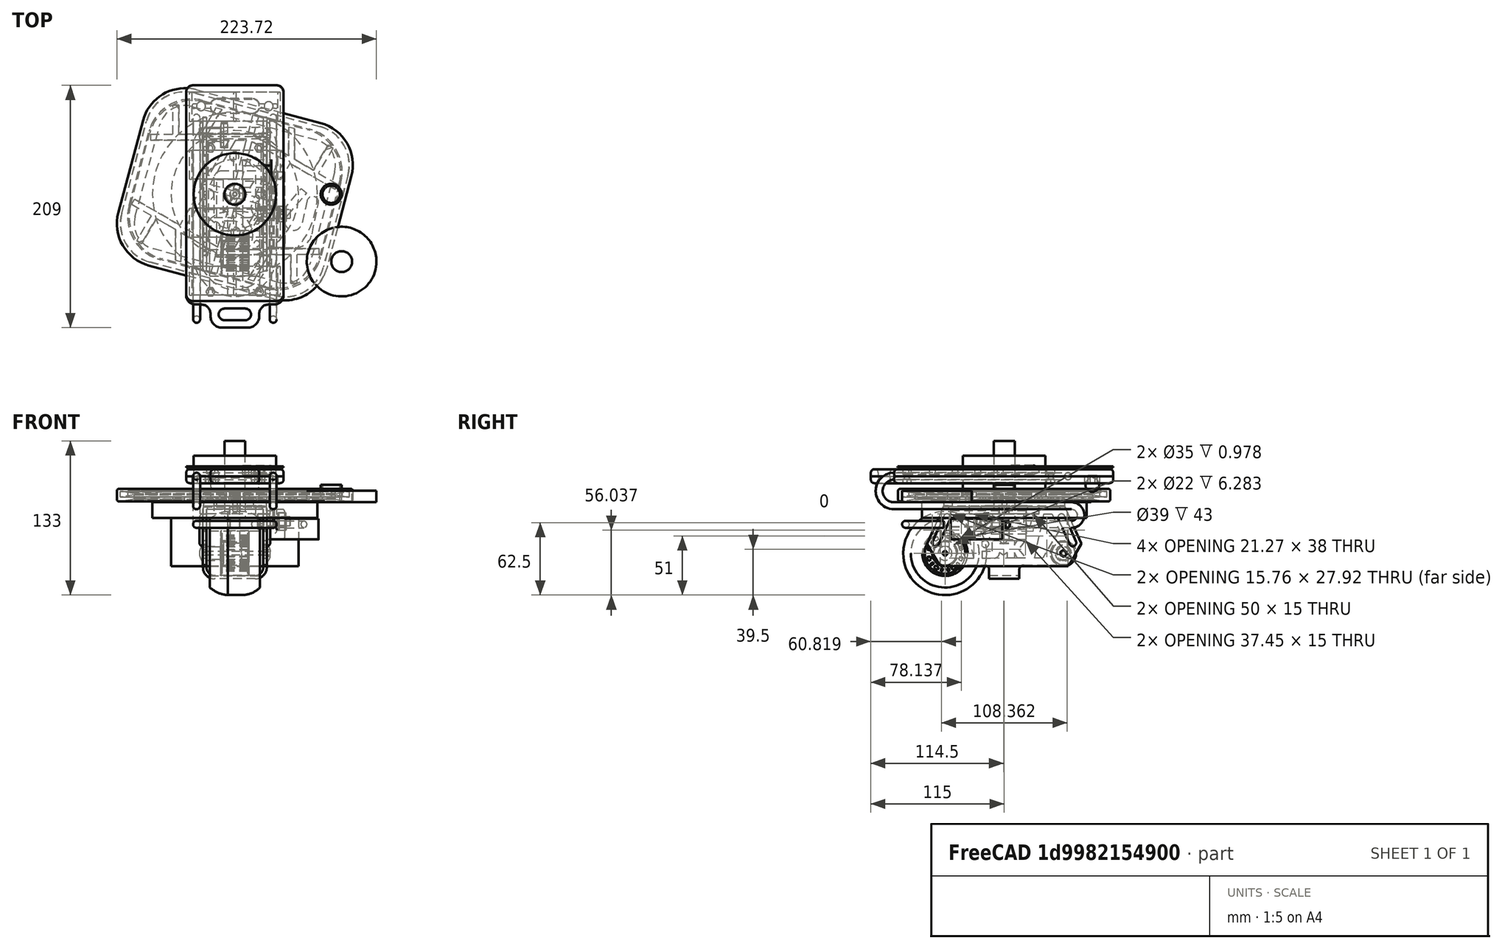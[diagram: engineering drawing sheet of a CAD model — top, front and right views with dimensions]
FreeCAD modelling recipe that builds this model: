
FCSTD DOCUMENT  (FreeCAD 1.0R39285 (Git))
Label: freeskate
License: All rights reserved
LicenseURL: http://en.wikipedia.org/wiki/All_rights_reserved
objects: Sketcher::SketchObject×70, PartDesign::Body×41, PartDesign::Pad×28, PartDesign::FeatureBase×14, PartDesign::Pocket×13, Part::Mirroring×12, PartDesign::Revolution×7, PartDesign::Mirrored×6, Part::Extrusion×4, Part::Cut×4, App::Part×4, PartDesign::MultiTransform×3, PartDesign::SubShapeBinder×3, Part::Revolution×2, App::Link×2, App::FeaturePython×2, PartDesign::AdditivePipe×2, PartDesign::Fillet×2, Part::MultiFuse×2, Part::Offset2D×1, +8 more types
note: 421 computed .brp shape members not serialized (recipe doc carries the construction recipe); baked Part::Feature solids carry a one-line shape summary decoded from their .brp

FEATURE [Sketcher::SketchObject] Sketch  label="plate-outline"
  ArcFitTolerance = 0
  AttachmentOffset = pos=(0,0,4.5) rot=(0,0,1;0rad)
  AttachmentSupport = -> [XY_Plane]
  FullyConstrained = true
  MakeInternals = false
  MapMode = 5
  Placement = pos=(0,0,4.5) rot=(0,0,1;0rad)
  sketch-geometry (8):
    g0: LineSegment StartX=-33 StartY=85.5 StartZ=0 EndX=33 EndY=85.5 EndZ=0
    g1: LineSegment StartX=71 StartY=47.5 StartZ=0 EndX=71 EndY=-47.5 EndZ=0
    g2: LineSegment StartX=33 StartY=-85.5 StartZ=0 EndX=-33 EndY=-85.5 EndZ=0
    g3: LineSegment StartX=-71 StartY=-47.5 StartZ=0 EndX=-71 EndY=47.5 EndZ=0
    g4: ArcOfCircle CenterX=-33 CenterY=47.5 CenterZ=0 NormalX=0 NormalY=0 NormalZ=1 AngleXU=0 Radius=38 StartAngle=1.5708 EndAngle=3.14159
    g5: ArcOfCircle CenterX=33 CenterY=47.5 CenterZ=0 NormalX=0 NormalY=0 NormalZ=1 AngleXU=0 Radius=38 StartAngle=0 EndAngle=1.5708
    g6: ArcOfCircle CenterX=33 CenterY=-47.5 CenterZ=0 NormalX=0 NormalY=0 NormalZ=1 AngleXU=0 Radius=38 StartAngle=4.71239 EndAngle=6.28319
    g7: ArcOfCircle CenterX=-33 CenterY=-47.5 CenterZ=0 NormalX=0 NormalY=0 NormalZ=1 AngleXU=0 Radius=38 StartAngle=3.14159 EndAngle=4.71239
  constraints (18):
    c: Horizontal(g2)
    c: Vertical(g3)
    c: Tangent(g0,g4) = 1.5708
    c: Tangent(g3,g4) = 1.5708
    c: Tangent(g0,g5) = 1.5708
    c: Tangent(g1,g5) = 1.5708
    c: Tangent(g1,g6) = 1.5708
    c: Tangent(g2,g6) = 1.5708
    c: Tangent(g2,g7) = 1.5708
    c: Tangent(g3,g7) = 1.5708
    c: DistanceY(g2,g0) = 171
    c: DistanceX(g3,g1) = 142
    c: Symmetric(g0,g2,g-1)
    c: Horizontal(g0)
    c: Symmetric(g3,g1,g-2)
    c: Vertical(g1)
    c: Radius(g5) = 38
    c: Radius(g6) = 38
FEATURE [PartDesign::Pad] Pad  label="plate-outline-pad"
  Direction = (0,0,1)
  Length = 5
  Length2 = 10
  Profile = -> Sketch
  ReferenceAxis = -> Sketch [N_Axis]
  Suppressed = false
  Type = 0
FEATURE [Sketcher::SketchObject] Sketch002  label="chassis-channel"
  ArcFitTolerance = 0
  FullyConstrained = true
  MakeInternals = false
  MapMode = 5
  Placement = pos=(0,0,0) rot=(1,0,0;1.5708rad)
  sketch-geometry (8):
    g0: LineSegment StartX=-24.5 StartY=-3 StartZ=0 EndX=24.5 EndY=-3 EndZ=0
    g1: LineSegment StartX=27.5 StartY=-6 StartZ=0 EndX=27.5 EndY=-56 EndZ=0
    g2: LineSegment StartX=17.5 StartY=-66 StartZ=0 EndX=-17.5 EndY=-66 EndZ=0
    g3: LineSegment StartX=-27.5 StartY=-56 StartZ=0 EndX=-27.5 EndY=-6 EndZ=0
    g4: ArcOfCircle CenterX=-24.5 CenterY=-6 CenterZ=0 NormalX=0 NormalY=0 NormalZ=1 AngleXU=0 Radius=3 StartAngle=1.5708 EndAngle=3.14159
    g5: ArcOfCircle CenterX=24.5 CenterY=-6 CenterZ=0 NormalX=0 NormalY=0 NormalZ=1 AngleXU=0 Radius=3 StartAngle=0 EndAngle=1.5708
    g6: ArcOfCircle CenterX=17.5 CenterY=-56 CenterZ=0 NormalX=0 NormalY=0 NormalZ=1 AngleXU=0 Radius=10 StartAngle=4.71239 EndAngle=6.28319
    g7: ArcOfCircle CenterX=-17.5 CenterY=-56 CenterZ=0 NormalX=0 NormalY=0 NormalZ=1 AngleXU=0 Radius=10 StartAngle=3.14159 EndAngle=4.71239
  constraints (19):
    c: Horizontal(g0)
    c: Horizontal(g2)
    c: Vertical(g1)
    c: Vertical(g3)
    c: Tangent(g0,g4) = 1.5708
    c: Tangent(g3,g4) = 1.5708
    c: Tangent(g0,g5) = 1.5708
    c: Tangent(g1,g5) = 1.5708
    c: Tangent(g1,g6) = 1.5708
    c: Tangent(g2,g6) = 1.5708
    c: Tangent(g2,g7) = 1.5708
    c: Tangent(g3,g7) = 1.5708
    c: DistanceX(g3,g1) = 55
    c: DistanceY(g2,g0) = 63
    c: Radius(g6) = 10
    c: Radius(g7) = 10
    c: Radius(g5) = 3
    c: Symmetric(g3,g1,g-2)
    c: DistanceY(g0,g-1) = 3
FEATURE [Part::Offset2D] Offset2D
  Fill = true
  Intersection = false
  Join = 0
  Mode = 1
  SelfIntersection = false
  Source = -> Sketch002
  Value = -3
FEATURE [Part::Extrusion] Extrude
  Base = -> Offset2D
  Dir = (0,1,0)
  DirMode = 0
  FaceMakerClass = Part::FaceMakerBullseye
  FaceMakerMode = 3
  LengthFwd = 67
  LengthRev = 67
  Solid = true
  Symmetric = false
FEATURE [Sketcher::SketchObject] Sketch003  label="chassis-profile"
  ArcFitTolerance = 0
  AttachmentSupport = -> [YZ_Plane]
  FullyConstrained = true
  MakeInternals = false
  MapMode = 5
  Placement = pos=(0,0,0) rot=(0.57735,0.57735,0.57735;2.0944rad)
  sketch-geometry (62):
    g0: LineSegment StartX=-52 StartY=-3 StartZ=0 EndX=-66.1267 EndY=-35.1023 EndZ=0
    g1: LineSegment StartX=-66.0262 StartY=-36.7474 StartZ=0 EndX=-56.2891 EndY=-53.1201 EndZ=0
    g2: LineSegment StartX=56.2891 StartY=-53.1201 StartZ=0 EndX=66.0262 EndY=-36.7474 EndZ=0
    g3: LineSegment StartX=66.1267 StartY=-35.1023 StartZ=0 EndX=52 EndY=-3 EndZ=0
    g4: LineSegment StartX=52 StartY=-3 StartZ=0 EndX=-52 EndY=-3 EndZ=0
    g5: LineSegment StartX=-13 StartY=-58 StartZ=0 EndX=-13 EndY=-79 EndZ=0
    g6: LineSegment StartX=-13 StartY=-79 StartZ=0 EndX=13 EndY=-79 EndZ=0
    g7: LineSegment StartX=13 StartY=-79 StartZ=0 EndX=13 EndY=-58 EndZ=0
    g8: LineSegment StartX=-54.742 StartY=-54 StartZ=0 EndX=-17 EndY=-54 EndZ=0
    g9: LineSegment StartX=17 StartY=-54 StartZ=0 EndX=54.742 EndY=-54 EndZ=0
    g10: LineSegment StartX=-34.3393 StartY=-10 StartZ=0 EndX=-41.3393 EndY=-10 EndZ=0
    g11: LineSegment StartX=-41.3393 StartY=-10 StartZ=0 EndX=-47.5 EndY=-24 EndZ=0
    g12: LineSegment StartX=-47.5 StartY=-24 StartZ=0 EndX=-33.2268 EndY=-48 EndZ=0
    g13: LineSegment StartX=-33.2268 StartY=-48 StartZ=0 EndX=-26.2268 EndY=-48 EndZ=0
    g14: LineSegment StartX=-26.2268 StartY=-48 StartZ=0 EndX=-34.3393 EndY=-10 EndZ=0
    g15: LineSegment StartX=26.2268 StartY=-48 StartZ=0 EndX=34.3393 EndY=-10 EndZ=0
    g16: LineSegment StartX=34.3393 StartY=-10 StartZ=0 EndX=41.3393 EndY=-10 EndZ=0
    g17: LineSegment StartX=41.3393 StartY=-10 StartZ=0 EndX=47.5 EndY=-24 EndZ=0
    g18: LineSegment StartX=47.5 StartY=-24 StartZ=0 EndX=33.2268 EndY=-48 EndZ=0
    g19: LineSegment StartX=33.2268 StartY=-48 StartZ=0 EndX=26.2268 EndY=-48 EndZ=0
    g20: LineSegment StartX=25 StartY=-10 StartZ=0 EndX=-25 EndY=-10 EndZ=0
    g21: LineSegment StartX=-25 StartY=-10 StartZ=0 EndX=-22.2858 EndY=-22.7135 EndZ=0
    g22: LineSegment StartX=-22.2858 StartY=-22.7135 StartZ=0 EndX=0 EndY=-25 EndZ=0
    g23: LineSegment StartX=0 StartY=-25 StartZ=0 EndX=22.2858 EndY=-22.7135 EndZ=0
    g24: LineSegment StartX=22.2858 StartY=-22.7135 StartZ=0 EndX=25 EndY=-10 EndZ=0
    g25: Circle CenterX=-51 CenterY=-44 CenterZ=0 NormalX=0 NormalY=0 NormalZ=1 AngleXU=0 Radius=2
    g26: Circle CenterX=51 CenterY=-44 CenterZ=0 NormalX=0 NormalY=0 NormalZ=1 AngleXU=0 Radius=2
    g27: LineSegment StartX=-19.2268 StartY=-42 StartZ=0 EndX=-19.2268 EndY=-48 EndZ=0
    g28: LineSegment StartX=-19.2268 StartY=-48 StartZ=0 EndX=-8.22678 EndY=-48 EndZ=0
    g29: LineSegment StartX=-19.2268 StartY=-42 StartZ=0 EndX=-10.2268 EndY=-42 EndZ=0
    g30: LineSegment StartX=-10.2268 StartY=-42 StartZ=0 EndX=-10.2268 EndY=-33 EndZ=0
    g31: LineSegment StartX=-10.2268 StartY=-33 StartZ=0 EndX=-4.22678 EndY=-33 EndZ=0
    g32: LineSegment StartX=-4.22678 StartY=-33 StartZ=0 EndX=-0.72678 EndY=-36 EndZ=0
    g33: LineSegment StartX=-0.72678 StartY=-36 StartZ=0 EndX=2.77322 EndY=-33 EndZ=0
    g34: LineSegment StartX=2.77322 StartY=-33 StartZ=0 EndX=8.77322 EndY=-33 EndZ=0
    g35: LineSegment StartX=8.77322 StartY=-33 StartZ=0 EndX=8.77322 EndY=-37 EndZ=0
    g36: LineSegment StartX=8.77322 StartY=-37 StartZ=0 EndX=11.2268 EndY=-33 EndZ=0
    g37: LineSegment StartX=11.2268 StartY=-33 StartZ=0 EndX=18.2268 EndY=-33 EndZ=0
    g38: LineSegment StartX=18.2268 StartY=-33 StartZ=0 EndX=12.2268 EndY=-40.5 EndZ=0
    g39: LineSegment StartX=12.2268 StartY=-40.5 StartZ=0 EndX=18.2268 EndY=-48 EndZ=0
    g40: LineSegment StartX=18.2268 StartY=-48 StartZ=0 EndX=11.2268 EndY=-48 EndZ=0
    g41: LineSegment StartX=11.2268 StartY=-48 StartZ=0 EndX=8.77322 EndY=-43.5 EndZ=0
    g42: LineSegment StartX=8.77322 StartY=-43.5 StartZ=0 EndX=8.77322 EndY=-48 EndZ=0
    g43: LineSegment StartX=8.77322 StartY=-48 StartZ=0 EndX=2.77322 EndY=-48 EndZ=0
    g44: LineSegment StartX=2.77322 StartY=-48 StartZ=0 EndX=2.77322 EndY=-43.5 EndZ=0
    g45: LineSegment StartX=2.77322 StartY=-43.5 StartZ=0 EndX=-0.72678 EndY=-45.5 EndZ=0
    g46: LineSegment StartX=-0.72678 StartY=-45.5 StartZ=0 EndX=-4.22678 EndY=-43.5 EndZ=0
    g47: LineSegment StartX=-4.22678 StartY=-43.5 StartZ=0 EndX=-4.22678 EndY=-44 EndZ=0
    g48: Circle CenterX=-16.2268 CenterY=-36 CenterZ=0 NormalX=0 NormalY=0 NormalZ=1 AngleXU=0 Radius=3
    g49: ArcOfCircle CenterX=-8.22678 CenterY=-44 CenterZ=0 NormalX=0 NormalY=0 NormalZ=1 AngleXU=0 Radius=4 StartAngle=4.71239 EndAngle=6.28319
    g50: ArcOfCircle CenterX=17 CenterY=-58 CenterZ=0 NormalX=0 NormalY=0 NormalZ=1 AngleXU=0 Radius=4 StartAngle=1.5708 EndAngle=3.14159
    g51: GeomPoint [constr] X=13 Y=-54 Z=0
    g52: ArcOfCircle CenterX=-17 CenterY=-58 CenterZ=0 NormalX=0 NormalY=0 NormalZ=1 AngleXU=0 Radius=4 StartAngle=0 EndAngle=1.5708
    g53: GeomPoint [constr] X=-13 Y=-54 Z=0
    g54: ArcOfCircle CenterX=64.4791 CenterY=-35.8273 CenterZ=0 NormalX=0 NormalY=0 NormalZ=1 AngleXU=0 Radius=1.8 StartAngle=5.74666 EndAngle=6.69773
    g55: GeomPoint [constr] X=66.5 Y=-35.9507 Z=0
    g56: ArcOfCircle CenterX=-64.4791 CenterY=-35.8273 CenterZ=0 NormalX=0 NormalY=0 NormalZ=1 AngleXU=0 Radius=1.8 StartAngle=2.72704 EndAngle=3.67812
    g57: GeomPoint [constr] X=-66.5 Y=-35.9507 Z=0
    g58: ArcOfCircle CenterX=54.742 CenterY=-52.2 CenterZ=0 NormalX=0 NormalY=0 NormalZ=1 AngleXU=0 Radius=1.8 StartAngle=4.71239 EndAngle=5.74666
    g59: GeomPoint [constr] X=55.7658 Y=-54 Z=0
    g60: ArcOfCircle CenterX=-54.742 CenterY=-52.2 CenterZ=0 NormalX=0 NormalY=0 NormalZ=1 AngleXU=0 Radius=1.8 StartAngle=3.67812 EndAngle=4.71239
    g61: GeomPoint [constr] X=-55.7658 Y=-54 Z=0
  constraints (161):
    c: Coincident(g4,g3)
    c: Coincident(g4,g0)
    c: Distance(g57,g61) = 21
    c: Symmetric(g61,g59,g-2)
    c: Symmetric(g57,g55,g-2)
    c: DistanceX(g0,g3) = 104
    c: Symmetric(g0,g3,g-2)
    c: DistanceY(g0,g-1) = 3
    c: Vertical(g5)
    c: Coincident(g6,g5)
    c: Horizontal(g6)
    c: Coincident(g7,g6)
    c: Vertical(g7)
    c: Symmetric(g53,g51,g-2)
    c: Horizontal(g8)
    c: DistanceY(g6,g51) = 25
    c: DistanceY(g59,g3) = 51
    c: DistanceX(g5,g6) = 26
    c: Distance(g0,g57) = 36
    c: Horizontal(g10)
    c: Coincident(g11,g10)
    c: Coincident(g12,g11)
    c: Coincident(g13,g12)
    c: Horizontal(g13)
    c: Coincident(g14,g13)
    c: Coincident(g14,g10)
    c: Coincident(g16,g15)
    c: Coincident(g17,g16)
    c: Coincident(g18,g17)
    c: Coincident(g19,g15)
    c: Symmetric(g13,g15,g-2)
    c: Coincident(g19,g18)
    c: Symmetric(g18,g12,g-2)
    c: Symmetric(g10,g15,g-2)
    c: Symmetric(g10,g16,g-2)
    c: Symmetric(g11,g17,g-2)
    c: Coincident(g21,g20)
    c: Coincident(g22,g21)
    c: PointOnObject(g22,g-2)
    c: Coincident(g23,g22)
    c: Coincident(g24,g20)
    c: Symmetric(g21,g23,g-2)
    c: Symmetric(g20,g20,g-2)
    c: Coincident(g23,g24)
    c: Diameter(g25) = 4
    c: Diameter(g26) = 4
    c: Symmetric(g25,g26,g-2)
    c: DistanceX(g25,g26) = 102
    c: DistanceY(g25,g0) = 41
    c: DistanceX(g10,g10) = 7
    c: DistanceY(g10,g0) = 7
    c: Horizontal(g10,g20)
    c: Parallel(g0,g11)
    c: DistanceY(g11,g0) = 21
    c: DistanceY(g61,g12) = 6
    c: DistanceX(g12,g13) = 7
    c: Parallel(g12,g1)
    c: DistanceX(g11,g17) = 95
    c: DistanceX(g57,g55) = 133
    c: DistanceX(g20,g20) = 50
    c: Parallel(g14,g21)
    c: DistanceY(g22,g20) = 15
    c: Distance(g20,g21) = 13
    c: Vertical(g27)
    c: Coincident(g28,g27)
    c: Horizontal(g28)
    c: Coincident(g29,g27)
    c: Horizontal(g29)
    c: Coincident(g30,g29)
    c: Vertical(g30)
    c: Coincident(g31,g30)
    c: Horizontal(g31)
    c: Coincident(g32,g31)
    c: Coincident(g33,g32)
    c: Coincident(g34,g33)
    c: Horizontal(g34)
    c: Coincident(g35,g34)
    c: Vertical(g35)
    c: Coincident(g36,g35)
    c: Coincident(g37,g36)
    c: Horizontal(g37)
    c: Coincident(g38,g37)
    c: Coincident(g39,g38)
    c: Coincident(g40,g39)
    c: Horizontal(g40)
    c: Coincident(g41,g40)
    c: Coincident(g42,g41)
    c: Vertical(g42)
    c: Coincident(g43,g42)
    c: Horizontal(g43)
    c: Coincident(g44,g43)
    c: Vertical(g44)
    c: Coincident(g45,g44)
    c: Coincident(g46,g45)
    c: Coincident(g47,g46)
    c: Vertical(g47)
    c: Horizontal(g12,g27)
    c: Horizontal(g12,g43)
    c: Horizontal(g12,g40)
    c: DistanceY(g27,g30) = 15
    c: DistanceX(g13,g27) = 7
    c: DistanceX(g39,g15) = 8
    c: Vertical(g37,g39)
    c: DistanceX(g38,g39) = 6
    c: Horizontal(g30,g37)
    c: DistanceY(g38,g37) = 7.5
    c: DistanceX(g36,g37) = 7
    c: Horizontal(g30,g34)
    c: Diameter(g48) = 6
    c: DistanceY(g48,g30) = 3
    c: DistanceX(g27,g48) = 3
    c: DistanceX(g27,g29) = 9
    c: DistanceX(g30,g31) = 6
    c: DistanceX(g33,g34) = 6
    c: DistanceY(g32,g31) = 3
    c: DistanceX(g31,g32) = 3.5
    c: DistanceX(g32,g33) = 3.5
    c: DistanceY(g35,g34) = 4
    c: DistanceY(g27,g27) = 6
    c: DistanceY(g27,g46) = 4.5
    c: Horizontal(g46,g44)
    c: Horizontal(g46,g41)
    c: Vertical(g36,g40)
    c: Vertical(g35,g41)
    c: Vertical(g33,g44)
    c: Vertical(g32,g45)
    c: Vertical(g31,g46)
    c: DistanceY(g45,g46) = 2
    c: Tangent(g28,g49) = -1.5708
    c: Tangent(g47,g49) = 1.5708
    c: Radius(g49) = 4
    c: PointOnObject(g51,g7)
    c: PointOnObject(g51,g9)
    c: Tangent(g7,g50) = 1.5708
    c: Tangent(g9,g50) = 1.5708
    c: PointOnObject(g53,g5)
    c: PointOnObject(g53,g8)
    c: Tangent(g5,g52) = 1.5708
    c: Tangent(g8,g52) = 1.5708
    c: Radius(g52) = 4
    c: Radius(g50) = 4
    c: PointOnObject(g55,g2)
    c: PointOnObject(g55,g3)
    c: Tangent(g2,g54) = -1.5708
    c: Tangent(g3,g54) = -1.5708
    c: Radius(g54) = 1.8
    c: PointOnObject(g57,g0)
    c: PointOnObject(g57,g1)
    c: Tangent(g0,g56) = -1.5708
    c: Tangent(g1,g56) = -1.5708
    c: Radius(g56) = 1.8
    c: PointOnObject(g59,g2)
    c: PointOnObject(g59,g9)
    c: Tangent(g2,g58) = -1.5708
    c: Tangent(g9,g58) = -1.5708
    c: PointOnObject(g61,g1)
    c: PointOnObject(g61,g8)
    c: Tangent(g1,g60) = -1.5708
    c: Tangent(g8,g60) = -1.5708
    c: Radius(g58) = 1.8
    c: Radius(g60) = 1.8
FEATURE [Part::Extrusion] Extrude001
  Base = -> Sketch003
  Dir = (1,0,0)
  DirMode = 0
  FaceMakerClass = Part::FaceMakerBullseye
  FaceMakerMode = 3
  LengthFwd = 30
  LengthRev = 30
  Solid = true
  Symmetric = false
FEATURE [Part::MultiCommon] Common  label="chassis-side-front"
  Shapes = -> [Extrude,Extrude001]
FEATURE [Sketcher::SketchObject] Sketch004  label="wheel-profile"
  ArcFitTolerance = 0
  AttachmentOffset = pos=(0,0,-44) rot=(0,0,1;0rad)
  AttachmentSupport = -> [XY_Plane]
  FullyConstrained = true
  MakeInternals = false
  MapMode = 5
  Placement = pos=(0,0,-44) rot=(0,0,1;0rad)
  sketch-geometry (7):
    g0: LineSegment StartX=-21.5 StartY=70.5 StartZ=0 EndX=-21.5 EndY=80.5 EndZ=0
    g1: ArcOfCircle CenterX=-4.64445 CenterY=62.0368 CenterZ=0 NormalX=0 NormalY=0 NormalZ=1 AngleXU=0 Radius=25 StartAngle=1.62504 EndAngle=2.31071
    g2: LineSegment StartX=-21.5 StartY=70.5 StartZ=0 EndX=21.5 EndY=70.5 EndZ=0
    g3: LineSegment StartX=21.5 StartY=70.5 StartZ=0 EndX=21.5 EndY=80.5 EndZ=0
    g4: LineSegment StartX=6 StartY=87 StartZ=0 EndX=-6 EndY=87 EndZ=0
    g5: ArcOfCircle CenterX=6 CenterY=65.2692 CenterZ=0 NormalX=0 NormalY=0 NormalZ=1 AngleXU=0 Radius=21.7308 StartAngle=0.776637 EndAngle=1.5708
    g6: GeomPoint [constr] X=0 Y=51 Z=0
  constraints (18):
    c: Vertical(g0)
    c: DistanceY(g0,g0) = 10
    c: Coincident(g2,g0)
    c: DistanceX(g2,g2) = 43
    c: Coincident(g3,g2)
    c: Coincident(g4,g1)
    c: Tangent(g4,g5) = -1.5708
    c: Symmetric(g1,g4,g-2)
    c: Symmetric(g0,g2,g-2)
    c: Symmetric(g0,g3,g-2)
    c: DistanceX(g1,g4) = 12
    c: Coincident(g1,g0)
    c: Coincident(g5,g3)
    c: Radius(g1) = 25
    c: PointOnObject(g6,g-2)
    c: DistanceY(g-1,g6) = 51
    c: DistanceY(g6,g0) = 19.5
    c: DistanceY(g6,g1) = 36
FEATURE [Part::Revolution] Revolve  label="wheel-back"
  Angle = 360
  Axis = (1,0,0)
  Base = (0,51,-44)
  FaceMakerClass = Part::FaceMakerBullseye
  Solid = true
  Source = -> Sketch004
  Symmetric = false
FEATURE [Part::Mirroring] Part__Mirroring  label="wheel-front"
  Base = (0,0,0)
  Normal = (0,1,0)
  Source = -> Revolve
FEATURE [Sketcher::SketchObject] Sketch008  label="axle-profile"
  ArcFitTolerance = 0
  AttachmentOffset = pos=(0,0,51) rot=(0,0,1;0rad)
  FullyConstrained = true
  MakeInternals = false
  MapMode = 5
  Placement = pos=(0,-51,1.1e-14) rot=(1,0,0;1.5708rad)
  sketch-geometry (9):
    g0: LineSegment StartX=27.5 StartY=-42.5 StartZ=0 EndX=-27.5 EndY=-42.5 EndZ=0
    g1: LineSegment StartX=-27.5 StartY=-42.5 StartZ=0 EndX=-27.5 EndY=-37 EndZ=0
    g2: LineSegment StartX=-27.5 StartY=-37 StartZ=0 EndX=-28 EndY=-37 EndZ=0
    g3: ArcOfCircle CenterX=-19.5 CenterY=-44 CenterZ=0 NormalX=0 NormalY=0 NormalZ=1 AngleXU=0 Radius=11.0114 StartAngle=2.45267 EndAngle=3.14159
    g4: GeomPoint [constr] X=0 Y=-44 Z=0
    g5: LineSegment StartX=27.5 StartY=-42.5 StartZ=0 EndX=27.5 EndY=-37 EndZ=0
    g6: LineSegment StartX=27.5 StartY=-37 StartZ=0 EndX=28 EndY=-37 EndZ=0
    g7: ArcOfCircle CenterX=23.5 CenterY=-42.5649 CenterZ=0 NormalX=0 NormalY=0 NormalZ=1 AngleXU=0 Radius=7.15671 StartAngle=6.0813 EndAngle=7.174
    g8: LineSegment StartX=-30.5114 StartY=-44 StartZ=0 EndX=30.5114 EndY=-44 EndZ=0
  constraints (24):
    c: Vertical(g1)
    c: Horizontal(g2)
    c: Coincident(g2,g1)
    c: Coincident(g1,g0)
    c: Coincident(g3,g2)
    c: PointOnObject(g4,g-2)
    c: DistanceY(g4,g-1) = 44
    c: Horizontal(g3,g4)
    c: Horizontal(g3,g4)
    c: Symmetric(g0,g0,g-2)
    c: DistanceX(g0,g4) = 27.5
    c: Coincident(g5,g0)
    c: Coincident(g6,g5)
    c: DistanceX(g1,g3) = 8
    c: DistanceX(g2,g1) = 0.5
    c: Symmetric(g1,g5,g-2)
    c: Symmetric(g2,g6,g-2)
    c: Coincident(g7,g6)
    c: Symmetric(g3,g7,g-2)
    c: DistanceY(g4,g0) = 1.5
    c: DistanceY(g4,g1) = 7
    c: DistanceX(g7,g5) = 4
    c: Coincident(g8,g3)
    c: Coincident(g8,g7)
FEATURE [Part::Revolution] Revolve001  label="axis-profile-revolve"
  Angle = 360
  Axis = (1,0,0)
  Base = (2,-51,-44)
  FaceMakerClass = Part::FaceMakerBullseye
  Solid = true
  Source = -> Sketch008
  Symmetric = false
FEATURE [Sketcher::SketchObject] Sketch009  label="axle-hex"
  ArcFitTolerance = 0
  AttachmentOffset = pos=(0,0,31) rot=(0,0,1;0rad)
  FullyConstrained = true
  MakeInternals = false
  MapMode = 5
  Placement = pos=(31,-7e-15,7e-15) rot=(0.57735,0.57735,0.57735;2.0944rad)
  sketch-geometry (7):
    g0: LineSegment StartX=-48.5 StartY=-42.5566 StartZ=0 EndX=-51 EndY=-41.1132 EndZ=0
    g1: LineSegment StartX=-51 StartY=-41.1132 StartZ=0 EndX=-53.5 EndY=-42.5566 EndZ=0
    g2: LineSegment StartX=-53.5 StartY=-42.5566 StartZ=0 EndX=-53.5 EndY=-45.4434 EndZ=0
    g3: LineSegment StartX=-53.5 StartY=-45.4434 StartZ=0 EndX=-51 EndY=-46.8868 EndZ=0
    g4: LineSegment StartX=-51 StartY=-46.8868 StartZ=0 EndX=-48.5 EndY=-45.4434 EndZ=0
    g5: LineSegment StartX=-48.5 StartY=-45.4434 StartZ=0 EndX=-48.5 EndY=-42.5566 EndZ=0
    g6: Circle [constr] CenterX=-51 CenterY=-44 CenterZ=0 NormalX=0 NormalY=0 NormalZ=1 AngleXU=0 Radius=2.88675
  constraints (17):
    c: Coincident(g0,g1)
    c: Coincident(g1,g2)
    c: Coincident(g2,g3)
    c: Coincident(g3,g4)
    c: Coincident(g4,g5)
    c: Coincident(g5,g0)
    c: Equal(g0, g1-g5) x5
    c: PointOnObject(g0,g6)
    c: PointOnObject(g1,g6)
    c: PointOnObject(g2,g6)
    c: PointOnObject(g3,g6)
    c: PointOnObject(g4,g6)
    c: PointOnObject(g5,g6)
    c: Vertical(g5)
    c: DistanceY(g6,g-1) = 44
    c: DistanceX(g2,g4) = 5
    c: DistanceX(g6,g-1) = 51
FEATURE [Part::Extrusion] Extrude002  label="axle-hex-extrude"
  Base = -> Sketch009
  Dir = (-1,0,0)
  DirMode = 0
  FaceMakerClass = Part::FaceMakerBullseye
  FaceMakerMode = 3
  LengthFwd = 3
  LengthRev = 0
  Solid = true
  Symmetric = false
FEATURE [Part::Cut] Cut  label="axle-front"
  Base = -> Revolve001
  Tool = -> Extrude002
FEATURE [Part::Mirroring] Part__Mirroring001  label="axle-back"
  Base = (0,0,0)
  Normal = (0,1,0)
  Source = -> Cut
FEATURE [Sketcher::SketchObject] Sketch010  label="outline"
  ArcFitTolerance = 0
  AttachmentSupport = -> [XY_Plane002]
  FullyConstrained = true
  MakeInternals = false
  MapMode = 5
  sketch-geometry (6):
    g0: LineSegment StartX=16 StartY=52 StartZ=0 EndX=27 EndY=45 EndZ=0
    g1: LineSegment StartX=-27 StartY=52 StartZ=0 EndX=16 EndY=52 EndZ=0
    g2: LineSegment StartX=27 StartY=45 StartZ=0 EndX=27 EndY=-52 EndZ=0
    g3: LineSegment StartX=-27 StartY=-45 StartZ=0 EndX=-16 EndY=-52 EndZ=0
    g4: LineSegment StartX=-27 StartY=52 StartZ=0 EndX=-27 EndY=-45 EndZ=0
    g5: LineSegment StartX=-16 StartY=-52 StartZ=0 EndX=27 EndY=-52 EndZ=0
  constraints (18):
    c: Coincident(g1,g0)
    c: Horizontal(g1)
    c: Coincident(g2,g0)
    c: Vertical(g2)
    c: Coincident(g4,g1)
    c: Coincident(g4,g3)
    c: Vertical(g4)
    c: Coincident(g5,g3)
    c: Coincident(g5,g2)
    c: Horizontal(g5)
    c: DistanceY(g0,g0) = 7
    c: DistanceX(g0,g0) = 11
    c: DistanceX(g1,g-1) = 27
    c: DistanceX(g-1,g0) = 27
    c: DistanceX(g3,g3) = 11
    c: DistanceY(g3,g3) = 7
    c: DistanceY(g-1,g1) = 52
    c: DistanceY(g2,g-1) = 52
FEATURE [PartDesign::Pad] Pad003  label="outline-pad"
  Direction = (0,0,1)
  Length = 4
  Length2 = 10
  Profile = -> Sketch010
  ReferenceAxis = -> Sketch010 [N_Axis]
  Reversed = true
  Suppressed = false
  Type = 0
FEATURE [PartDesign::Body] Body002  label="shock-absorber"
  AllowCompound = false
  Group = -> [Sketch010,Pad003]
  Origin = -> Origin002
  Tip = -> Pad003
FEATURE [Sketcher::SketchObject] Sketch011  label="chassis-top"
  ArcFitTolerance = 0
  AttachmentSupport = -> [XY_Plane002]
  FullyConstrained = true
  MakeInternals = false
  MapMode = 5
  sketch-geometry (18):
    g0: LineSegment StartX=-24 StartY=58 StartZ=0 EndX=24 EndY=58 EndZ=0
    g1: LineSegment StartX=24 StartY=58 StartZ=0 EndX=23.5 EndY=51 EndZ=0
    g2: LineSegment StartX=20.2781 StartY=48 StartZ=0 EndX=-20.2781 EndY=48 EndZ=0
    g3: LineSegment StartX=-23.5 StartY=51 StartZ=0 EndX=-24 EndY=58 EndZ=0
    g4: LineSegment StartX=-12 StartY=20 StartZ=0 EndX=18 EndY=20 EndZ=0
    g5: LineSegment StartX=18 StartY=20 StartZ=0 EndX=18 EndY=-14 EndZ=0
    g6: LineSegment StartX=12 StartY=-20 StartZ=0 EndX=-18 EndY=-20 EndZ=0
    g7: LineSegment StartX=-18 StartY=-20 StartZ=0 EndX=-18 EndY=14 EndZ=0
    g8: LineSegment StartX=-20.2781 StartY=-48 StartZ=0 EndX=20.2781 EndY=-48 EndZ=0
    g9: LineSegment StartX=23.2629 StartY=-50.6987 StartZ=0 EndX=24 EndY=-58 EndZ=0
    g10: LineSegment StartX=24 StartY=-58 StartZ=0 EndX=-24 EndY=-58 EndZ=0
    g11: LineSegment StartX=-24 StartY=-58 StartZ=0 EndX=-23.5 EndY=-51 EndZ=0
    g12: ArcOfCircle CenterX=-20.2781 CenterY=51.2301 CenterZ=0 NormalX=0 NormalY=0 NormalZ=1 AngleXU=0 Radius=3.23014 StartAngle=3.2129 EndAngle=4.71239
    g13: ArcOfCircle CenterX=20.2781 CenterY=51.2301 CenterZ=0 NormalX=0 NormalY=0 NormalZ=1 AngleXU=0 Radius=3.23014 StartAngle=4.71239 EndAngle=6.21188
    g14: ArcOfCircle CenterX=-20.2781 CenterY=-51.2301 CenterZ=0 NormalX=0 NormalY=0 NormalZ=1 AngleXU=0 Radius=3.23014 StartAngle=1.5708 EndAngle=3.07029
    g15: ArcOfCircle CenterX=20.2781 CenterY=-51 CenterZ=0 NormalX=0 NormalY=0 NormalZ=1 AngleXU=0 Radius=3 StartAngle=0.100613 EndAngle=1.5708
    g16: ArcOfCircle CenterX=-12 CenterY=14 CenterZ=0 NormalX=0 NormalY=0 NormalZ=1 AngleXU=0 Radius=6 StartAngle=1.5708 EndAngle=3.14159
    g17: ArcOfCircle CenterX=12 CenterY=-14 CenterZ=0 NormalX=0 NormalY=0 NormalZ=1 AngleXU=0 Radius=6 StartAngle=4.71239 EndAngle=6.28319
  constraints (42):
    c: Coincident(g0,g1)
    c: Coincident(g3,g0)
    c: Coincident(g4,g5)
    c: Coincident(g6,g7)
    c: Horizontal(g4)
    c: Horizontal(g6)
    c: Vertical(g5)
    c: Vertical(g7)
    c: Coincident(g9,g10)
    c: Coincident(g10,g11)
    c: Symmetric(g0,g0,g-2)
    c: DistanceX(g0,g0) = 48
    c: Tangent(g2,g12) = 1.5708
    c: Tangent(g3,g12) = 1.5708
    c: Tangent(g1,g13) = 1.5708
    c: Tangent(g2,g13) = 1.5708
    c: DistanceY(g2,g0) = 10
    c: DistanceY(g-1,g2) = 48
    c: DistanceX(g3,g1) = 47
    c: Tangent(g8,g14) = 1.5708
    c: Tangent(g11,g14) = 1.5708
    c: Tangent(g8,g15) = 1.5708
    c: Tangent(g9,g15) = 1.5708
    c: Radius(g15) = 3
    c: Symmetric(g2,g8,g-1)
    c: Symmetric(g10,g0,g-1)
    c: Symmetric(g9,g0,g-1)
    c: Symmetric(g11,g3,g-1)
    c: Symmetric(g3,g1,g-2)
    c: Symmetric(g2,g2,g-2)
    c: DistanceY(g2,g3) = 3
    c: Symmetric(g8,g2,g-1)
    c: Tangent(g4,g16) = 1.5708
    c: Tangent(g7,g16) = 1.5708
    c: Tangent(g5,g17) = 1.5708
    c: Tangent(g6,g17) = 1.5708
    c: Radius(g16) = 6
    c: Radius(g17) = 6
    c: DistanceY(g6,g-1) = 20
    c: DistanceY(g-1,g4) = 20
    c: DistanceX(g6,g-1) = 18
    c: DistanceX(g-1,g4) = 18
FEATURE [Part::Extrusion] Extrude003  label="chassis-top-extrude"
  Base = -> Sketch011
  Dir = (0,0,-1)
  DirMode = 0
  FaceMakerClass = Part::FaceMakerBullseye
  FaceMakerMode = 3
  LengthFwd = 10
  LengthRev = 0
  Solid = true
  Symmetric = false
FEATURE [Part::Cut] Cut001  label="chassis-base"
  Base = -> Common
  Tool = -> Extrude003
FEATURE [Sketcher::SketchObject] Sketch012  label="top-profile"
  ArcFitTolerance = 0
  AttachmentOffset = pos=(0,0,-44) rot=(0,0,1;0rad)
  FullyConstrained = false
  MakeInternals = false
  MapMode = 5
  Placement = pos=(0,51,-44) rot=(0,0,1;0rad)
  sketch-geometry (13):
    g0: LineSegment StartX=11.9778 StartY=-19.5 StartZ=0 EndX=-11.9778 EndY=-19.5 EndZ=0
    g1: LineSegment StartX=-11.9778 StartY=-19.5 StartZ=0 EndX=-11.9778 EndY=-17.5 EndZ=0
    g2: LineSegment StartX=-11.9778 StartY=-17.5 StartZ=0 EndX=-11 EndY=-17.5 EndZ=0
    g3: LineSegment StartX=-11 StartY=-17.5 StartZ=0 EndX=-12 EndY=-11 EndZ=0
    g4: LineSegment StartX=-12 StartY=-11 StartZ=0 EndX=-5.71671 EndY=-11 EndZ=0
    g5: LineSegment StartX=-5.71671 StartY=-11 StartZ=0 EndX=-5.71671 EndY=-10 EndZ=0
    g6: LineSegment StartX=-5.71671 StartY=-10 StartZ=0 EndX=5.71671 EndY=-10 EndZ=0
    g7: LineSegment StartX=5.71671 StartY=-10 StartZ=0 EndX=5.71671 EndY=-11 EndZ=0
    g8: LineSegment StartX=5.71671 StartY=-11 StartZ=0 EndX=12 EndY=-11 EndZ=0
    g9: LineSegment StartX=12 StartY=-11 StartZ=0 EndX=11 EndY=-17.5 EndZ=0
    g10: LineSegment StartX=11 StartY=-17.5 StartZ=0 EndX=11.9778 EndY=-17.5 EndZ=0
    g11: LineSegment StartX=11.9778 StartY=-17.5 StartZ=0 EndX=11.9778 EndY=-19.5 EndZ=0
    g12: GeomPoint [constr] X=0 Y=0 Z=0
  constraints (29):
    c: Coincident(g1,g0)
    c: Vertical(g1)
    c: Coincident(g2,g1)
    c: Horizontal(g2)
    c: Coincident(g3,g2)
    c: Horizontal(g4)
    c: Coincident(g5,g4)
    c: Vertical(g5)
    c: Coincident(g6,g5)
    c: Coincident(g7,g6)
    c: Coincident(g8,g7)
    c: Coincident(g9,g8)
    c: Coincident(g10,g9)
    c: Coincident(g11,g10)
    c: Coincident(g11,g0)
    c: Symmetric(g0,g0,g-2)
    c: Symmetric(g1,g10,g-2)
    c: Symmetric(g2,g9,g-2)
    c: Symmetric(g3,g8,g-2)
    c: Coincident(g3,g4)
    c: Symmetric(g4,g7,g-2)
    c: Symmetric(g5,g6,g-2)
    c: DistanceY(g0,g12) = 19.5
    c: DistanceX(g3,g8) = 24
    c: DistanceX(g3,g2) = 1
    c: DistanceY(g3,g12) = 11
    c: DistanceY(g5,g12) = 10
    c: DistanceY(g1,g1) = 2
    c: Coincident(g12,g-1)
FEATURE [Sketcher::SketchObject] Sketch018  label="rib-outlines"
  ArcFitTolerance = 0
  AttachmentSupport = -> [XY_Plane]
  FullyConstrained = true
  MakeInternals = false
  MapMode = 5
  sketch-geometry (29):
    g0: LineSegment StartX=-2.5 StartY=2.5 StartZ=0 EndX=-47.8236 EndY=2.5 EndZ=0
    g1: LineSegment StartX=-2.5 StartY=2.5 StartZ=0 EndX=-2.5 EndY=22.8798 EndZ=0
    g2: LineSegment StartX=0 StartY=28.726 StartZ=0 EndX=-38.0635 EndY=38.9251 EndZ=0
    g3: LineSegment StartX=-38.0635 StartY=38.9251 StartZ=0 EndX=-26.4167 EndY=82.3918 EndZ=0
    g4: LineSegment StartX=-31.2463 StartY=83.6859 StartZ=0 EndX=-26.4167 EndY=82.3918 EndZ=0
    g5: LineSegment StartX=-53 StartY=2.5 StartZ=0 EndX=-70 EndY=2.5 EndZ=0
    g6: LineSegment StartX=-70 StartY=2.5 StartZ=0 EndX=-70 EndY=0 EndZ=0
    g7: LineSegment StartX=-70 StartY=0 StartZ=0 EndX=0 EndY=0 EndZ=0
    g8: LineSegment StartX=0 StartY=0 StartZ=0 EndX=0 EndY=28.726 EndZ=0
    g9: LineSegment StartX=-39.3576 StartY=34.0955 StartZ=0 EndX=-43.952 EndY=16.9491 EndZ=0
    g10: LineSegment StartX=-43.952 StartY=16.9491 StartZ=0 EndX=-9.65926 EndY=26.1378 EndZ=0
    g11: LineSegment StartX=-9.65926 StartY=26.1378 StartZ=0 EndX=-39.3576 EndY=34.0955 EndZ=0
    g12: LineSegment StartX=-2.5 StartY=22.8798 StartZ=0 EndX=-45.4463 EndY=11.3723 EndZ=0
    g13: LineSegment StartX=-45.4463 StartY=11.3723 StartZ=0 EndX=-47.8236 EndY=2.5 EndZ=0
    g14: LineSegment StartX=-36.2863 StartY=64.8764 StartZ=0 EndX=-60.4344 EndY=71.3469 EndZ=0
    g15: LineSegment StartX=-60.4344 StartY=71.3469 StartZ=0 EndX=-61.7285 EndY=66.5172 EndZ=0
    g16: LineSegment StartX=-61.7285 StartY=66.5172 StartZ=0 EndX=-37.5804 EndY=60.0467 EndZ=0
    g17: LineSegment StartX=-42.498 StartY=41.6942 StartZ=0 EndX=-68 EndY=34.8609 EndZ=0
    g18: LineSegment StartX=-68 StartY=34.8609 StartZ=0 EndX=-68 EndY=29.8609 EndZ=0
    g19: LineSegment StartX=-68 StartY=29.8609 StartZ=0 EndX=-43.9413 EndY=36.3074 EndZ=0
    g20: LineSegment StartX=-31.2463 StartY=83.6859 StartZ=0 EndX=-36.2863 EndY=64.8764 EndZ=0
    g21: LineSegment StartX=-37.5804 StartY=60.0467 StartZ=0 EndX=-42.498 EndY=41.6942 EndZ=0
    g22: LineSegment StartX=-43.9413 StartY=36.3074 StartZ=0 EndX=-53 EndY=2.5 EndZ=0
    g23: LineSegment [constr] StartX=-31.2463 StartY=83.6859 StartZ=0 EndX=-53 EndY=2.5 EndZ=0
    g24: LineSegment [constr] StartX=-26.4167 StartY=82.3918 StartZ=0 EndX=-47.8236 EndY=2.5 EndZ=0
    g25: LineSegment [constr] StartX=-43.952 StartY=16.9491 StartZ=0 EndX=-49.5288 EndY=15.4548 EndZ=0
    g26: LineSegment [constr] StartX=-53 StartY=2.5 StartZ=0 EndX=-53.6699 EndY=0 EndZ=0
    g27: LineSegment [constr] StartX=-9.65926 StartY=26.1378 StartZ=0 EndX=0 EndY=28.726 EndZ=0
    g28: LineSegment [constr] StartX=-43.952 StartY=16.9491 StartZ=0 EndX=-42.6579 EndY=12.1195 EndZ=0
  constraints (83):
    c: Horizontal(g0)
    c: Coincident(g1,g0)
    c: Vertical(g1)
    c: PointOnObject(g2,g-2)
    c: Coincident(g3,g2)
    c: Coincident(g4,g3)
    c: Horizontal(g5)
    c: Coincident(g6,g5)
    c: PointOnObject(g6,g-1)
    c: Vertical(g6)
    c: Coincident(g7,g6)
    c: Coincident(g7,g-1)
    c: Coincident(g8,g7)
    c: Coincident(g8,g2)
    c: Coincident(g10,g9)
    c: Coincident(g11,g10)
    c: Coincident(g11,g9)
    c: Coincident(g12,g1)
    c: Coincident(g13,g12)
    c: Coincident(g13,g0)
    c: Coincident(g15,g14)
    c: Coincident(g16,g15)
    c: Coincident(g18,g17)
    c: Coincident(g19,g18)
    c: Coincident(g20,g4)
    c: Coincident(g20,g14)
    c: Coincident(g21,g16)
    c: Coincident(g21,g17)
    c: Coincident(g22,g19)
    c: Coincident(g22,g5)
    c: DistanceY(g6,g6) = 2.5
    c: Horizontal(g5,g0)
    c: Angle(g20,g4) = 1.5708
    c: Coincident(g23,g4)
    c: Coincident(g23,g5)
    c: Coincident(g24,g3)
    c: Coincident(g24,g0)
    c: PointOnObject(g14,g23)
    c: PointOnObject(g16,g23)
    c: PointOnObject(g17,g23)
    c: PointOnObject(g19,g23)
    c: PointOnObject(g12,g24)
    c: PointOnObject(g9,g24)
    c: PointOnObject(g2,g24)
    c: Distance(g14,g16) = 5
    c: Angle(g20,g14) = 1.5708
    c: Parallel(g14,g16)
    c: Angle(g15,g14) = 1.5708
    c: Vertical(g18)
    c: DistanceY(g18,g18) = 5
    c: Parallel(g17,g19)
    c: Distance(g2,g9) = 5
    c: Parallel(g11,g2)
    c: PointOnObject(g9,g24)
    c: Parallel(g10,g12)
    c: Distance(g4) = 5
    c: Angle(g2,g3) = 1.5708
    c: Parallel(g23,g24)
    c: DistanceX(g17,g2) = 68
    c: DistanceX(g5,g7) = 53
    c: DistanceX(g7,g7) = 70
    c: Angle(g10,g9) = 1.0472
    c: Coincident(g25,g9)
    c: PointOnObject(g25,g22)
    c: Parallel(g25,g10)
    c: Coincident(g26,g5)
    c: PointOnObject(g26,g7)
    c: Parallel(g22,g26)
    c: Distance(g26,g25) = 16
    c: Coincident(g27,g10)
    c: Coincident(g27,g2)
    c: Parallel(g10,g27)
    c: Angle(g21,g17) = 2.0944
    c: Distance(g22) = 35
    c: Distance(g21) = 19
    c: Angle(g2,g8) = 1.8326
    c: DistanceX(g0,g7) = 2.5
    c: Coincident(g28,g9)
    c: PointOnObject(g28,g12)
    c: Angle(g28,g10) = 1.5708
    c: Distance(g28) = 5
    c: Distance(g16) = 25
    c: Distance(g3) = 45
FEATURE [PartDesign::Pad] Pad007  label="rib-outlines-pad"
  BaseFeature = -> Pad
  Direction = (0,0,1)
  Length = 4.5
  Length2 = 10
  Profile = -> Sketch018
  ReferenceAxis = -> Sketch018 [N_Axis]
  Suppressed = false
  Type = 0
FEATURE [PartDesign::Mirrored] Mirrored
  MirrorPlane = -> Sketch018 [V_Axis]
  Suppressed = false
  TransformMode = 0
FEATURE [PartDesign::Mirrored] Mirrored001
  MirrorPlane = -> XZ_Plane
  Suppressed = false
  TransformMode = 0
FEATURE [PartDesign::MultiTransform] MultiTransform
  BaseFeature = -> Pad007
  Originals = -> [Pad007]
  Suppressed = false
  TransformMode = 0
  Transformations = -> [Mirrored,Mirrored001]
FEATURE [Sketcher::SketchObject] Sketch019  label="grip-tape-inset"
  ArcFitTolerance = 0
  AttachmentOffset = pos=(0,0,9.5) rot=(0,0,1;0rad)
  AttachmentSupport = -> [XY_Plane]
  FullyConstrained = true
  MakeInternals = false
  MapMode = 5
  Placement = pos=(0,0,9.5) rot=(0,0,1;0rad)
  sketch-geometry (16):
    g0: LineSegment [constr] StartX=-71 StartY=85.5 StartZ=0 EndX=71 EndY=85.5 EndZ=0
    g1: LineSegment [constr] StartX=71 StartY=85.5 StartZ=0 EndX=71 EndY=-85.5 EndZ=0
    g2: LineSegment [constr] StartX=71 StartY=-85.5 StartZ=0 EndX=-71 EndY=-85.5 EndZ=0
    g3: LineSegment [constr] StartX=-71 StartY=-85.5 StartZ=0 EndX=-71 EndY=85.5 EndZ=0
    g4: LineSegment StartX=-32 StartY=84.5 StartZ=0 EndX=32 EndY=84.5 EndZ=0
    g5: LineSegment StartX=70 StartY=46.5 StartZ=0 EndX=70 EndY=-46.5 EndZ=0
    g6: LineSegment StartX=32 StartY=-84.5 StartZ=0 EndX=-32 EndY=-84.5 EndZ=0
    g7: LineSegment StartX=-70 StartY=-46.5 StartZ=0 EndX=-70 EndY=46.5 EndZ=0
    g8: ArcOfCircle CenterX=-32 CenterY=46.5 CenterZ=0 NormalX=0 NormalY=0 NormalZ=1 AngleXU=0 Radius=38 StartAngle=1.5708 EndAngle=3.14159
    g9: GeomPoint [constr] X=-70 Y=84.5 Z=0
    g10: ArcOfCircle CenterX=-32 CenterY=-46.5 CenterZ=0 NormalX=0 NormalY=0 NormalZ=1 AngleXU=0 Radius=38 StartAngle=3.14159 EndAngle=4.71239
    g11: GeomPoint [constr] X=-70 Y=-84.5 Z=0
    g12: ArcOfCircle CenterX=32 CenterY=-46.5 CenterZ=0 NormalX=0 NormalY=0 NormalZ=1 AngleXU=0 Radius=38 StartAngle=4.71239 EndAngle=6.28319
    g13: GeomPoint [constr] X=70 Y=-84.5 Z=0
    g14: ArcOfCircle CenterX=32 CenterY=46.5 CenterZ=0 NormalX=0 NormalY=0 NormalZ=1 AngleXU=0 Radius=38 StartAngle=0 EndAngle=1.5708
    g15: GeomPoint [constr] X=70 Y=84.5 Z=0
  constraints (36):
    c: Coincident(g0,g1)
    c: Coincident(g1,g2)
    c: Coincident(g2,g3)
    c: Coincident(g3,g0)
    c: Horizontal(g2)
    c: Vertical(g3)
    c: DistanceX(g0,g0) = 142
    c: DistanceY(g1,g1) = 171
    c: Symmetric(g0,g0,g-2)
    c: Symmetric(g0,g1,g-1)
    c: Horizontal(g6)
    c: Vertical(g5)
    c: DistanceX(g2,g11) = 1
    c: DistanceY(g2,g11) = 1
    c: Symmetric(g9,g11,g-1)
    c: Symmetric(g9,g15,g-2)
    c: PointOnObject(g9,g4)
    c: PointOnObject(g9,g7)
    c: Tangent(g4,g8) = 1.5708
    c: Tangent(g7,g8) = 1.5708
    c: PointOnObject(g11,g6)
    c: PointOnObject(g11,g7)
    c: Tangent(g6,g10) = 1.5708
    c: Tangent(g7,g10) = 1.5708
    c: PointOnObject(g13,g5)
    c: PointOnObject(g13,g6)
    c: Tangent(g5,g12) = 1.5708
    c: Tangent(g6,g12) = 1.5708
    c: PointOnObject(g15,g4)
    c: PointOnObject(g15,g5)
    c: Tangent(g4,g14) = 1.5708
    c: Tangent(g5,g14) = 1.5708
    c: Radius(g8) = 38
    c: Radius(g14) = 38
    c: Radius(g12) = 38
    c: Radius(g10) = 38
FEATURE [PartDesign::Pocket] Pocket  label="grip-tape-inset-pocket"
  BaseFeature = -> MultiTransform
  Direction = (0,0,-1)
  Length = 0.5
  Length2 = 5
  Profile = -> Sketch019
  ReferenceAxis = -> Sketch019 [N_Axis]
  Suppressed = false
  Type = 0
FEATURE [Sketcher::SketchObject] Sketch020  label="ribs-taper-y"
  ArcFitTolerance = 0
  AttachmentSupport = -> [YZ_Plane]
  FullyConstrained = true
  MakeInternals = false
  MapMode = 5
  Placement = pos=(0,0,0) rot=(0.57735,0.57735,0.57735;2.0944rad)
  sketch-geometry (10):
    g0: LineSegment StartX=-84 StartY=4.5 StartZ=0 EndX=-46.7137 EndY=0.197732 EndZ=0
    g1: LineSegment StartX=46.7137 StartY=0.197732 StartZ=0 EndX=84 EndY=4.5 EndZ=0
    g2: LineSegment StartX=-43.275 StartY=0 StartZ=0 EndX=43.275 EndY=0 EndZ=0
    g3: LineSegment StartX=-84 StartY=4.5 StartZ=0 EndX=-84 EndY=-7.5 EndZ=0
    g4: LineSegment StartX=-84 StartY=-7.5 StartZ=0 EndX=84 EndY=-7.5 EndZ=0
    g5: LineSegment StartX=84 StartY=-7.5 StartZ=0 EndX=84 EndY=4.5 EndZ=0
    g6: ArcOfCircle CenterX=43.275 CenterY=30 CenterZ=0 NormalX=0 NormalY=0 NormalZ=1 AngleXU=0 Radius=30 StartAngle=4.71239 EndAngle=4.82727
    g7: GeomPoint [constr] X=45 Y=0 Z=0
    g8: ArcOfCircle CenterX=-43.275 CenterY=30 CenterZ=0 NormalX=0 NormalY=0 NormalZ=1 AngleXU=0 Radius=30 StartAngle=4.59751 EndAngle=4.71239
    g9: GeomPoint [constr] X=-45 Y=0 Z=0
  constraints (24):
    c: Symmetric(g0,g1,g-2)
    c: Symmetric(g9,g7,g-2)
    c: PointOnObject(g9,g-1)
    c: DistanceY(g9,g0) = 4.5
    c: Coincident(g3,g0)
    c: Vertical(g3)
    c: Coincident(g4,g3)
    c: Horizontal(g4)
    c: Coincident(g5,g4)
    c: Coincident(g5,g1)
    c: Vertical(g5)
    c: DistanceY(g3,g3) = 12
    c: DistanceX(g0,g1) = 168
    c: DistanceX(g9,g7) = 90
    c: PointOnObject(g7,g1)
    c: PointOnObject(g7,g2)
    c: Tangent(g1,g6) = -1.5708
    c: Tangent(g2,g6) = -1.5708
    c: Radius(g6) = 30
    c: PointOnObject(g9,g0)
    c: PointOnObject(g9,g2)
    c: Tangent(g0,g8) = -1.5708
    c: Tangent(g2,g8) = -1.5708
    c: Radius(g8) = 30
FEATURE [PartDesign::Pocket] Pocket003  label="ribs-taper-y-pocket"
  BaseFeature = -> Pocket
  Direction = (-1,0,0)
  Length = 180
  Length2 = 5
  Midplane = true
  Profile = -> Sketch020
  ReferenceAxis = -> Sketch020 [N_Axis]
  Suppressed = false
  Type = 0
FEATURE [Sketcher::SketchObject] Sketch021  label="ribs-taper-x"
  ArcFitTolerance = 0
  AttachmentSupport = -> [XZ_Plane]
  FullyConstrained = true
  MakeInternals = false
  MapMode = 5
  Placement = pos=(0,0,0) rot=(1,0,0;1.5708rad)
  sketch-geometry (10):
    g0: LineSegment StartX=-71 StartY=4.5 StartZ=0 EndX=-47.5392 EndY=0.439485 EndZ=0
    g1: LineSegment StartX=-42.423 StartY=0 StartZ=0 EndX=42.423 EndY=0 EndZ=0
    g2: LineSegment StartX=47.5392 StartY=0.439485 StartZ=0 EndX=71 EndY=4.5 EndZ=0
    g3: LineSegment StartX=71 StartY=4.5 StartZ=0 EndX=71 EndY=-7.5 EndZ=0
    g4: LineSegment StartX=71 StartY=-7.5 StartZ=0 EndX=-71 EndY=-7.5 EndZ=0
    g5: LineSegment StartX=-71 StartY=-7.5 StartZ=0 EndX=-71 EndY=4.5 EndZ=0
    g6: ArcOfCircle CenterX=42.423 CenterY=30 CenterZ=0 NormalX=0 NormalY=0 NormalZ=1 AngleXU=0 Radius=30 StartAngle=4.71239 EndAngle=4.88377
    g7: GeomPoint [constr] X=45 Y=0 Z=0
    g8: ArcOfCircle CenterX=-42.423 CenterY=30 CenterZ=0 NormalX=0 NormalY=0 NormalZ=1 AngleXU=0 Radius=30 StartAngle=4.54101 EndAngle=4.71239
    g9: GeomPoint [constr] X=-45 Y=0 Z=0
  constraints (24):
    c: PointOnObject(g9,g-1)
    c: Coincident(g3,g2)
    c: Vertical(g3)
    c: Coincident(g4,g3)
    c: Horizontal(g4)
    c: Coincident(g5,g4)
    c: Coincident(g5,g0)
    c: Vertical(g5)
    c: Symmetric(g0,g2,g-2)
    c: DistanceY(g5,g5) = 12
    c: DistanceY(g9,g0) = 4.5
    c: DistanceX(g9,g7) = 90
    c: DistanceX(g0,g2) = 142
    c: Symmetric(g9,g7,g-2)
    c: PointOnObject(g7,g1)
    c: PointOnObject(g7,g2)
    c: Tangent(g1,g6) = -1.5708
    c: Tangent(g2,g6) = -1.5708
    c: Radius(g6) = 30
    c: PointOnObject(g9,g0)
    c: PointOnObject(g9,g1)
    c: Tangent(g0,g8) = -1.5708
    c: Tangent(g1,g8) = -1.5708
    c: Radius(g8) = 30
FEATURE [PartDesign::Pocket] Pocket004  label="ribs-taper-x-pocket"
  BaseFeature = -> Pocket003
  Direction = (0,1,-2e-16)
  Length = 150
  Length2 = 5
  Midplane = true
  Profile = -> Sketch021
  ReferenceAxis = -> Sketch021 [N_Axis]
  Suppressed = false
  Type = 0
FEATURE [Sketcher::SketchObject] Sketch030  label="edge-guard-profile"
  ArcFitTolerance = 0
  AttachmentOffset = pos=(0,4.5,0) rot=(0,0,1;0rad)
  FullyConstrained = true
  MakeInternals = false
  MapMode = 5
  Placement = pos=(0,-1e-15,4.5) rot=(1,0,0;1.5708rad)
  sketch-geometry (20):
    g0: LineSegment StartX=75.3284 StartY=0 StartZ=0 EndX=75.5 EndY=0 EndZ=0
    g1: LineSegment StartX=75.5 StartY=0 StartZ=0 EndX=75.5 EndY=5 EndZ=0
    g2: LineSegment StartX=75.5 StartY=5 StartZ=0 EndX=75.3284 EndY=5 EndZ=0
    g3: LineSegment StartX=75.3284 StartY=5 StartZ=0 EndX=63.5 EndY=3 EndZ=0
    g4: LineSegment StartX=75.3284 StartY=0 StartZ=0 EndX=63.5 EndY=2 EndZ=0
    g5: LineSegment StartX=63.5 StartY=3 StartZ=0 EndX=63.5 EndY=5.2 EndZ=0
    g6: LineSegment StartX=63.5 StartY=5.2 StartZ=0 EndX=74.6663 EndY=7.08804 EndZ=0
    g7: LineSegment StartX=76 StartY=7.2 StartZ=0 EndX=76.5 EndY=7.2 EndZ=0
    g8: LineSegment StartX=78.5 StartY=5.2 StartZ=0 EndX=78.5 EndY=-1.8 EndZ=0
    g9: LineSegment StartX=76.5 StartY=-3.8 StartZ=0 EndX=76 EndY=-3.8 EndZ=0
    g10: LineSegment StartX=74.6663 StartY=-3.68804 StartZ=0 EndX=63.5 EndY=-1.8 EndZ=0
    g11: LineSegment StartX=63.5 StartY=-1.8 StartZ=0 EndX=63.5 EndY=2 EndZ=0
    g12: ArcOfCircle CenterX=76.5 CenterY=5.2 CenterZ=0 NormalX=0 NormalY=0 NormalZ=1 AngleXU=0 Radius=2 StartAngle=0 EndAngle=1.5708
    g13: GeomPoint [constr] X=78.5 Y=7.2 Z=0
    g14: ArcOfCircle CenterX=76.5 CenterY=-1.8 CenterZ=0 NormalX=0 NormalY=0 NormalZ=1 AngleXU=0 Radius=2 StartAngle=4.71239 EndAngle=6.28319
    g15: GeomPoint [constr] X=78.5 Y=-3.8 Z=0
    g16: ArcOfCircle CenterX=76 CenterY=4.2 CenterZ=0 NormalX=0 NormalY=0 NormalZ=1 AngleXU=0 Radius=8 StartAngle=4.54489 EndAngle=4.71239
    g17: GeomPoint [constr] X=75.3284 Y=-3.8 Z=0
    g18: ArcOfCircle CenterX=76 CenterY=-0.8 CenterZ=0 NormalX=0 NormalY=0 NormalZ=1 AngleXU=0 Radius=8 StartAngle=1.5708 EndAngle=1.7383
    g19: GeomPoint [constr] X=75.3284 Y=7.2 Z=0
  constraints (53):
    c: PointOnObject(g0,g-1)
    c: PointOnObject(g0,g-1)
    c: Coincident(g1,g0)
    c: Vertical(g1)
    c: Coincident(g2,g1)
    c: Horizontal(g2)
    c: DistanceY(g1,g1) = 5
    c: Coincident(g4,g0)
    c: Vertical(g0,g2)
    c: Vertical(g2,g3)
    c: Vertical(g3,g4)
    c: Coincident(g5,g3)
    c: Vertical(g5)
    c: Coincident(g6,g5)
    c: Horizontal(g7)
    c: Vertical(g8)
    c: Horizontal(g9)
    c: Coincident(g11,g10)
    c: Coincident(g11,g4)
    c: Vertical(g11)
    c: Parallel(g6,g3)
    c: Vertical(g19,g2)
    c: Vertical(g17,g0)
    c: Parallel(g4,g10)
    c: DistanceX(g0,g15) = 3
    c: DistanceX(g-1,g0) = 75.5
    c: PointOnObject(g13,g7)
    c: PointOnObject(g13,g8)
    c: Tangent(g7,g12) = 1.5708
    c: Tangent(g8,g12) = 1.5708
    c: Radius(g12) = 2
    c: PointOnObject(g15,g8)
    c: PointOnObject(g15,g9)
    c: Tangent(g8,g14) = 1.5708
    c: Tangent(g9,g14) = 1.5708
    c: Radius(g14) = 2
    c: PointOnObject(g17,g9)
    c: PointOnObject(g17,g10)
    c: Tangent(g9,g16) = 1.5708
    c: Tangent(g10,g16) = 1.5708
    c: Radius(g16) = 8
    c: PointOnObject(g19,g6)
    c: PointOnObject(g19,g7)
    c: Tangent(g6,g18) = 1.5708
    c: Tangent(g7,g18) = 1.5708
    c: Radius(g18) = 8
    c: DistanceX(g5,g8) = 15
    c: DistanceY(g5,g7) = 2
    c: DistanceY(g9,g10) = 2
    c: DistanceX(g7,g8) = 2.5
    c: DistanceY(g15,g13) = 11
    c: DistanceY(g10,g-1) = 1.8
    c: DistanceY(g5,g5) = 2.2
FEATURE [Sketcher::SketchObject] Sketch031  label="edge-guard-sweep-path"
  ArcFitTolerance = 0
  FullyConstrained = true
  MakeInternals = false
  MapMode = 5
  sketch-geometry (12):
    g0: LineSegment StartX=-41 StartY=85.5 StartZ=0 EndX=41 EndY=85.5 EndZ=0
    g1: LineSegment StartX=71 StartY=55.5 StartZ=0 EndX=71 EndY=-55.5 EndZ=0
    g2: LineSegment StartX=41 StartY=-85.5 StartZ=0 EndX=-41 EndY=-85.5 EndZ=0
    g3: LineSegment StartX=-71 StartY=-55.5 StartZ=0 EndX=-71 EndY=55.5 EndZ=0
    g4: ArcOfCircle CenterX=-41 CenterY=55.5 CenterZ=0 NormalX=0 NormalY=0 NormalZ=1 AngleXU=0 Radius=30 StartAngle=1.5708 EndAngle=3.14159
    g5: GeomPoint [constr] X=-71 Y=85.5 Z=0
    g6: ArcOfCircle CenterX=41 CenterY=55.5 CenterZ=0 NormalX=0 NormalY=0 NormalZ=1 AngleXU=0 Radius=30 StartAngle=0 EndAngle=1.5708
    g7: GeomPoint [constr] X=71 Y=85.5 Z=0
    g8: ArcOfCircle CenterX=-41 CenterY=-55.5 CenterZ=0 NormalX=0 NormalY=0 NormalZ=1 AngleXU=0 Radius=30 StartAngle=3.14159 EndAngle=4.71239
    g9: GeomPoint [constr] X=-71 Y=-85.5 Z=0
    g10: ArcOfCircle CenterX=41 CenterY=-55.5 CenterZ=0 NormalX=0 NormalY=0 NormalZ=1 AngleXU=0 Radius=30 StartAngle=4.71239 EndAngle=6.28319
    g11: GeomPoint [constr] X=71 Y=-85.5 Z=0
  constraints (26):
    c: Horizontal(g0)
    c: Horizontal(g2)
    c: Vertical(g1)
    c: Vertical(g3)
    c: PointOnObject(g5,g0)
    c: PointOnObject(g5,g3)
    c: Tangent(g0,g4) = 1.5708
    c: Tangent(g3,g4) = 1.5708
    c: PointOnObject(g7,g0)
    c: PointOnObject(g7,g1)
    c: Tangent(g0,g6) = 1.5708
    c: Tangent(g1,g6) = 1.5708
    c: PointOnObject(g9,g2)
    c: Tangent(g2,g8) = 1.5708
    c: Tangent(g3,g8) = 1.5708
    c: PointOnObject(g11,g1)
    c: Tangent(g1,g10) = 1.5708
    c: Tangent(g2,g10) = 1.5708
    c: Symmetric(g9,g11,g-2)
    c: Symmetric(g9,g5,g-1)
    c: DistanceX(g5,g7) = 142
    c: DistanceY(g11,g7) = 171
    c: Radius(g6) = 30
    c: Radius(g4) = 30
    c: Radius(g10) = 30
    c: Radius(g8) = 30
FEATURE [Part::Sweep] Sweep  label="edge-guard"
  Frenet = false
  Placement = pos=(0,0,0) rot=(0,0,1;1.309rad)
  Sections = -> [Sketch030]
  Solid = true
  Spine = -> Sketch031 [Edge7,Edge8,Edge6,Edge5,Edge4,Edge3,Edge2,Edge1]
  Transition = 1
FEATURE [PartDesign::FeatureBase] BaseFeature
  BaseFeature = -> Cut001
  Suppressed = false
FEATURE [Sketcher::SketchObject] Sketch032  label="grind-spline-outline"
  ArcFitTolerance = 0
  AttachmentOffset = pos=(49.3,-13,27.5) rot=(0,0,1;0.418879rad)
  AttachmentSupport = -> [YZ_Plane007]
  FullyConstrained = true
  MakeInternals = false
  MapMode = 5
  Placement = pos=(27.5,49.3,-13) rot=(0.642595,0.417306,0.642595;2.35092rad)
  sketch-geometry (4):
    g0: LineSegment StartX=3 StartY=0 StartZ=0 EndX=3 EndY=-24 EndZ=0
    g1: ArcOfCircle CenterX=0 CenterY=0 CenterZ=0 NormalX=0 NormalY=0 NormalZ=1 AngleXU=0 Radius=3 StartAngle=0 EndAngle=1.5708
    g2: ArcOfCircle CenterX=0 CenterY=-24 CenterZ=0 NormalX=0 NormalY=0 NormalZ=1 AngleXU=0 Radius=3 StartAngle=4.71239 EndAngle=6.28319
    g3: LineSegment StartX=2e-16 StartY=3 StartZ=0 EndX=-6e-16 EndY=-27 EndZ=0
  constraints (13):
    c: PointOnObject(g0,g-1)
    c: Vertical(g0)
    c: Coincident(g1,g-1)
    c: Coincident(g1,g0)
    c: PointOnObject(g1,g-2)
    c: PointOnObject(g2,g-2)
    c: Coincident(g2,g0)
    c: PointOnObject(g2,g-2)
    c: Horizontal(g2,g0)
    c: DistanceX(g1,g0) = 3
    c: DistanceY(g2,g1) = 30
    c: Coincident(g3,g1)
    c: Coincident(g3,g2)
FEATURE [PartDesign::Revolution] Revolution  label="grind-spline-revolution"
  Angle = 180
  Angle2 = 60
  Axis = (0,-0.406737,0.913545)
  Base = (27.5,49.3,-13)
  BaseFeature = -> BaseFeature
  Profile = -> Sketch032
  ReferenceAxis = -> Sketch032 [V_Axis]
  Reversed = true
  Suppressed = false
  Type = 0
FEATURE [PartDesign::Mirrored] Mirrored003  label="grind-spline-mirror-y"
  MirrorPlane = -> XZ_Plane007
  Suppressed = false
  TransformMode = 0
FEATURE [PartDesign::Mirrored] Mirrored004  label="grind-spline-mirror-x"
  MirrorPlane = -> YZ_Plane007
  Suppressed = false
  TransformMode = 0
FEATURE [PartDesign::MultiTransform] MultiTransform001  label="grind-spline-mirroring"
  BaseFeature = -> Revolution
  Originals = -> [Revolution]
  Suppressed = false
  TransformMode = 0
  Transformations = -> [Mirrored003,Mirrored004]
FEATURE [PartDesign::Body] Body006  label="chassis"
  AllowCompound = false
  BaseFeature = -> Cut001
  Group = -> [BaseFeature,Sketch032,Revolution,MultiTransform001,Mirrored003,Mirrored004]
  Origin = -> Origin007
  Tip = -> MultiTransform001
FEATURE [Sketcher::SketchObject] Sketch035
  ArcFitTolerance = 0
  AttachmentSupport = -> [YZ_Plane008]
  FullyConstrained = true
  MakeInternals = false
  MapMode = 5
  Placement = pos=(0,0,0) rot=(0.57735,0.57735,0.57735;2.0944rad)
  sketch-geometry (2):
    g0: Circle CenterX=0 CenterY=0 CenterZ=0 NormalX=0 NormalY=0 NormalZ=1 AngleXU=0 Radius=10
    g1: Circle CenterX=0 CenterY=0 CenterZ=0 NormalX=0 NormalY=0 NormalZ=1 AngleXU=0 Radius=11
  constraints (4):
    c: Coincident(g0,g-1)
    c: Coincident(g1,g0)
    c: Diameter(g1) = 22
    c: Diameter(g0) = 20
FEATURE [PartDesign::Pad] Pad013
  Direction = (1,0,0)
  Length = 6
  Length2 = 10
  Placement = pos=(0,0,0) rot=(1,1,1;2.0944rad)
  Profile = -> Sketch035
  ReferenceAxis = -> Sketch035 [N_Axis]
  Suppressed = false
  Type = 0
FEATURE [PartDesign::Body] Body007  label="bearing-outer-front-left"
  AllowCompound = false
  Group = -> [Sketch035,Pad013]
  Origin = -> Origin008
  Placement = pos=(6,-51,-44) rot=(0,0,1;0rad)
  Tip = -> Pad013
FEATURE [Part::Mirroring] Part__Mirroring003  label="bearing-outer-back-left"
  Base = (9,-3.8147e-06,-44)
  Normal = (0,1,-1.19209e-07)
  Source = -> Body007
FEATURE [Part::Mirroring] Part__Mirroring004  label="bearing-outer-back-right"
  Base = (-3.8147e-06,51,-44)
  Normal = (1,0,-1.19209e-07)
  Source = -> Part__Mirroring003
FEATURE [Part::Mirroring] Part__Mirroring005  label="bearing-outer-front-right"
  Base = (0,0,0)
  Normal = (1,0,0)
  Source = -> Body007
FEATURE [Sketcher::SketchObject] Sketch036
  ArcFitTolerance = 0
  AttachmentSupport = -> [XY_Plane009]
  FullyConstrained = true
  MakeInternals = false
  MapMode = 5
  sketch-geometry (4):
    g0: LineSegment StartX=-24.5 StartY=6 StartZ=0 EndX=-12.5 EndY=6 EndZ=0
    g1: LineSegment StartX=-12.5 StartY=6 StartZ=0 EndX=-12.5 EndY=5.5 EndZ=0
    g2: LineSegment StartX=-12.5 StartY=5.5 StartZ=0 EndX=-24.5 EndY=5.5 EndZ=0
    g3: LineSegment StartX=-24.5 StartY=5.5 StartZ=0 EndX=-24.5 EndY=6 EndZ=0
  constraints (12):
    c: Coincident(g0,g1)
    c: Coincident(g1,g2)
    c: Coincident(g2,g3)
    c: Coincident(g3,g0)
    c: Horizontal(g2)
    c: Vertical(g1)
    c: Vertical(g3)
    c: DistanceY(g-1,g0) = 6
    c: DistanceX(g0,g0) = 12
    c: DistanceY(g1,g1) = 0.5
    c: Horizontal(g0,g0)
    c: DistanceX(g0,g-1) = 24.5
FEATURE [PartDesign::Revolution] Revolution001
  Angle = 360
  Angle2 = 60
  Axis = (1,0,0)
  Base = (0,0,0)
  Profile = -> Sketch036
  ReferenceAxis = -> X_Axis009
  Suppressed = false
  Type = 0
FEATURE [PartDesign::Body] Body008  label="washer"
  AllowCompound = false
  Group = -> [Sketch036,Revolution001]
  Origin = -> Origin009
  Placement = pos=(0,-51,-44) rot=(0,0,1;0rad)
  Tip = -> Revolution001
FEATURE [Part::Mirroring] Part__Mirroring006  label="washer (Mirror #7)"
  Base = (0,0,0)
  Normal = (1,0,0)
  Source = -> Body008
FEATURE [Part::Mirroring] Part__Mirroring007  label="washer (Mirror #8)"
  Base = (0,0,0)
  Normal = (0,1,0)
  Source = -> Part__Mirroring006
FEATURE [Part::Mirroring] Part__Mirroring008  label="washer (Mirror #9)"
  Base = (0,0,0)
  Normal = (1,0,0)
  Source = -> Part__Mirroring007
FEATURE [PartDesign::Revolution] Revolution002
  Angle = 360
  Angle2 = 60
  Axis = (1,0,0)
  Base = (0,51,-44)
  Placement = pos=(0,51,-44) rot=(0,0,1;0rad)
  Profile = -> Sketch012
  ReferenceAxis = -> Sketch012 [H_Axis]
  Suppressed = false
  Type = 0
FEATURE [Sketcher::SketchObject] Sketch037
  ArcFitTolerance = 0
  AttachmentOffset = pos=(51,-44,0) rot=(0,0,1;0rad)
  AttachmentSupport = -> [YZ_Plane010]
  FullyConstrained = false
  MakeInternals = false
  MapMode = 5
  Placement = pos=(0,51,-44) rot=(0.57735,0.57735,0.57735;2.0944rad)
  sketch-geometry (26):
    g0: Circle [constr] CenterX=0 CenterY=0 CenterZ=0 NormalX=0 NormalY=0 NormalZ=1 AngleXU=0 Radius=15.7365
    g1: Circle [constr] CenterX=0 CenterY=0 CenterZ=0 NormalX=0 NormalY=0 NormalZ=1 AngleXU=0 Radius=13.1538
    g2: ArcOfCircle CenterX=0 CenterY=0 CenterZ=0 NormalX=0 NormalY=0 NormalZ=1 AngleXU=0 Radius=15.7365 StartAngle=0.908509 EndAngle=1.14653
    g3: ArcOfCircle CenterX=0 CenterY=0 CenterZ=0 NormalX=0 NormalY=0 NormalZ=1 AngleXU=0 Radius=13.1538 StartAngle=0.908509 EndAngle=1.14653
    g4: LineSegment [constr] StartX=6.47794 StartY=14.3413 StartZ=0 EndX=0 EndY=0 EndZ=0
    g5: LineSegment [constr] StartX=9.67673 StartY=12.4096 StartZ=0 EndX=0 EndY=0 EndZ=0
    g6: LineSegment StartX=6.47794 StartY=14.3413 StartZ=0 EndX=5.41477 EndY=11.9876 EndZ=0
    g7: LineSegment StartX=9.67673 StartY=12.4096 StartZ=0 EndX=8.08858 EndY=10.3729 EndZ=0
    g8: ArcOfCircle CenterX=0 CenterY=0 CenterZ=0 NormalX=0 NormalY=0 NormalZ=1 AngleXU=0 Radius=15.7365 StartAngle=0.627933 EndAngle=0.735551
    g9: ArcOfCircle CenterX=0 CenterY=0 CenterZ=0 NormalX=0 NormalY=0 NormalZ=1 AngleXU=0 Radius=13.1538 StartAngle=0.627933 EndAngle=0.735551
    g10: LineSegment [constr] StartX=11.668 StartY=10.5591 StartZ=0 EndX=0 EndY=0 EndZ=0
    g11: LineSegment [constr] StartX=12.7347 StartY=9.24478 StartZ=0 EndX=0 EndY=0 EndZ=0
    g12: LineSegment StartX=11.668 StartY=10.5591 StartZ=0 EndX=9.75305 EndY=8.82616 EndZ=0
    g13: LineSegment StartX=12.7347 StartY=9.24478 StartZ=0 EndX=10.6446 EndY=7.72751 EndZ=0
    g14: ArcOfCircle CenterX=0 CenterY=0 CenterZ=0 NormalX=0 NormalY=0 NormalZ=1 AngleXU=0 Radius=15.7365 StartAngle=1.32792 EndAngle=1.44265
    g15: ArcOfCircle CenterX=0 CenterY=0 CenterZ=0 NormalX=0 NormalY=0 NormalZ=1 AngleXU=0 Radius=13.1538 StartAngle=1.32792 EndAngle=1.44265
    g16: LineSegment [constr] StartX=2.01101 StartY=15.6075 StartZ=0 EndX=0 EndY=0 EndZ=0
    g17: LineSegment [constr] StartX=3.78452 StartY=15.2747 StartZ=0 EndX=0 EndY=0 EndZ=0
    g18: LineSegment StartX=2.01101 StartY=15.6075 StartZ=0 EndX=1.68096 EndY=13.046 EndZ=0
    g19: LineSegment StartX=3.78452 StartY=15.2747 StartZ=0 EndX=3.1634 EndY=12.7678 EndZ=0
    g20: ArcOfCircle CenterX=0 CenterY=0 CenterZ=0 NormalX=0 NormalY=0 NormalZ=1 AngleXU=0 Radius=15.7365 StartAngle=0.197299 EndAngle=0.428307
    g21: ArcOfCircle CenterX=0 CenterY=0 CenterZ=0 NormalX=0 NormalY=0 NormalZ=1 AngleXU=0 Radius=13.1538 StartAngle=0.197299 EndAngle=0.428307
    g22: LineSegment [constr] StartX=14.315 StartY=6.53586 StartZ=0 EndX=0 EndY=0 EndZ=0
    g23: LineSegment [constr] StartX=15.4312 StartY=3.08469 StartZ=0 EndX=0 EndY=0 EndZ=0
    g24: LineSegment StartX=14.315 StartY=6.53586 StartZ=0 EndX=11.9656 EndY=5.46319 EndZ=0
    g25: LineSegment StartX=15.4312 StartY=3.08469 StartZ=0 EndX=12.8986 EndY=2.57843 EndZ=0
  constraints (58):
    c: Coincident(g0,g-1)
    c: Coincident(g1,g0)
    c: Coincident(g2,g0)
    c: PointOnObject(g2,g0)
    c: Coincident(g3,g2)
    c: PointOnObject(g3,g1)
    c: Coincident(g4,g2)
    c: Coincident(g4,g2)
    c: Coincident(g5,g2)
    c: PointOnObject(g3,g4)
    c: PointOnObject(g3,g5)
    c: Coincident(g6,g2)
    c: Coincident(g6,g3)
    c: Coincident(g7,g2)
    c: Coincident(g7,g3)
    c: Coincident(g8,g2)
    c: PointOnObject(g8,g0)
    c: Coincident(g9,g2)
    c: PointOnObject(g9,g1)
    c: Coincident(g10,g8)
    c: Coincident(g10,g2)
    c: Coincident(g11,g8)
    c: Coincident(g11,g5)
    c: PointOnObject(g9,g10)
    c: PointOnObject(g9,g11)
    c: Coincident(g12,g8)
    c: Coincident(g12,g9)
    c: Coincident(g13,g8)
    c: Coincident(g13,g9)
    c: Coincident(g14,g2)
    c: PointOnObject(g14,g0)
    c: Coincident(g15,g2)
    c: PointOnObject(g15,g1)
    c: Coincident(g16,g14)
    c: Coincident(g16,g2)
    c: Coincident(g17,g14)
    c: Coincident(g17,g5)
    c: PointOnObject(g15,g16)
    c: PointOnObject(g15,g17)
    c: Coincident(g18,g14)
    c: Coincident(g18,g15)
    c: Coincident(g19,g14)
    c: Coincident(g19,g15)
    c: Coincident(g5,g2)
    c: Coincident(g20,g2)
    c: PointOnObject(g20,g0)
    c: Coincident(g21,g2)
    c: PointOnObject(g21,g1)
    c: Coincident(g22,g20)
    c: Coincident(g22,g2)
    c: Coincident(g23,g20)
    c: Coincident(g23,g2)
    c: PointOnObject(g21,g22)
    c: PointOnObject(g21,g23)
    c: Coincident(g24,g20)
    c: Coincident(g24,g21)
    c: Coincident(g25,g20)
    c: Coincident(g25,g21)
FEATURE [PartDesign::Pocket] Pocket008
  BaseFeature = -> Revolution002
  Direction = (-1,0,0)
  Length = 50
  Length2 = 5
  Midplane = true
  Placement = pos=(0,51,-44) rot=(0,0,1;0rad)
  Profile = -> Sketch037
  ReferenceAxis = -> Sketch037 [N_Axis]
  Suppressed = false
  Type = 0
FEATURE [PartDesign::Mirrored] Mirrored007
  MirrorPlane = -> Sketch037 [V_Axis]
  Placement = pos=(0,51,-44) rot=(0,0,1;0rad)
  Suppressed = false
  TransformMode = 0
FEATURE [PartDesign::Mirrored] Mirrored008
  MirrorPlane = -> Sketch037 [H_Axis]
  Placement = pos=(0,51,-44) rot=(0,0,1;0rad)
  Suppressed = false
  TransformMode = 0
FEATURE [PartDesign::MultiTransform] MultiTransform002
  BaseFeature = -> Pocket008
  Originals = -> [Pocket008]
  Placement = pos=(0,51,-44) rot=(0,0,1;0rad)
  Suppressed = false
  TransformMode = 0
  Transformations = -> [Mirrored007,Mirrored008]
FEATURE [PartDesign::Body] Body009  label="wheel-inner-back"
  AllowCompound = false
  Group = -> [Sketch012,Revolution002,Sketch037,Pocket008,MultiTransform002,Mirrored007,Mirrored008]
  Origin = -> Origin010
  Tip = -> MultiTransform002
FEATURE [Part::Mirroring] Part__Mirroring009  label="wheel-inner-front"
  Base = (0,-3.8147e-06,-44)
  Normal = (0,1,-1.19209e-07)
  Source = -> Body009
FEATURE [Sketcher::SketchObject] Sketch038
  ArcFitTolerance = 0
  AttachmentSupport = -> [YZ_Plane011]
  FullyConstrained = true
  MakeInternals = false
  MapMode = 5
  Placement = pos=(0,0,0) rot=(0.57735,0.57735,0.57735;2.0944rad)
  sketch-geometry (2):
    g0: Circle CenterX=0 CenterY=0 CenterZ=0 NormalX=0 NormalY=0 NormalZ=1 AngleXU=0 Radius=10
    g1: Circle CenterX=0 CenterY=0 CenterZ=0 NormalX=0 NormalY=0 NormalZ=1 AngleXU=0 Radius=6
  constraints (4):
    c: Coincident(g0,g-1)
    c: Coincident(g1,g0)
    c: Diameter(g0) = 20
    c: Diameter(g1) = 12
FEATURE [PartDesign::Pad] Pad014
  Direction = (1,0,0)
  Length = 2
  Length2 = 10
  Placement = pos=(0,0,0) rot=(1,1,1;2.0944rad)
  Profile = -> Sketch038
  ReferenceAxis = -> Sketch038 [N_Axis]
  Suppressed = false
  Type = 0
FEATURE [PartDesign::Body] Body010  label="bearing-inner-back-left"
  AllowCompound = false
  Group = -> [Sketch038,Pad014]
  Origin = -> Origin011
  Placement = pos=(10,51,-44) rot=(0,0,1;0rad)
  Tip = -> Pad014
FEATURE [Part::Mirroring] Part__Mirroring010  label="bearing-inner-front-left"
  Base = (11,-3.8147e-06,-44)
  Normal = (0,1,-1.19209e-07)
  Source = -> Body010
FEATURE [Part::Mirroring] Part__Mirroring011  label="bearing-inner-front-right"
  Base = (0,0,0)
  Normal = (1,0,0)
  Source = -> Part__Mirroring010
FEATURE [Part::Mirroring] Part__Mirroring012  label="bearing-inner-back-right"
  Base = (0,0,0)
  Normal = (1,0,0)
  Source = -> Body010
FEATURE [Sketcher::SketchObject] Sketch042  label="deck-rails"
  ArcFitTolerance = 0
  AttachmentOffset = pos=(0,0,22.5) rot=(0,0,1;0rad)
  AttachmentSupport = -> [XY_Plane012]
  FullyConstrained = true
  MakeInternals = false
  MapMode = 5
  Placement = pos=(0,0,22.5) rot=(0,0,1;0rad)
  expr: Constraints[0] = Spreadsheet.railLengthNegYLong
  expr: Constraints[10] = Spreadsheet.railtruckclearance
  expr: Constraints[12] = Spreadsheet.raildiameter / 2
  expr: Constraints[14] = Spreadsheet.railLengthNegYLong
  sketch-geometry (9):
    g0: LineSegment StartX=33 StartY=-95 StartZ=0 EndX=33 EndY=42.25 EndZ=0
    g1: LineSegment [constr] StartX=-30 StartY=62.5 StartZ=0 EndX=30 EndY=62.5 EndZ=0
    g2: LineSegment [constr] StartX=30 StartY=62.5 StartZ=0 EndX=30 EndY=-62.5 EndZ=0
    g3: LineSegment [constr] StartX=30 StartY=-62.5 StartZ=0 EndX=-30 EndY=-62.5 EndZ=0
    g4: LineSegment [constr] StartX=-30 StartY=-62.5 StartZ=0 EndX=-30 EndY=62.5 EndZ=0
    g5: LineSegment StartX=-33 StartY=42.25 StartZ=0 EndX=-33 EndY=-95 EndZ=0
    g6: LineSegment StartX=-20.25 StartY=55 StartZ=0 EndX=20.25 EndY=55 EndZ=0
    g7: ArcOfCircle CenterX=-20.25 CenterY=42.25 CenterZ=0 NormalX=0 NormalY=0 NormalZ=1 AngleXU=0 Radius=12.75 StartAngle=1.5708 EndAngle=3.14159
    g8: ArcOfCircle CenterX=20.25 CenterY=42.25 CenterZ=0 NormalX=0 NormalY=0 NormalZ=1 AngleXU=0 Radius=12.75 StartAngle=6.49422e-11 EndAngle=1.5708
  constraints (24):
    c: DistanceY(g0,g-1) = 95
    c: Vertical(g0)
    c: Coincident(g1,g2)
    c: Coincident(g2,g3)
    c: Coincident(g3,g4)
    c: Coincident(g4,g1)
    c: Horizontal(g3)
    c: Vertical(g4)
    c: Symmetric(g1,g1,g-2)
    c: Symmetric(g1,g2,g-1)
    c: DistanceX(g1,g1) = 60
    c: DistanceY(g4,g4) = 125
    c: DistanceX(g2,g0) = 3
    c: Vertical(g5)
    c: DistanceY(g5,g-1) = 95
    c: Horizontal(g6)
    c: Tangent(g8,g6) = 1.5708
    c: Tangent(g8,g0) = -1.5708
    c: Tangent(g7,g6) = 1.5708
    c: Tangent(g7,g5) = -1.5708
    c: DistanceX(g5,g3) = 3
    c: Radius(g7) = 12.75
    c: Equal(g7,g8)
    c: DistanceY(g-1,g6) = 55
FEATURE [Sketcher::SketchObject] Sketch043  label="truck-rails-long"
  ArcFitTolerance = 0
  AttachmentOffset = pos=(0,0,33) rot=(0,0,1;0rad)
  AttachmentSupport = -> [YZ_Plane012]
  FullyConstrained = true
  MakeInternals = false
  MapMode = 5
  Placement = pos=(33,0,0) rot=(0.57735,0.57735,0.57735;2.0944rad)
  expr: .AttachmentOffset.Base.z = Spreadsheet.railtruckclearance / 2 + Spreadsheet.raildiameter / 2
  expr: Constraints[10] = Spreadsheet.railLengthNegYLong
  expr: Constraints[1] = Spreadsheet.railLengthPosY
  expr: Constraints[5] = Spreadsheet.raildiameter / 2
  sketch-geometry (4):
    g0: LineSegment StartX=-95 StartY=-3 StartZ=0 EndX=58 EndY=-3 EndZ=0
    g1: ArcOfCircle CenterX=-95 CenterY=9.75 CenterZ=0 NormalX=0 NormalY=0 NormalZ=1 AngleXU=0 Radius=12.75 StartAngle=1.5708 EndAngle=4.71239
    g2: LineSegment StartX=28 StartY=-19 StartZ=0 EndX=58 EndY=-19 EndZ=0
    g3: ArcOfCircle CenterX=58 CenterY=-11 CenterZ=0 NormalX=0 NormalY=0 NormalZ=1 AngleXU=0 Radius=8 StartAngle=4.71239 EndAngle=7.85398
  constraints (13):
    c: Horizontal(g0)
    c: DistanceX(g-1,g0) = 58
    c: Coincident(g1,g0)
    c: Vertical(g0,g1)
    c: Vertical(g1,g1)
    c: DistanceY(g0,g-1) = 3
    c: Horizontal(g2)
    c: Tangent(g3,g0) = 1.5708
    c: Tangent(g3,g2) = -1.5708
    c: DistanceY(g2,g0) = 16
    c: DistanceX(g1,g-1) = 95
    c: DistanceX(g-1,g2) = 28
    c: DistanceY(g0,g1) = 25.5
FEATURE [Sketcher::SketchObject] Sketch045  label="rail-profile"
  ArcFitTolerance = 0
  AttachmentSupport = -> [Sketch042]
  FullyConstrained = true
  MakeInternals = false
  MapMode = 7
  Placement = pos=(33,-95,22.5) rot=(1,0,0;1.5708rad)
  expr: Constraints[1] = Spreadsheet.raildiameter
  sketch-geometry (1):
    g0: Circle CenterX=0 CenterY=0 CenterZ=0 NormalX=0 NormalY=0 NormalZ=1 AngleXU=0 Radius=3
  constraints (2):
    c: Coincident(g0,g-1)
    c: Diameter(g0) = 6
FEATURE [Sketcher::SketchObject] Sketch048  label="bolt-holes"
  ArcFitTolerance = 0
  AttachmentOffset = pos=(0,0,9) rot=(0,0,1;0rad)
  AttachmentSupport = -> [XY_Plane]
  FullyConstrained = true
  MakeInternals = false
  MapMode = 5
  Placement = pos=(0,0,9) rot=(0,0,1;0rad)
  sketch-geometry (4):
    g0: Circle CenterX=-31.25 CenterY=9 CenterZ=0 NormalX=0 NormalY=0 NormalZ=1 AngleXU=0 Radius=4
    g1: Circle CenterX=31.25 CenterY=9 CenterZ=0 NormalX=0 NormalY=0 NormalZ=1 AngleXU=0 Radius=4
    g2: Circle CenterX=-31.25 CenterY=-9 CenterZ=0 NormalX=0 NormalY=0 NormalZ=1 AngleXU=0 Radius=4
    g3: Circle CenterX=31.25 CenterY=-9 CenterZ=0 NormalX=0 NormalY=0 NormalZ=1 AngleXU=0 Radius=4
  constraints (9):
    c: Symmetric(g0,g1,g-2)
    c: Symmetric(g2,g3,g-2)
    c: Symmetric(g3,g1,g-1)
    c: DistanceY(g3,g1) = 18
    c: DistanceX(g2,g3) = 62.5
    c: Diameter(g1) = 8
    c: Diameter(g0) = 8
    c: Diameter(g3) = 8
    c: Diameter(g2) = 8
FEATURE [PartDesign::Pocket] Pocket011  label="bolt-holes-pocket"
  BaseFeature = -> Pocket004
  Direction = (0,0,-1)
  Length = 15
  Length2 = 5
  Profile = -> Sketch048
  ReferenceAxis = -> Sketch048 [N_Axis]
  Suppressed = false
  Type = 0
FEATURE [PartDesign::Chamfer] Chamfer
  Angle = 45
  Base = -> Pocket011 [Edge350,Edge352,Edge351,Edge349]
  BaseFeature = -> Pocket011
  ChamferType = 0
  FlipDirection = false
  Size = 1
  Size2 = 1
  SupportTransform = false
  Suppressed = false
  UseAllEdges = false
FEATURE [PartDesign::Body] Body  label="deck"
  AllowCompound = false
  Group = -> [Sketch,Pad,Sketch018,Pad007,MultiTransform,Mirrored,Mirrored001,Sketch019,Pocket,Sketch020,Pocket003,Sketch021,Pocket004,Sketch048,Pocket011,Chamfer]
  Origin = -> Origin
  Placement = pos=(0,0,0) rot=(0,0,1;1.309rad)
  Tip = -> Chamfer
FEATURE [Spreadsheet::Sheet] Spreadsheet
  cells = A1='Rail diameter; B1(raildiameter)==6 mm; A2='Rail truck clearance; B2(railtruckclearance)==6 cm; A3='Deck Z clearance; B3(raildeckclearance)==15 mm; A4='Rail catch clearance; B4(railcatchclearance)==1.5 cm; A5='Catch thickness; B5(catchthickness)==1.25 cm; A6='Rail length neg Y long; B6(railLengthNegYLong)==9.5 cm; A7='Rail length neg Y short; B7(railLengthNegYShort)==8 cm; A8='Rail hole tolerance; B8(railholetolerance)==0.6 mm; A9='Catch pre-tension angle; B9(catchPretensionAngle)==10 deg; A10='Rail length pos Y; B10(railLengthPosY)==5.8 cm; A11='Rail final segments length; B11(railFinalSegmentsLength)==12 cm; A12='Rail deck extension; B12(railDeckExtension)==4.5 cm
FEATURE [Sketcher::SketchObject] Sketch070  label="rail-bend-guide"
  ArcFitTolerance = 0
  AttachmentSupport = -> [XY_Plane012]
  FullyConstrained = true
  MakeInternals = false
  MapMode = 5
  expr: Constraints[11] = Spreadsheet.railFinalSegmentsLength
  expr: Constraints[12] = Spreadsheet.railLengthNegYShort + Spreadsheet.railDeckExtension
  expr: Constraints[13] = (Spreadsheet.raildeckclearance + Spreadsheet.raildiameter) * pi * 0.5
  expr: Constraints[15] = Spreadsheet.railLengthNegYShort + Spreadsheet.railLengthPosY
  expr: Constraints[16] = (Spreadsheet.railcatchclearance + Spreadsheet.raildiameter) * pi * 0.5
  expr: Constraints[17] = Spreadsheet.railFinalSegmentsLength
  expr: Constraints[1] = (Spreadsheet.railtruckclearance + Spreadsheet.raildiameter) * pi * 0.5
  expr: Constraints[3] = Spreadsheet.railLengthNegYLong + Spreadsheet.railDeckExtension
  expr: Constraints[5] = (Spreadsheet.raildeckclearance + Spreadsheet.raildiameter) * pi * 0.5
  expr: Constraints[7] = Spreadsheet.railLengthNegYLong + Spreadsheet.railLengthPosY
  expr: Constraints[9] = (Spreadsheet.railcatchclearance + Spreadsheet.raildiameter) * pi * 0.5
  sketch-geometry (12):
    g0: GeomPoint [constr] X=-51.8363 Y=0 Z=0
    g1: GeomPoint [constr] X=51.8363 Y=0 Z=0
    g2: GeomPoint [constr] X=-191.836 Y=0 Z=0
    g3: GeomPoint [constr] X=176.836 Y=0 Z=0
    g4: GeomPoint [constr] X=-224.823 Y=0 Z=0
    g5: GeomPoint [constr] X=209.823 Y=0 Z=0
    g6: GeomPoint [constr] X=-377.823 Y=0 Z=0
    g7: GeomPoint [constr] X=347.823 Y=0 Z=0
    g8: GeomPoint [constr] X=-410.81 Y=0 Z=0
    g9: GeomPoint [constr] X=380.81 Y=0 Z=0
    g10: GeomPoint [constr] X=-530.81 Y=0 Z=0
    g11: GeomPoint [constr] X=500.81 Y=0 Z=0
  constraints (23):
    c: PointOnObject(g0,g-1)
    c: DistanceX(g0,g1) = 103.673
    c: PointOnObject(g2,g-1)
    c: DistanceX(g2,g0) = 140
    c: PointOnObject(g4,g-1)
    c: DistanceX(g4,g2) = 32.9867
    c: PointOnObject(g6,g-1)
    c: DistanceX(g6,g4) = 153
    c: PointOnObject(g8,g-1)
    c: DistanceX(g8,g6) = 32.9867
    c: PointOnObject(g10,g-1)
    c: DistanceX(g10,g8) = 120
    c: DistanceX(g1,g3) = 125
    c: DistanceX(g3,g5) = 32.9867
    c: Symmetric(g0,g1,g-2)
    c: DistanceX(g5,g7) = 138
    c: DistanceX(g7,g9) = 32.9867
    c: DistanceX(g9,g11) = 120
    c: PointOnObject(g3,g-1)
    c: PointOnObject(g5,g-1)
    c: PointOnObject(g7,g-1)
    c: PointOnObject(g9,g-1)
    c: PointOnObject(g11,g-1)
FEATURE [Sketcher::SketchObject] Sketch071  label="outline001"
  ArcFitTolerance = 0
  AttachmentSupport = -> [XY_Plane017]
  FullyConstrained = true
  MakeInternals = false
  MapMode = 5
  expr: Constraints[3] = Spreadsheet.railcatchclearance
  sketch-geometry (2):
    g0: Circle CenterX=0 CenterY=0 CenterZ=0 NormalX=0 NormalY=0 NormalZ=1 AngleXU=0 Radius=9
    g1: Circle CenterX=0 CenterY=0 CenterZ=0 NormalX=0 NormalY=0 NormalZ=1 AngleXU=0 Radius=7.5
  constraints (4):
    c: Coincident(g0,g-1)
    c: Diameter(g0) = 18
    c: Coincident(g1,g0)
    c: Diameter(g1) = 15
FEATURE [PartDesign::Pad] Pad025
  Direction = (0,0,1)
  Length = 15
  Length2 = 10
  Profile = -> Sketch071
  ReferenceAxis = -> Sketch071 [N_Axis]
  Suppressed = false
  Type = 0
FEATURE [PartDesign::Body] Body015  label="mandrel-small-rail-bend"
  AllowCompound = false
  Group = -> [Sketch071,Pad025]
  Origin = -> Origin017
  Placement = pos=(83,0,0) rot=(0,0,1;0rad)
  Tip = -> Pad025
FEATURE [Sketcher::SketchObject] Sketch072  label="outline002"
  ArcFitTolerance = 0
  AttachmentSupport = -> [XY_Plane018]
  FullyConstrained = true
  MakeInternals = false
  MapMode = 5
  expr: Constraints[3] = Spreadsheet.railtruckclearance
  sketch-geometry (2):
    g0: Circle CenterX=0 CenterY=0 CenterZ=0 NormalX=0 NormalY=0 NormalZ=1 AngleXU=0 Radius=9
    g1: Circle CenterX=0 CenterY=0 CenterZ=0 NormalX=0 NormalY=0 NormalZ=1 AngleXU=0 Radius=30
  constraints (4):
    c: Coincident(g0,g-1)
    c: Diameter(g0) = 18
    c: Coincident(g1,g0)
    c: Diameter(g1) = 60
FEATURE [PartDesign::Pad] Pad026
  Direction = (0,0,1)
  Length = 10
  Length2 = 10
  Profile = -> Sketch072
  ReferenceAxis = -> Sketch072 [N_Axis]
  Suppressed = false
  Type = 0
FEATURE [PartDesign::Body] Body016  label="mandrel-large-rail-bend"
  AllowCompound = false
  Group = -> [Sketch072,Pad026]
  Origin = -> Origin018
  Placement = pos=(92,-58,0) rot=(0,0,1;0rad)
  Tip = -> Pad026
FEATURE [Sketcher::SketchObject] Sketch083  label="truck-rails-short"
  ArcFitTolerance = 0
  AttachmentOffset = pos=(0,0,-33) rot=(0,0,1;0rad)
  AttachmentSupport = -> [YZ_Plane012]
  FullyConstrained = true
  MakeInternals = false
  MapMode = 5
  Placement = pos=(-33,0,0) rot=(0.57735,0.57735,0.57735;2.0944rad)
  expr: .AttachmentOffset.Base.z = -(Spreadsheet.railtruckclearance / 2 + Spreadsheet.raildiameter / 2)
  expr: Constraints[10] = Spreadsheet.raildiameter / 2
  expr: Constraints[11] = Spreadsheet.railLengthNegYLong
  expr: Constraints[9] = Spreadsheet.railLengthPosY
  sketch-geometry (4):
    g0: LineSegment StartX=-52 StartY=-19 StartZ=0 EndX=58 EndY=-19 EndZ=0
    g1: ArcOfCircle CenterX=58 CenterY=-11 CenterZ=0 NormalX=0 NormalY=0 NormalZ=1 AngleXU=0 Radius=8 StartAngle=4.71239 EndAngle=7.85398
    g2: LineSegment StartX=58 StartY=-3 StartZ=0 EndX=-95 EndY=-3 EndZ=0
    g3: ArcOfCircle CenterX=-95 CenterY=9.75 CenterZ=0 NormalX=0 NormalY=0 NormalZ=1 AngleXU=0 Radius=12.75 StartAngle=1.5708 EndAngle=4.71239
  constraints (15):
    c: Horizontal(g0)
    c: Coincident(g1,g0)
    c: Coincident(g2,g1)
    c: Horizontal(g2)
    c: Coincident(g3,g2)
    c: Vertical(g2,g3)
    c: Vertical(g3,g3)
    c: Vertical(g0,g1)
    c: Vertical(g1,g1)
    c: DistanceX(g-1,g1) = 58
    c: DistanceY(g1,g-1) = 3
    c: DistanceX(g3,g-1) = 95
    c: DistanceX(g0,g0) = 110
    c: DistanceY(g0,g1) = 16
    c: DistanceY(g2,g3) = 25.5
FEATURE [PartDesign::SubShapeBinder] Binder001  label="rails-shape-binder"
  BindCopyOnChange = 0
  BindMode = 0
  ClaimChildren = false
  Context = -> Part001 [Body011.Binder001.]
  Fuse = false
  MakeFace = true
  OffsetFill = false
  OffsetIntersection = false
  OffsetJoinType = 0
  OffsetOpenResult = false
  PartialLoad = false
  Relative = true
  Support = -> [Sketch042,Sketch043,Sketch083]
  _Version = 2
FEATURE [Sketcher::SketchObject] Sketch091  label="shaft-profile"
  ArcFitTolerance = 0
  AttachmentSupport = -> [YZ_Plane022]
  FullyConstrained = true
  MakeInternals = false
  MapMode = 5
  Placement = pos=(0,0,0) rot=(0.57735,0.57735,0.57735;2.0944rad)
  sketch-geometry (1):
    g0: Circle CenterX=0 CenterY=0 CenterZ=0 NormalX=0 NormalY=0 NormalZ=1 AngleXU=0 Radius=4
  constraints (2):
    c: Coincident(g0,g-1)
    c: Diameter(g0) = 8
FEATURE [PartDesign::Pad] Pad034  label="shaft-pad"
  Direction = (1,0,0)
  Length = 28
  Length2 = 10
  Placement = pos=(0,0,0) rot=(1,1,1;2.0944rad)
  Profile = -> Sketch091
  ReferenceAxis = -> Sketch091 [N_Axis]
  Suppressed = false
  Type = 0
FEATURE [Sketcher::SketchObject] Sketch092  label="head-outline"
  ArcFitTolerance = 0
  AttachmentSupport = -> [YZ_Plane022]
  FullyConstrained = true
  MakeInternals = false
  MapMode = 5
  Placement = pos=(0,0,0) rot=(0.57735,0.57735,0.57735;2.0944rad)
  sketch-geometry (1):
    g0: Circle CenterX=0 CenterY=0 CenterZ=0 NormalX=0 NormalY=0 NormalZ=1 AngleXU=0 Radius=6.5
  constraints (2):
    c: Coincident(g0,g-1)
    c: Diameter(g0) = 13
FEATURE [PartDesign::Pad] Pad035  label="head-pad"
  BaseFeature = -> Pad034
  Direction = (1,0,0)
  Length = 8
  Length2 = 10
  Placement = pos=(0,0,0) rot=(1,1,1;2.0944rad)
  Profile = -> Sketch092
  ReferenceAxis = -> Sketch092 [N_Axis]
  Suppressed = false
  Type = 0
FEATURE [Sketcher::SketchObject] Sketch093  label="hex-profile"
  ArcFitTolerance = 0
  AttachmentSupport = -> [YZ_Plane022]
  FullyConstrained = true
  MakeInternals = false
  MapMode = 5
  Placement = pos=(0,0,0) rot=(0.57735,0.57735,0.57735;2.0944rad)
  sketch-geometry (7):
    g0: LineSegment StartX=3 StartY=1.73205 StartZ=0 EndX=1.3e-15 EndY=3.4641 EndZ=0
    g1: LineSegment StartX=1.3e-15 StartY=3.4641 StartZ=0 EndX=-3 EndY=1.73205 EndZ=0
    g2: LineSegment StartX=-3 StartY=1.73205 StartZ=0 EndX=-3 EndY=-1.73205 EndZ=0
    g3: LineSegment StartX=-3 StartY=-1.73205 StartZ=0 EndX=4e-16 EndY=-3.4641 EndZ=0
    g4: LineSegment StartX=4e-16 StartY=-3.4641 StartZ=0 EndX=3 EndY=-1.73205 EndZ=0
    g5: LineSegment StartX=3 StartY=-1.73205 StartZ=0 EndX=3 EndY=1.73205 EndZ=0
    g6: Circle [constr] CenterX=0 CenterY=0 CenterZ=0 NormalX=0 NormalY=0 NormalZ=1 AngleXU=0 Radius=3.4641
  constraints (16):
    c: Coincident(g0,g1)
    c: Coincident(g1,g2)
    c: Coincident(g2,g3)
    c: Coincident(g3,g4)
    c: Coincident(g4,g5)
    c: Coincident(g5,g0)
    c: Equal(g0, g1-g5) x5
    c: PointOnObject(g0,g6)
    c: PointOnObject(g1,g6)
    c: PointOnObject(g2,g6)
    c: PointOnObject(g3,g6)
    c: PointOnObject(g4,g6)
    c: PointOnObject(g5,g6)
    c: Coincident(g6,g-1)
    c: Vertical(g5)
    c: DistanceX(g1,g0) = 6
FEATURE [PartDesign::Pocket] Pocket034  label="hex-pocket"
  BaseFeature = -> Pad035
  Direction = (-1,0,0)
  Length = 5
  Length2 = 5
  Placement = pos=(0,0,0) rot=(1,1,1;2.0944rad)
  Profile = -> Sketch093
  ReferenceAxis = -> Sketch093 [N_Axis]
  Reversed = true
  Suppressed = false
  Type = 0
FEATURE [PartDesign::Body] Body020  label="m8-bolt"
  AllowCompound = false
  Group = -> [Sketch091,Pad034,Sketch092,Pad035,Sketch093,Pocket034]
  Origin = -> Origin022
  Placement = pos=(19.6005,-17,-16.6) rot=(0,0,1;0rad)
  Tip = -> Pocket034
FEATURE [Sketcher::SketchObject] Sketch094
  ArcFitTolerance = 0
  AttachmentSupport = -> [YZ_Plane023]
  FullyConstrained = true
  MakeInternals = false
  MapMode = 5
  Placement = pos=(0,0,0) rot=(0.57735,0.57735,0.57735;2.0944rad)
  sketch-geometry (8):
    g0: LineSegment StartX=6.5 StartY=3.75278 StartZ=0 EndX=0 EndY=7.50555 EndZ=0
    g1: LineSegment StartX=0 StartY=7.50555 StartZ=0 EndX=-6.5 EndY=3.75278 EndZ=0
    g2: LineSegment StartX=-6.5 StartY=3.75278 StartZ=0 EndX=-6.5 EndY=-3.75278 EndZ=0
    g3: LineSegment StartX=-6.5 StartY=-3.75278 StartZ=0 EndX=0 EndY=-7.50555 EndZ=0
    g4: LineSegment StartX=0 StartY=-7.50555 StartZ=0 EndX=6.5 EndY=-3.75278 EndZ=0
    g5: LineSegment StartX=6.5 StartY=-3.75278 StartZ=0 EndX=6.5 EndY=3.75278 EndZ=0
    g6: Circle [constr] CenterX=0 CenterY=0 CenterZ=0 NormalX=0 NormalY=0 NormalZ=1 AngleXU=0 Radius=7.50555
    g7: Circle CenterX=0 CenterY=0 CenterZ=0 NormalX=0 NormalY=0 NormalZ=1 AngleXU=0 Radius=3.5
  constraints (18):
    c: Coincident(g0,g1)
    c: Coincident(g1,g2)
    c: Coincident(g2,g3)
    c: Coincident(g3,g4)
    c: Coincident(g4,g5)
    c: Coincident(g5,g0)
    c: Equal(g0, g1-g5) x5
    c: PointOnObject(g0,g6)
    c: PointOnObject(g1,g6)
    c: PointOnObject(g2,g6)
    c: PointOnObject(g3,g6)
    c: PointOnObject(g4,g6)
    c: PointOnObject(g5,g6)
    c: Coincident(g6,g-1)
    c: Vertical(g5)
    c: DistanceX(g1,g0) = 13
    c: Coincident(g7,g6)
    c: Diameter(g7) = 7
FEATURE [PartDesign::Pad] Pad036
  Direction = (1,0,0)
  Length = 6
  Length2 = 10
  Placement = pos=(0,0,0) rot=(1,1,1;2.0944rad)
  Profile = -> Sketch094
  ReferenceAxis = -> Sketch094 [N_Axis]
  Suppressed = false
  Type = 0
FEATURE [PartDesign::Body] Body021  label="m8-nut"
  AllowCompound = false
  Group = -> [Sketch094,Pad036]
  Origin = -> Origin023
  Placement = pos=(38,-17,-16.6) rot=(0,-1,0;0rad)
  Tip = -> Pad036
FEATURE [Sketcher::SketchObject] Sketch095
  ArcFitTolerance = 0
  AttachmentOffset = pos=(0,0,66) rot=(0,0,1;0rad)
  AttachmentSupport = -> [XZ_Plane024]
  FullyConstrained = false
  MakeInternals = false
  MapMode = 5
  Placement = pos=(0,-66,1.47e-14) rot=(1,0,0;1.5708rad)
  sketch-geometry (13):
    g0: LineSegment StartX=8 StartY=17.8681 StartZ=0 EndX=-3.5 EndY=17.8681 EndZ=0
    g1: ArcOfCircle CenterX=-3.5 CenterY=15.8681 CenterZ=0 NormalX=0 NormalY=0 NormalZ=1 AngleXU=0 Radius=2 StartAngle=1.5708 EndAngle=3.14159
    g2: GeomPoint [constr] X=-5.5 Y=17.8681 Z=0
    g3: ArcOfCircle CenterX=8 CenterY=15.8681 CenterZ=0 NormalX=0 NormalY=0 NormalZ=1 AngleXU=0 Radius=2 StartAngle=0 EndAngle=1.5708
    g4: GeomPoint [constr] X=10 Y=17.8681 Z=0
    g5: GeomPoint [constr] X=10 Y=-5 Z=0
    g6: LineSegment StartX=-5.5 StartY=15.8681 StartZ=0 EndX=-5.5 EndY=-6 EndZ=0
    g7: LineSegment StartX=-3.5 StartY=-8 StartZ=0 EndX=8 EndY=-8 EndZ=0
    g8: LineSegment StartX=10 StartY=-6 StartZ=0 EndX=10 EndY=15.8681 EndZ=0
    g9: ArcOfCircle CenterX=-3.5 CenterY=-6 CenterZ=0 NormalX=0 NormalY=0 NormalZ=1 AngleXU=0 Radius=2 StartAngle=3.14159 EndAngle=4.71239
    g10: GeomPoint [constr] X=-5.5 Y=-8 Z=0
    g11: ArcOfCircle CenterX=8 CenterY=-6 CenterZ=0 NormalX=0 NormalY=0 NormalZ=1 AngleXU=0 Radius=2 StartAngle=4.71239 EndAngle=6.28319
    g12: GeomPoint [constr] X=10 Y=-8 Z=0
  constraints (26):
    c: Horizontal(g0)
    c: PointOnObject(g2,g0)
    c: Tangent(g0,g1) = -1.5708
    c: PointOnObject(g4,g0)
    c: Tangent(g0,g3) = -1.5708
    c: Radius(g1) = 2
    c: Radius(g3) = 2
    c: Vertical(g6)
    c: Horizontal(g7)
    c: Vertical(g8)
    c: DistanceX(g10,g-1) = 5.5
    c: PointOnObject(g10,g6)
    c: PointOnObject(g10,g7)
    c: Tangent(g6,g9) = -1.5708
    c: Tangent(g7,g9) = -1.5708
    c: PointOnObject(g12,g7)
    c: PointOnObject(g12,g8)
    c: Tangent(g7,g11) = -1.5708
    c: Tangent(g8,g11) = -1.5708
    c: Radius(g9) = 2
    c: Radius(g11) = 2
    c: DistanceY(g10,g-1) = 8
    c: Tangent(g8,g3) = -1.5708
    c: DistanceX(g-1,g12) = 10
    c: Vertical(g2,g1)
    c: Tangent(g1,g6) = -1.5708
FEATURE [PartDesign::Pad] Pad037
  Direction = (0,-1,2e-16)
  Length = 65
  Length2 = 10
  Placement = pos=(0,0,0) rot=(1,0,0;1.5708rad)
  Profile = -> Sketch095
  ReferenceAxis = -> Sketch095 [N_Axis]
  Reversed = true
  Suppressed = false
  Type = 0
FEATURE [Sketcher::SketchObject] Sketch096  label="ramp-outline"
  ArcFitTolerance = 0
  AttachmentOffset = pos=(0,0,1) rot=(0,0,1;0rad)
  AttachmentSupport = -> [XY_Plane024]
  FullyConstrained = false
  MakeInternals = false
  MapMode = 5
  Placement = pos=(0,0,1) rot=(0,0,1;0rad)
  sketch-geometry (3):
    g0: LineSegment StartX=-4.84971 StartY=-30.2537 StartZ=0 EndX=-4.84971 EndY=-1.1201 EndZ=0
    g1: LineSegment StartX=-13.4497 StartY=-30.2537 StartZ=0 EndX=-4.84971 EndY=-1.1201 EndZ=0
    g2: LineSegment StartX=-13.4497 StartY=-30.2537 StartZ=0 EndX=-4.84971 EndY=-30.2537 EndZ=0
  constraints (5):
    c: Vertical(g0)
    c: Coincident(g1,g0)
    c: Horizontal(g2)
    c: Coincident(g0,g2)
    c: Coincident(g1,g2)
FEATURE [PartDesign::Pad] Pad038  label="ramp-pad"
  BaseFeature = -> Pad037
  Direction = (0,0,1)
  Length = 13
  Length2 = 7
  Placement = pos=(0,0,0) rot=(1,0,0;1.5708rad)
  Profile = -> Sketch096
  ReferenceAxis = -> Sketch096 [N_Axis]
  Suppressed = false
  Type = 0
FEATURE [Sketcher::SketchObject] Sketch098  label="bolt-hole-outline"
  ArcFitTolerance = 0
  AttachmentOffset = pos=(-37,7.42,0) rot=(0,0,1;0rad)
  AttachmentSupport = -> [YZ_Plane024]
  FullyConstrained = true
  MakeInternals = false
  MapMode = 5
  Placement = pos=(0,-37,7.42) rot=(0.57735,0.57735,0.57735;2.0944rad)
  sketch-geometry (1):
    g0: Circle CenterX=0 CenterY=0 CenterZ=0 NormalX=0 NormalY=0 NormalZ=1 AngleXU=0 Radius=4
  constraints (2):
    c: Diameter(g0) = 8
    c: Coincident(g0,g-1)
FEATURE [PartDesign::Pocket] Pocket036  label="bolt-hole-pocket"
  BaseFeature = -> Pad038
  Direction = (-1,0,0)
  Length = 65
  Length2 = 5
  Midplane = true
  Placement = pos=(0,0,0) rot=(1,0,0;1.5708rad)
  Profile = -> Sketch098
  ReferenceAxis = -> Sketch098 [N_Axis]
  Suppressed = false
  Type = 0
FEATURE [Sketcher::SketchObject] Sketch099
  ArcFitTolerance = 0
  AttachmentOffset = pos=(0,0,1) rot=(0,0,1;0rad)
  AttachmentSupport = -> [XZ_Plane024]
  FullyConstrained = true
  MakeInternals = false
  MapMode = 5
  Placement = pos=(0,-1,2e-16) rot=(1,0,0;1.5708rad)
  expr: Constraints[1] = Spreadsheet.raildiameter + 0.3 mm
  sketch-geometry (1):
    g0: Circle CenterX=0 CenterY=0 CenterZ=0 NormalX=0 NormalY=0 NormalZ=1 AngleXU=0 Radius=3.15
  constraints (2):
    c: Coincident(g0,g-1)
    c: Diameter(g0) = 6.3
FEATURE [PartDesign::Pocket] Pocket037
  BaseFeature = -> Pocket036
  Direction = (0,1,-2e-16)
  Length = 75
  Length2 = 5
  Placement = pos=(0,0,0) rot=(1,0,0;1.5708rad)
  Profile = -> Sketch099
  ReferenceAxis = -> Sketch099 [N_Axis]
  Reversed = true
  Suppressed = false
  Type = 0
FEATURE [Sketcher::SketchObject] Sketch100
  ArcFitTolerance = 0
  AttachmentOffset = pos=(0,0,1) rot=(0,0,1;0rad)
  AttachmentSupport = -> [XZ_Plane024]
  FullyConstrained = false
  MakeInternals = false
  MapMode = 5
  Placement = pos=(0,-1,2e-16) rot=(1,0,0;1.5708rad)
  sketch-geometry (6):
    g0: LineSegment StartX=-6.32089 StartY=20 StartZ=0 EndX=1.01752 EndY=20 EndZ=0
    g1: LineSegment StartX=1.01752 StartY=20 StartZ=0 EndX=1.01752 EndY=0 EndZ=0
    g2: LineSegment StartX=1.01752 StartY=0 StartZ=0 EndX=0.034595 EndY=0 EndZ=0
    g3: LineSegment StartX=0.034595 StartY=0 StartZ=0 EndX=0.034595 EndY=16.4036 EndZ=0
    g4: LineSegment StartX=0.034595 StartY=16.4036 StartZ=0 EndX=-6.32089 EndY=16.4036 EndZ=0
    g5: LineSegment StartX=-6.32089 StartY=16.4036 StartZ=0 EndX=-6.32089 EndY=20 EndZ=0
  constraints (14):
    c: Coincident(g0,g1)
    c: Coincident(g1,g2)
    c: Horizontal(g2)
    c: Vertical(g1)
    c: PointOnObject(g2,g-1)
    c: DistanceY(g2,g0) = 20
    c: Coincident(g3,g2)
    c: Vertical(g3)
    c: Coincident(g4,g3)
    c: Horizontal(g4)
    c: Coincident(g5,g4)
    c: Vertical(g5)
    c: Coincident(g0,g5)
    c: Horizontal(g0)
FEATURE [PartDesign::Pocket] Pocket038
  BaseFeature = -> Pocket037
  Direction = (0,1,-2e-16)
  Length = 65
  Length2 = 5
  Placement = pos=(0,0,0) rot=(1,0,0;1.5708rad)
  Profile = -> Sketch100
  ReferenceAxis = -> Sketch100 [N_Axis]
  Reversed = true
  Suppressed = false
  Type = 0
FEATURE [Sketcher::SketchObject] Sketch101  label="grip-tape-outline"
  ArcFitTolerance = 1e-06
  AttachmentSupport = -> [XY_Plane025]
  FullyConstrained = true
  MakeInternals = false
  MapMode = 5
  sketch-geometry (10):
    g0: LineSegment StartX=-70 StartY=46.5 StartZ=0 EndX=-70 EndY=-46.5 EndZ=0
    g1: LineSegment StartX=-32 StartY=-84.5 StartZ=0 EndX=32 EndY=-84.5 EndZ=0
    g2: LineSegment StartX=70 StartY=-46.5 StartZ=0 EndX=70 EndY=46.5 EndZ=0
    g3: LineSegment StartX=32 StartY=84.5 StartZ=0 EndX=-32 EndY=84.5 EndZ=0
    g4: ArcOfCircle CenterX=-32 CenterY=46.5 CenterZ=0 NormalX=0 NormalY=0 NormalZ=1 AngleXU=0 Radius=38 StartAngle=1.5708 EndAngle=3.14159
    g5: ArcOfCircle CenterX=-32 CenterY=-46.5 CenterZ=0 NormalX=0 NormalY=0 NormalZ=1 AngleXU=0 Radius=38 StartAngle=3.14159 EndAngle=4.71239
    g6: ArcOfCircle CenterX=32 CenterY=-46.5 CenterZ=0 NormalX=0 NormalY=0 NormalZ=1 AngleXU=0 Radius=38 StartAngle=4.71239 EndAngle=6.28319
    g7: ArcOfCircle CenterX=32 CenterY=46.5 CenterZ=0 NormalX=0 NormalY=0 NormalZ=1 AngleXU=0 Radius=38 StartAngle=1e-16 EndAngle=1.5708
    g8: GeomPoint [constr] X=-70 Y=84.5 Z=0
    g9: GeomPoint [constr] X=70 Y=-84.5 Z=0
  constraints (22):
    c: Tangent(g0,g4) = -1.5708
    c: Tangent(g0,g5) = -1.5708
    c: Tangent(g1,g5) = -1.5708
    c: Tangent(g1,g6) = -1.5708
    c: Tangent(g2,g6) = -1.5708
    c: Tangent(g2,g7) = -1.5708
    c: Tangent(g3,g7) = -1.5708
    c: Tangent(g3,g4) = -1.5708
    c: Vertical(g0)
    c: Vertical(g2)
    c: Horizontal(g1)
    c: Horizontal(g3)
    c: Equal(g5,g6)
    c: PointOnObject(g8,g0)
    c: PointOnObject(g8,g3)
    c: PointOnObject(g9,g1)
    c: PointOnObject(g9,g2)
    c: Symmetric(g0,g2,g-2)
    c: Symmetric(g1,g3,g-1)
    c: DistanceX(g0,g2) = 140
    c: DistanceY(g1,g3) = 169
    c: Radius(g7) = 38
FEATURE [PartDesign::Pad] Pad039
  Direction = (0,0,1)
  Length = 1
  Length2 = 10
  Profile = -> Sketch101
  ReferenceAxis = -> Sketch101 [N_Axis]
  Suppressed = false
  Type = 0
FEATURE [PartDesign::Body] Body023  label="grip-tape"
  AllowCompound = false
  Group = -> [Sketch101,Pad039]
  Origin = -> Origin025
  Placement = pos=(0,0,9) rot=(0,0,1;1.309rad)
  Tip = -> Pad039
FEATURE [App::Part] Part  label="freeskate"
  Group = -> [Sketch004,Revolve,Part__Mirroring,Sketch008,Revolve001,Sketch009,Extrude002,Cut,Part__Mirroring001,Body002,Body,Sketch030,Sketch031,Sweep,Offset2D,Extrude,Sketch003,Extrude001,Common,Sketch011,Extrude003,Cut001,Body006,Body007,Part__Mirroring003,Part__Mirroring004,Part__Mirroring005,Body008,Part__Mirroring006,Part__Mirroring007,Part__Mirroring008,Body009,Part__Mirroring009,Body010,+4 more]
  Origin = -> Origin004
FEATURE [Sketcher::SketchObject] Sketch102  label="hex-nut-hole-outline"
  ArcFitTolerance = 1e-06
  AttachmentOffset = pos=(-37,7.42,10) rot=(0,0,1;0rad)
  AttachmentSupport = -> [YZ_Plane024]
  FullyConstrained = true
  MakeInternals = false
  MapMode = 5
  Placement = pos=(10,-37,7.42) rot=(0.57735,0.57735,0.57735;2.0944rad)
  sketch-geometry (7):
    g0: LineSegment StartX=0 StartY=7.62102 StartZ=0 EndX=-6.6 EndY=3.81051 EndZ=0
    g1: LineSegment StartX=-6.6 StartY=3.81051 StartZ=0 EndX=-6.6 EndY=-3.81051 EndZ=0
    g2: LineSegment StartX=-6.6 StartY=-3.81051 StartZ=0 EndX=-8e-15 EndY=-7.62102 EndZ=0
    g3: LineSegment StartX=-8e-15 StartY=-7.62102 StartZ=0 EndX=6.6 EndY=-3.81051 EndZ=0
    g4: LineSegment StartX=6.6 StartY=-3.81051 StartZ=0 EndX=6.6 EndY=3.81051 EndZ=0
    g5: LineSegment StartX=6.6 StartY=3.81051 StartZ=0 EndX=0 EndY=7.62102 EndZ=0
    g6: Circle [constr] CenterX=0 CenterY=0 CenterZ=0 NormalX=0 NormalY=0 NormalZ=1 AngleXU=0 Radius=7.62102
  constraints (16):
    c: Coincident(g0,g1)
    c: Coincident(g1,g2)
    c: Coincident(g2,g3)
    c: Coincident(g3,g4)
    c: Coincident(g4,g5)
    c: Coincident(g5,g0)
    c: Equal(g0, g1-g5) x5
    c: PointOnObject(g0,g6)
    c: PointOnObject(g1,g6)
    c: PointOnObject(g2,g6)
    c: PointOnObject(g3,g6)
    c: PointOnObject(g4,g6)
    c: PointOnObject(g5,g6)
    c: Coincident(g6,g-1)
    c: PointOnObject(g0,g-2)
    c: DistanceX(g1,g3) = 13.2
FEATURE [Sketcher::SketchObject] Sketch103
  ArcFitTolerance = 1e-06
  AttachmentOffset = pos=(0,0,-8) rot=(0,0,1;0rad)
  AttachmentSupport = -> [XY_Plane024]
  FullyConstrained = false
  MakeInternals = false
  MapMode = 5
  Placement = pos=(0,0,-8) rot=(0,0,1;0rad)
  sketch-geometry (10):
    g0: LineSegment StartX=6.49059 StartY=-32.6161 StartZ=0 EndX=6.49059 EndY=-66 EndZ=0
    g1: LineSegment StartX=6.49059 StartY=-66 StartZ=0 EndX=18.8419 EndY=-66 EndZ=0
    g2: LineSegment StartX=33.5251 StartY=-54.067 StartZ=0 EndX=39.0082 EndY=-27.8163 EndZ=0
    g3: LineSegment StartX=29.2377 StartY=-25.6881 StartZ=0 EndX=24.8143 EndY=-45.1928 EndZ=0
    g4: ArcOfCircle CenterX=17.5 CenterY=-43.534 CenterZ=0 NormalX=0 NormalY=0 NormalZ=1 AngleXU=0 Radius=7.5 StartAngle=3.14159 EndAngle=6.06017
    g5: ArcOfCircle CenterX=18.8419 CenterY=-51 CenterZ=0 NormalX=0 NormalY=0 NormalZ=1 AngleXU=0 Radius=15 StartAngle=4.71239 EndAngle=6.07727
    g6: GeomPoint [constr] X=31.0325 Y=-66 Z=0
    g7: ArcOfCircle CenterX=34.1138 CenterY=-26.794 CenterZ=0 NormalX=0 NormalY=0 NormalZ=1 AngleXU=0 Radius=5 StartAngle=6.07727 EndAngle=9.20176
    g8: LineSegment StartX=10 StartY=-43.534 StartZ=0 EndX=10 EndY=-32.6161 EndZ=0
    g9: LineSegment StartX=6.49059 StartY=-32.6161 StartZ=0 EndX=10 EndY=-32.6161 EndZ=0
  constraints (21):
    c: Coincident(g1,g0)
    c: Horizontal(g1)
    c: Diameter(g4) = 15
    c: PointOnObject(g6,g1)
    c: PointOnObject(g6,g2)
    c: Tangent(g1,g5) = -1.5708
    c: Tangent(g2,g5) = -1.5708
    c: Radius(g5) = 15
    c: Tangent(g7,g3) = -1.5708
    c: Tangent(g7,g2) = -1.5708
    c: Distance(g3,g3) = 20
    c: Diameter(g7) = 10
    c: Tangent(g3,g4) = 1.5708
    c: Vertical(g8)
    c: Coincident(g9,g0)
    c: Coincident(g9,g8)
    c: Horizontal(g9)
    c: Tangent(g8,g4) = 1.5708
    c: DistanceX(g-1,g8) = 10
    c: Vertical(g0)
    c: DistanceY(g0,g-1) = 66
FEATURE [PartDesign::Pad] Pad040
  BaseFeature = -> Pocket038
  Direction = (0,0,1)
  Length = 18
  Length2 = 10
  Placement = pos=(0,0,0) rot=(1,0,0;1.5708rad)
  Profile = -> Sketch103
  ReferenceAxis = -> Sketch103 [N_Axis]
  Refine = true
  Suppressed = false
  Type = 0
FEATURE [PartDesign::Pocket] Pocket039  label="hex-nut-pocket"
  BaseFeature = -> Pad040
  Direction = (-1,0,0)
  Length = 6
  Length2 = 5
  Placement = pos=(0,0,0) rot=(1,0,0;1.5708rad)
  Profile = -> Sketch102
  ReferenceAxis = -> Sketch102 [N_Axis]
  Refine = true
  Suppressed = false
  Type = 0
FEATURE [PartDesign::Body] Body022  label="catch"
  AllowCompound = false
  Group = -> [Sketch095,Pad037,Sketch096,Pad038,Sketch098,Pocket036,Sketch099,Pocket037,Sketch100,Pocket038,Sketch102,Sketch103,Pad040,Pocket039]
  Origin = -> Origin024
  Placement = pos=(33,20,-24) rot=(0,0,1;0rad)
  Tip = -> Pocket039
FEATURE [App::Link] freeskate  label="freeskate001"
  LinkPlacement = pos=(39.3578,-89.7326,-16.3443) rot=(0,-0.707107,0.707107;3.14159rad)
  LinkedObject = -> Part
  Placement = pos=(39.3578,-89.7326,-16.3443) rot=(0,-0.707107,0.707107;3.14159rad)
FEATURE [App::Link] holster  label="holster001"
  LinkPlacement = pos=(0,-5.75398,-16.7543) rot=(1,0,0;4.71239rad)
  LinkedObject = -> Part001
  Placement = pos=(0,-5.75398,-16.7543) rot=(1,0,0;4.71239rad)
FEATURE [App::FeaturePython] GroundedJoint  # Assembly grounded joint (typed FeaturePython)
  ObjectToGround = -> holster
  Placement = pos=(0,-5.75398,-16.7543) rot=(-1,0,0;1.5708rad)
FEATURE [App::FeaturePython] Joint  label="Slider"  # Assembly joint (typed FeaturePython)
  Activated = true
  AngleMax = 0
  AngleMin = 0
  Detach1 = false
  Detach2 = false
  Distance = 0
  Distance2 = 0
  EnableAngleMax = false
  EnableAngleMin = false
  EnableLengthMax = false
  EnableLengthMin = false
  JointType = 3 (Slider)
  LengthMax = 0
  LengthMin = 0
  Placement1 = pos=(7.8e-15,-13,-63.6207) rot=(-0.57735,0.57735,0.57735;2.0944rad)
  Placement2 = pos=(6.35781,-66,3.64205) rot=(0.57735,-0.57735,0.57735;2.0944rad)
  Reference1 = -> Assembly [freeskate.Body006.Face68,freeskate.Body006.Face68]
  Reference2 = -> Assembly [holster.Body022.Face2,holster.Body022.Face2]
FEATURE [Assembly::JointGroup] Joints
  Group = -> [GroundedJoint,Joint]
FEATURE [Assembly::AssemblyObject] Assembly  label="freeskates-holsters-assembly"
  Group = -> [Joints,freeskate,holster,GroundedJoint,Joint]
  Origin = -> Origin026
  Type = Assembly
FEATURE [Sketcher::SketchObject] Sketch104  label="base-plate-bottom-outline"
  ArcFitTolerance = 1e-06
  AttachmentSupport = -> [XY_Plane027]
  FullyConstrained = true
  MakeInternals = false
  MapMode = 5
  sketch-geometry (21):
    g0: LineSegment StartX=-42 StartY=86 StartZ=0 EndX=-42 EndY=-87 EndZ=0
    g1: LineSegment StartX=42 StartY=-87 StartZ=0 EndX=42 EndY=86 EndZ=0
    g2: LineSegment StartX=34 StartY=94 StartZ=0 EndX=-34 EndY=94 EndZ=0
    g3: ArcOfCircle CenterX=-34 CenterY=86 CenterZ=0 NormalX=0 NormalY=0 NormalZ=1 AngleXU=0 Radius=8 StartAngle=1.5708 EndAngle=3.14159
    g4: ArcOfCircle CenterX=-34 CenterY=-87 CenterZ=0 NormalX=0 NormalY=0 NormalZ=1 AngleXU=0 Radius=8 StartAngle=3.14159 EndAngle=4.71239
    g5: ArcOfCircle CenterX=34 CenterY=-87 CenterZ=0 NormalX=0 NormalY=0 NormalZ=1 AngleXU=0 Radius=8 StartAngle=4.71239 EndAngle=6.28319
    g6: ArcOfCircle CenterX=34 CenterY=86 CenterZ=0 NormalX=0 NormalY=0 NormalZ=1 AngleXU=0 Radius=8 StartAngle=6e-16 EndAngle=1.5708
    g7: GeomPoint [constr] X=-42 Y=94 Z=0
    g8: LineSegment StartX=-34 StartY=-95 StartZ=0 EndX=-29 EndY=-95 EndZ=0
    g9: LineSegment StartX=34 StartY=-95 StartZ=0 EndX=29 EndY=-95 EndZ=0
    g10: LineSegment StartX=-21 StartY=-103 StartZ=0 EndX=-21 EndY=-105 EndZ=0
    g11: LineSegment StartX=21 StartY=-103 StartZ=0 EndX=21 EndY=-105 EndZ=0
    g12: ArcOfCircle CenterX=-29 CenterY=-103 CenterZ=0 NormalX=0 NormalY=0 NormalZ=1 AngleXU=0 Radius=8 StartAngle=0 EndAngle=1.5708
    g13: ArcOfCircle CenterX=-11 CenterY=-105 CenterZ=0 NormalX=0 NormalY=0 NormalZ=1 AngleXU=0 Radius=10 StartAngle=3.14159 EndAngle=4.71239
    g14: ArcOfCircle CenterX=11 CenterY=-105 CenterZ=0 NormalX=0 NormalY=0 NormalZ=1 AngleXU=0 Radius=10 StartAngle=4.71239 EndAngle=6.28319
    g15: ArcOfCircle CenterX=29 CenterY=-103 CenterZ=0 NormalX=0 NormalY=0 NormalZ=1 AngleXU=0 Radius=8 StartAngle=1.5708 EndAngle=3.14159
    g16: LineSegment StartX=-11 StartY=-115 StartZ=0 EndX=11 EndY=-115 EndZ=0
    g17: ArcOfCircle CenterX=-9 CenterY=-103.5 CenterZ=0 NormalX=0 NormalY=0 NormalZ=1 AngleXU=0 Radius=5 StartAngle=1.5708 EndAngle=4.71239
    g18: ArcOfCircle CenterX=9 CenterY=-103.5 CenterZ=0 NormalX=0 NormalY=0 NormalZ=1 AngleXU=0 Radius=5 StartAngle=4.71239 EndAngle=7.85398
    g19: LineSegment StartX=-9 StartY=-98.5 StartZ=0 EndX=9 EndY=-98.5 EndZ=0
    g20: LineSegment StartX=-9 StartY=-108.5 StartZ=0 EndX=9 EndY=-108.5 EndZ=0
  constraints (49):
    c: Tangent(g0,g3) = -1.5708
    c: Tangent(g0,g4) = -1.5708
    c: Tangent(g1,g5) = -1.5708
    c: Tangent(g1,g6) = -1.5708
    c: Tangent(g2,g6) = -1.5708
    c: Tangent(g2,g3) = -1.5708
    c: Vertical(g0)
    c: Vertical(g1)
    c: Horizontal(g2)
    c: PointOnObject(g7,g0)
    c: PointOnObject(g7,g2)
    c: Symmetric(g4,g5,g-2)
    c: DistanceX(g0,g1) = 84
    c: Distance(g2,g-1) = 94
    c: Radius(g3) = 8
    c: Radius(g4) = 8
    c: Horizontal(g8)
    c: Horizontal(g9)
    c: Vertical(g10)
    c: Vertical(g11)
    c: Tangent(g15,g9) = -1.5708
    c: Tangent(g14,g11) = 1.5708
    c: Tangent(g12,g8) = 1.5708
    c: Tangent(g12,g10) = 1.5708
    c: Tangent(g13,g10) = -1.5708
    c: Horizontal(g16)
    c: Tangent(g16,g13) = -1.5708
    c: Tangent(g16,g14) = -1.5708
    c: Tangent(g15,g11) = -1.5708
    c: DistanceX(g10,g11) = 42
    c: DistanceY(g14,g9) = 20
    c: Symmetric(g10,g11,g-2)
    c: Radius(g13) = 10
    c: Radius(g14) = 10
    c: Tangent(g8,g4) = -1.5708
    c: Radius(g15) = 8
    c: Tangent(g9,g5) = 1.5708
    c: Horizontal(g8,g9)
    c: DistanceY(g5,g-1) = 95
    c: Radius(g6) = 8
    c: Tangent(g17,g19) = 1.5708
    c: Tangent(g17,g20) = -1.5708
    c: Tangent(g18,g19) = 1.5708
    c: Tangent(g18,g20) = -1.5708
    c: Equal(g17,g18)
    c: Radius(g17) = 5
    c: Symmetric(g17,g18,g-2)
    c: DistanceX(g17,g18) = 18
    c: DistanceY(g14,g18) = 6.5
FEATURE [PartDesign::Pad] Pad041  label="bottom-outline-pad"
  Direction = (0,0,1)
  Length = 6
  Length2 = 10
  Profile = -> Sketch104
  ReferenceAxis = -> Sketch104 [N_Axis]
  Refine = true
  Suppressed = false
  Type = 0
FEATURE [Sketcher::SketchObject] Sketch106  label="base-plate-top-outline"
  ArcFitTolerance = 1e-06
  AttachmentSupport = -> [XY_Plane028]
  FullyConstrained = true
  MakeInternals = false
  MapMode = 5
  sketch-geometry (21):
    g0: LineSegment StartX=-42 StartY=86 StartZ=0 EndX=-42 EndY=-87 EndZ=0
    g1: LineSegment StartX=42 StartY=-87 StartZ=0 EndX=42 EndY=86 EndZ=0
    g2: LineSegment StartX=34 StartY=94 StartZ=0 EndX=-34 EndY=94 EndZ=0
    g3: ArcOfCircle CenterX=-34 CenterY=86 CenterZ=0 NormalX=0 NormalY=0 NormalZ=1 AngleXU=0 Radius=8 StartAngle=1.5708 EndAngle=3.14159
    g4: ArcOfCircle CenterX=-34 CenterY=-87 CenterZ=0 NormalX=0 NormalY=0 NormalZ=1 AngleXU=0 Radius=8 StartAngle=3.14159 EndAngle=4.71239
    g5: ArcOfCircle CenterX=34 CenterY=-87 CenterZ=0 NormalX=0 NormalY=0 NormalZ=1 AngleXU=0 Radius=8 StartAngle=4.71239 EndAngle=6.28319
    g6: ArcOfCircle CenterX=34 CenterY=86 CenterZ=0 NormalX=0 NormalY=0 NormalZ=1 AngleXU=0 Radius=8 StartAngle=-9e-16 EndAngle=1.5708
    g7: GeomPoint [constr] X=-42 Y=94 Z=0
    g8: LineSegment StartX=-34 StartY=-95 StartZ=0 EndX=-29 EndY=-95 EndZ=0
    g9: LineSegment StartX=34 StartY=-95 StartZ=0 EndX=29 EndY=-95 EndZ=0
    g10: ArcOfCircle CenterX=-29 CenterY=-103 CenterZ=0 NormalX=0 NormalY=0 NormalZ=1 AngleXU=0 Radius=8 StartAngle=3e-16 EndAngle=1.5708
    g11: LineSegment StartX=-21 StartY=-103 StartZ=0 EndX=-21 EndY=-105 EndZ=0
    g12: ArcOfCircle CenterX=-11 CenterY=-105 CenterZ=0 NormalX=0 NormalY=0 NormalZ=1 AngleXU=0 Radius=10 StartAngle=3.14159 EndAngle=4.71239
    g13: LineSegment StartX=-11 StartY=-115 StartZ=0 EndX=11 EndY=-115 EndZ=0
    g14: ArcOfCircle CenterX=11 CenterY=-105 CenterZ=0 NormalX=0 NormalY=0 NormalZ=1 AngleXU=0 Radius=10 StartAngle=4.71239 EndAngle=6.28319
    g15: LineSegment StartX=21 StartY=-105 StartZ=0 EndX=21 EndY=-103 EndZ=0
    g16: ArcOfCircle CenterX=29 CenterY=-103 CenterZ=0 NormalX=0 NormalY=0 NormalZ=1 AngleXU=0 Radius=8 StartAngle=1.5708 EndAngle=3.14159
    g17: ArcOfCircle CenterX=-9 CenterY=-103.5 CenterZ=0 NormalX=0 NormalY=0 NormalZ=1 AngleXU=0 Radius=5 StartAngle=1.5708 EndAngle=4.71239
    g18: ArcOfCircle CenterX=9 CenterY=-103.5 CenterZ=0 NormalX=0 NormalY=0 NormalZ=1 AngleXU=0 Radius=5 StartAngle=4.71239 EndAngle=7.85398
    g19: LineSegment StartX=-9 StartY=-98.5 StartZ=0 EndX=9 EndY=-98.5 EndZ=0
    g20: LineSegment StartX=-9 StartY=-108.5 StartZ=0 EndX=9 EndY=-108.5 EndZ=0
  constraints (49):
    c: Tangent(g0,g3) = -1.5708
    c: Tangent(g0,g4) = -1.5708
    c: Tangent(g1,g5) = -1.5708
    c: Tangent(g1,g6) = -1.5708
    c: Tangent(g2,g6) = -1.5708
    c: Tangent(g2,g3) = -1.5708
    c: Vertical(g0)
    c: Vertical(g1)
    c: Horizontal(g2)
    c: Equal(g3,g4)
    c: Equal(g4,g5)
    c: PointOnObject(g7,g0)
    c: PointOnObject(g7,g2)
    c: Symmetric(g0,g1,g-2)
    c: Radius(g6) = 8
    c: DistanceX(g0,g1) = 84
    c: DistanceY(g-1,g2) = 94
    c: DistanceY(g5,g-1) = 95
    c: Horizontal(g8)
    c: Horizontal(g9)
    c: Tangent(g8,g4) = -1.5708
    c: Tangent(g10,g8) = 1.5708
    c: Vertical(g11)
    c: Radius(g10) = 8
    c: Symmetric(g8,g9,g-2)
    c: Tangent(g12,g11) = -1.5708
    c: Horizontal(g13)
    c: Tangent(g14,g13) = -1.5708
    c: Vertical(g15)
    c: Tangent(g16,g9) = -1.5708
    c: Tangent(g16,g15) = 1.5708
    c: Tangent(g15,g14) = -1.5708
    c: Tangent(g13,g12) = -1.5708
    c: Radius(g12) = 10
    c: Radius(g14) = 10
    c: DistanceX(g11,g14) = 42
    c: DistanceY(g13,g9) = 20
    c: Radius(g16) = 8
    c: Tangent(g11,g10) = 1.5708
    c: Tangent(g9,g5) = 1.5708
    c: Tangent(g17,g19) = 1.5708
    c: Tangent(g17,g20) = -1.5708
    c: Tangent(g18,g19) = 1.5708
    c: Tangent(g18,g20) = -1.5708
    c: Equal(g17,g18)
    c: Symmetric(g17,g18,g-2)
    c: Radius(g17) = 5
    c: DistanceY(g13,g18) = 6.5
    c: DistanceX(g17,g18) = 18
FEATURE [PartDesign::Pad] Pad042  label="base-plate-top-pad"
  Direction = (0,0,1)
  Length = 6
  Length2 = 10
  Profile = -> Sketch106
  ReferenceAxis = -> Sketch106 [N_Axis]
  Refine = true
  Reversed = true
  Suppressed = false
  Type = 0
FEATURE [Sketcher::SketchObject] Sketch108  label="rail-channel-outline001"
  ArcFitTolerance = 1e-06
  AttachmentSupport = -> [XY_Plane028]
  FullyConstrained = true
  MakeInternals = false
  MapMode = 5
  sketch-geometry (3):
    g0: LineSegment StartX=-33 StartY=-110 StartZ=0 EndX=-33 EndY=50 EndZ=0
    g1: LineSegment StartX=33 StartY=-110 StartZ=0 EndX=33 EndY=50 EndZ=0
    g2: ArcOfCircle CenterX=8e-16 CenterY=50 CenterZ=0 NormalX=0 NormalY=0 NormalZ=1 AngleXU=0 Radius=33 StartAngle=0 EndAngle=3.14159
  constraints (10):
    c: Vertical(g0)
    c: Vertical(g1)
    c: Coincident(g2,g0)
    c: Coincident(g2,g1)
    c: Horizontal(g0,g2)
    c: Horizontal(g2,g1)
    c: Symmetric(g0,g1,g-2)
    c: DistanceX(g0,g1) = 66
    c: Distance(g1,g-1) = 50
    c: DistanceY(g1,g-1) = 110
FEATURE [Sketcher::SketchObject] Sketch109  label="rail-path"
  ArcFitTolerance = 1e-06
  AttachmentOffset = pos=(0,0,22.5) rot=(0,0,1;0rad)
  AttachmentSupport = -> [XY_Plane030]
  FullyConstrained = true
  MakeInternals = false
  MapMode = 5
  Placement = pos=(0,0,22.5) rot=(0,0,1;0rad)
  sketch-geometry (5):
    g0: LineSegment StartX=-33 StartY=-100 StartZ=0 EndX=-33 EndY=42.25 EndZ=0
    g1: LineSegment StartX=33 StartY=-100 StartZ=0 EndX=33 EndY=42.25 EndZ=0
    g2: LineSegment StartX=-20.25 StartY=55 StartZ=0 EndX=20.25 EndY=55 EndZ=0
    g3: ArcOfCircle CenterX=-20.25 CenterY=42.25 CenterZ=0 NormalX=0 NormalY=0 NormalZ=1 AngleXU=0 Radius=12.75 StartAngle=1.5708 EndAngle=3.14159
    g4: ArcOfCircle CenterX=20.25 CenterY=42.25 CenterZ=0 NormalX=0 NormalY=0 NormalZ=1 AngleXU=0 Radius=12.75 StartAngle=2e-16 EndAngle=1.5708
  constraints (12):
    c: Symmetric(g0,g1,g-2)
    c: Symmetric(g0,g1,g-2)
    c: DistanceX(g0,g1) = 66
    c: Vertical(g0)
    c: Horizontal(g2)
    c: Tangent(g3,g0) = 1.5708
    c: Tangent(g3,g2) = 1.5708
    c: Tangent(g4,g2) = 1.5708
    c: Tangent(g4,g1) = -1.5708
    c: Radius(g3) = 12.75
    c: DistanceY(g-1,g2) = 55
    c: DistanceY(g1,g-1) = 100
FEATURE [Sketcher::SketchObject] Sketch110  label="rail-profile001"
  ArcFitTolerance = 1e-06
  AttachmentOffset = pos=(-33,22.5,0) rot=(0,0,1;0rad)
  AttachmentSupport = -> [XZ_Plane030]
  FullyConstrained = true
  MakeInternals = false
  MapMode = 5
  Placement = pos=(-33,5e-15,22.5) rot=(1,0,0;1.5708rad)
  sketch-geometry (1):
    g0: Circle CenterX=0 CenterY=0 CenterZ=0 NormalX=0 NormalY=0 NormalZ=1 AngleXU=0 Radius=3
  constraints (2):
    c: Coincident(g0,g-1)
    c: Diameter(g0) = 6
FEATURE [PartDesign::AdditivePipe] AdditivePipe001  label="rail-channel-additive-pipe"
  AuxilleryCurvelinear = true
  AuxillerySpineTangent = false
  Binormal = (0,0,0)
  Mode = 2
  Placement = pos=(0,0,0) rot=(1,0,0;1.5708rad)
  Profile = -> Sketch110
  Refine = true
  Spine = -> Sketch109
  SpineTangent = false
  Suppressed = false
  Transformation = 0
  Transition = 0
FEATURE [PartDesign::Body] Body026  label="rail-channel"
  AllowCompound = false
  Group = -> [Sketch109,Sketch110,AdditivePipe001]
  Origin = -> Origin030
  Tip = -> AdditivePipe001
FEATURE [PartDesign::FeatureBase] Clone
  BaseFeature = -> AdditivePipe001
  Placement = pos=(0,0,0) rot=(1,0,0;1.5708rad)
  Suppressed = false
FEATURE [PartDesign::Body] Body027  label="rail-channel-clone-bottom"
  AllowCompound = false
  Group = -> [Clone]
  Origin = -> Origin031
  Tip = -> Clone
FEATURE [Sketcher::SketchObject] Sketch112  label="R-label"
  ArcFitTolerance = 1e-06
  AttachmentOffset = pos=(0,-25,-6) rot=(1,0,0;3.14159rad)
  AttachmentSupport = -> [XY_Plane028]
  FullyConstrained = false
  MakeInternals = false
  MapMode = 5
  Placement = pos=(0,-25,-6) rot=(1,0,0;3.14159rad)
  sketch-geometry (12):
    g0: LineSegment StartX=-15.4486 StartY=29.3685 StartZ=0 EndX=-15.4486 EndY=-37.9045 EndZ=0
    g1: LineSegment StartX=-15.4486 StartY=-37.9045 StartZ=0 EndX=-10.1821 EndY=-37.9045 EndZ=0
    g2: LineSegment StartX=-10.1821 StartY=-37.9045 StartZ=0 EndX=-10.1821 EndY=-8.83917 EndZ=0
    g3: LineSegment StartX=-10.1821 StartY=-8.83917 StartZ=0 EndX=8.72842 EndY=-36.4485 EndZ=0
    g4: LineSegment StartX=8.72842 StartY=-36.4485 StartZ=0 EndX=16.6312 EndY=-36.4485 EndZ=0
    g5: LineSegment StartX=16.6312 StartY=-36.4485 StartZ=0 EndX=-2.026 EndY=-9.29621 EndZ=0
    g6: ArcOfCircle CenterX=-3.98901 CenterY=10.0685 CenterZ=0 NormalX=0 NormalY=0 NormalZ=1 AngleXU=0 Radius=19.464 StartAngle=4.81341 EndAngle=7.72405
    g7: LineSegment StartX=-1.46711 StartY=29.3685 StartZ=0 EndX=-15.4486 EndY=29.3685 EndZ=0
    g8: LineSegment StartX=-10.1821 StartY=22.5318 StartZ=0 EndX=-10.1821 EndY=-1.83352 EndZ=0
    g9: ArcOfCircle CenterX=-1.72728 CenterY=10.3492 CenterZ=0 NormalX=0 NormalY=0 NormalZ=1 AngleXU=0 Radius=12.1836 StartAngle=4.70081 EndAngle=7.86667
    g10: LineSegment StartX=-1.86833 StartY=-1.83352 StartZ=0 EndX=-10.1821 EndY=-1.83352 EndZ=0
    g11: LineSegment StartX=-1.88181 StartY=22.5318 StartZ=0 EndX=-10.1821 EndY=22.5318 EndZ=0
  constraints (21):
    c: Vertical(g0)
    c: Coincident(g1,g0)
    c: Horizontal(g1)
    c: Coincident(g2,g1)
    c: Vertical(g2)
    c: Coincident(g3,g2)
    c: Coincident(g4,g3)
    c: Horizontal(g4)
    c: Coincident(g5,g4)
    c: Coincident(g6,g5)
    c: Coincident(g7,g6)
    c: Horizontal(g7)
    c: Coincident(g0,g7)
    c: Vertical(g8)
    c: Coincident(g10,g9)
    c: Coincident(g10,g8)
    c: Coincident(g11,g9)
    c: Coincident(g11,g8)
    c: Horizontal(g10)
    c: Vertical(g2,g8)
    c: Horizontal(g11)
FEATURE [PartDesign::Fillet] Fillet
  Base = -> Pad042 [Edge37,Edge40,Edge46,Edge43,Edge48,Edge4,Edge7,Edge10,Edge13,Edge16,Edge19,Edge34,Edge31,Edge28,Edge22,Edge25,Edge58,Edge60,Edge55,Edge52]
  BaseFeature = -> Pad042
  Radius = 3.2
  Refine = true
  SupportTransform = false
  Suppressed = false
  UseAllEdges = false
FEATURE [PartDesign::Pocket] Pocket042  label="R-label-pocket"
  BaseFeature = -> Fillet
  Direction = (0,1e-16,1)
  Length = 0.5
  Length2 = 5
  Profile = -> Sketch112
  ReferenceAxis = -> Sketch112 [N_Axis]
  Refine = true
  Suppressed = false
  Type = 0
FEATURE [PartDesign::Body] Body025  label="top-block"
  AllowCompound = false
  Group = -> [Sketch106,Pad042,Fillet,Sketch108,Sketch112,Pocket042]
  Origin = -> Origin028
  Placement = pos=(0,0,22.5) rot=(0,0,1;0rad)
  Tip = -> Pocket042
FEATURE [PartDesign::Fillet] Fillet001
  Base = -> Pad041 [Edge37,Edge34,Edge28,Edge31,Edge25,Edge22,Edge19,Edge60,Edge55,Edge52,Edge58,Edge40,Edge46,Edge43,Edge48,Edge4,Edge7,Edge10,Edge13,Edge16]
  BaseFeature = -> Pad041
  Radius = 3.2
  Refine = true
  SupportTransform = false
  Suppressed = false
  UseAllEdges = false
FEATURE [Sketcher::SketchObject] Sketch113
  ArcFitTolerance = 1e-06
  AttachmentOffset = pos=(0,0,28) rot=(0,0,1;0rad)
  AttachmentSupport = -> [XZ_Plane032]
  FullyConstrained = true
  MakeInternals = false
  MapMode = 5
  Placement = pos=(0,-28,6.2e-15) rot=(1,0,0;1.5708rad)
  sketch-geometry (16):
    g0: LineSegment StartX=-39 StartY=2.5 StartZ=0 EndX=39 EndY=2.5 EndZ=0
    g1: LineSegment StartX=-39 StartY=2.5 StartZ=0 EndX=-39 EndY=0 EndZ=0
    g2: LineSegment StartX=-37 StartY=0 StartZ=0 EndX=-37 EndY=1.5 EndZ=0
    g3: LineSegment StartX=-37 StartY=1.5 StartZ=0 EndX=-1 EndY=1.5 EndZ=0
    g4: GeomPoint X=-38 Y=0 Z=0
    g5: LineSegment StartX=-39 StartY=0 StartZ=0 EndX=-38 EndY=0 EndZ=0
    g6: LineSegment StartX=-37 StartY=0 StartZ=0 EndX=-38 EndY=0 EndZ=0
    g7: LineSegment StartX=-1 StartY=1.5 StartZ=0 EndX=-1 EndY=0 EndZ=0
    g8: LineSegment StartX=-1 StartY=0 StartZ=0 EndX=0 EndY=0 EndZ=0
    g9: LineSegment StartX=0 StartY=0 StartZ=0 EndX=1 EndY=0 EndZ=0
    g10: LineSegment StartX=1 StartY=0 StartZ=0 EndX=1 EndY=1.5 EndZ=0
    g11: LineSegment StartX=1 StartY=1.5 StartZ=0 EndX=37 EndY=1.5 EndZ=0
    g12: LineSegment StartX=37 StartY=1.5 StartZ=0 EndX=37 EndY=0 EndZ=0
    g13: LineSegment StartX=39 StartY=0 StartZ=0 EndX=39 EndY=2.5 EndZ=0
    g14: LineSegment StartX=37 StartY=0 StartZ=0 EndX=38 EndY=0 EndZ=0
    g15: LineSegment StartX=38 StartY=0 StartZ=0 EndX=39 EndY=0 EndZ=0
  constraints (46):
    c: Horizontal(g0)
    c: Coincident(g1,g0)
    c: Vertical(g1)
    c: Vertical(g2)
    c: Coincident(g3,g2)
    c: Horizontal(g3)
    c: Coincident(g5,g1)
    c: Coincident(g5,g4)
    c: Horizontal(g5)
    c: Coincident(g6,g2)
    c: Coincident(g6,g4)
    c: Horizontal(g6)
    c: Equal(g5,g6)
    c: DistanceX(g1,g2) = 2
    c: Coincident(g7,g3)
    c: Vertical(g7)
    c: Coincident(g8,g7)
    c: Horizontal(g8)
    c: Coincident(g9,g8)
    c: Horizontal(g9)
    c: Coincident(g10,g9)
    c: Vertical(g10)
    c: Equal(g8,g9)
    c: DistanceX(g4,g8) = 38
    c: DistanceX(g7,g9) = 2
    c: Coincident(g11,g10)
    c: Horizontal(g11)
    c: Coincident(g12,g11)
    c: Vertical(g12)
    c: Vertical(g13)
    c: Coincident(g0,g13)
    c: DistanceX(g12,g13) = 2
    c: Horizontal(g3,g10)
    c: DistanceY(g1,g1) = 2.5
    c: Distance(g3,g0) = 1
    c: PointOnObject(g1,g-1)
    c: PointOnObject(g7,g-1)
    c: PointOnObject(g12,g-1)
    c: PointOnObject(g8,g-2)
    c: Coincident(g14,g12)
    c: PointOnObject(g14,g-1)
    c: Coincident(g15,g14)
    c: Coincident(g15,g13)
    c: Horizontal(g15)
    c: Equal(g15,g14)
    c: DistanceX(g8,g14) = 38
FEATURE [Sketcher::SketchObject] Sketch114
  ArcFitTolerance = 1e-06
  AttachmentSupport = -> [XY_Plane032]
  FullyConstrained = true
  MakeInternals = false
  MapMode = 5
  sketch-geometry (10):
    g0: LineSegment StartX=-42 StartY=147 StartZ=0 EndX=-42 EndY=-27 EndZ=0
    g1: LineSegment StartX=-36 StartY=-33 StartZ=0 EndX=36 EndY=-33 EndZ=0
    g2: LineSegment StartX=42 StartY=-27 StartZ=0 EndX=42 EndY=147 EndZ=0
    g3: LineSegment StartX=36 StartY=153 StartZ=0 EndX=-36 EndY=153 EndZ=0
    g4: ArcOfCircle CenterX=-36 CenterY=147 CenterZ=0 NormalX=0 NormalY=0 NormalZ=1 AngleXU=0 Radius=6 StartAngle=1.5708 EndAngle=3.14159
    g5: ArcOfCircle CenterX=-36 CenterY=-27 CenterZ=0 NormalX=0 NormalY=0 NormalZ=1 AngleXU=0 Radius=6 StartAngle=3.14159 EndAngle=4.71239
    g6: ArcOfCircle CenterX=36 CenterY=-27 CenterZ=0 NormalX=0 NormalY=0 NormalZ=1 AngleXU=0 Radius=6 StartAngle=4.71239 EndAngle=6.28319
    g7: ArcOfCircle CenterX=36 CenterY=147 CenterZ=0 NormalX=0 NormalY=0 NormalZ=1 AngleXU=0 Radius=6 StartAngle=1.8e-15 EndAngle=1.5708
    g8: GeomPoint [constr] X=-42 Y=153 Z=0
    g9: GeomPoint [constr] X=42 Y=-33 Z=0
  constraints (23):
    c: Tangent(g0,g4) = -1.5708
    c: Tangent(g0,g5) = -1.5708
    c: Tangent(g1,g5) = -1.5708
    c: Tangent(g1,g6) = -1.5708
    c: Tangent(g2,g6) = -1.5708
    c: Tangent(g2,g7) = -1.5708
    c: Tangent(g3,g7) = -1.5708
    c: Tangent(g3,g4) = -1.5708
    c: Vertical(g0)
    c: Vertical(g2)
    c: Horizontal(g1)
    c: Horizontal(g3)
    c: Equal(g4,g5)
    c: Equal(g5,g6)
    c: PointOnObject(g8,g0)
    c: PointOnObject(g8,g3)
    c: PointOnObject(g9,g1)
    c: PointOnObject(g9,g2)
    c: Symmetric(g0,g2,g-2)
    c: DistanceX(g0,g2) = 84
    c: Radius(g5) = 6
    c: DistanceY(g1,g-1) = 33
    c: Distance(g3,g-1) = 153
FEATURE [PartDesign::Pad] Pad044
  Direction = (0,0,1)
  Length = 1
  Length2 = 10
  Profile = -> Sketch114
  ReferenceAxis = -> Sketch114 [N_Axis]
  Refine = true
  Suppressed = false
  Type = 0
FEATURE [PartDesign::Pad] Pad043
  BaseFeature = -> Pad044
  Direction = (0,-1,2e-16)
  Length = 25
  Length2 = 10
  Profile = -> Sketch113
  ReferenceAxis = -> Sketch113 [N_Axis]
  Refine = true
  Reversed = true
  Suppressed = false
  Type = 0
FEATURE [PartDesign::LinearPattern] LinearPattern
  BaseFeature = -> Pad043
  Direction = -> Y_Axis032
  Length = 150
  Mode = 1
  Occurrences = 4
  Offset = 50
  Originals = -> [Pad043]
  Refine = true
  Suppressed = false
  TransformMode = 0
FEATURE [PartDesign::Body] Body028  label="MOLLE-base"
  AllowCompound = false
  Group = -> [Pad044,Sketch114,Sketch113,Pad043,LinearPattern]
  Origin = -> Origin032
  Placement = pos=(3.7e-15,-59,31) rot=(0,1,0;3.14159rad)
  Tip = -> LinearPattern
FEATURE [Sketcher::SketchObject] Sketch115
  ArcFitTolerance = 1e-06
  AttachmentSupport = -> [XY_Plane033]
  FullyConstrained = true
  MakeInternals = false
  MapMode = 5
  sketch-geometry (12):
    g0: LineSegment StartX=-12.5 StartY=-117 StartZ=0 EndX=12.5 EndY=-117 EndZ=0
    g1: LineSegment StartX=7 StartY=0 StartZ=0 EndX=-7 EndY=0 EndZ=0
    g2: Circle CenterX=0 CenterY=-25 CenterZ=0 NormalX=0 NormalY=0 NormalZ=1 AngleXU=0 Radius=2.5
    g3: Circle CenterX=0 CenterY=-44.5 CenterZ=0 NormalX=0 NormalY=0 NormalZ=1 AngleXU=0 Radius=2.5
    g4: Circle CenterX=0 CenterY=-64 CenterZ=0 NormalX=0 NormalY=0 NormalZ=1 AngleXU=0 Radius=2.5
    g5: Circle CenterX=0 CenterY=-83.5 CenterZ=0 NormalX=0 NormalY=0 NormalZ=1 AngleXU=0 Radius=2.5
    g6: LineSegment StartX=-12.5 StartY=-117 StartZ=0 EndX=-12.5 EndY=-5 EndZ=0
    g7: LineSegment StartX=12.5 StartY=-117 StartZ=0 EndX=12.5 EndY=-5 EndZ=0
    g8: LineSegment StartX=-12.5 StartY=-5 StartZ=0 EndX=-7 EndY=-5 EndZ=0
    g9: LineSegment StartX=-7 StartY=-5 StartZ=0 EndX=-7 EndY=0 EndZ=0
    g10: LineSegment StartX=12.5 StartY=-5 StartZ=0 EndX=7 EndY=-5 EndZ=0
    g11: LineSegment StartX=7 StartY=-5 StartZ=0 EndX=7 EndY=0 EndZ=0
  constraints (34):
    c: Symmetric(g1,g1,g-2)
    c: PointOnObject(g1,g-1)
    c: DistanceY(g0,g1) = 117
    c: PointOnObject(g2,g-2)
    c: Diameter(g2) = 5
    c: PointOnObject(g3,g-2)
    c: PointOnObject(g4,g-2)
    c: PointOnObject(g5,g-2)
    c: Equal(g3,g2)
    c: Equal(g2,g4)
    c: Equal(g2,g5)
    c: DistanceY(g3,g2) = 19.5
    c: DistanceY(g4,g3) = 19.5
    c: DistanceY(g5,g4) = 19.5
    c: DistanceX(g0,g0) = 25
    c: Coincident(g6,g0)
    c: Vertical(g6)
    c: Coincident(g7,g0)
    c: Vertical(g7)
    c: DistanceX(g1,g1) = 14
    c: Coincident(g8,g6)
    c: Horizontal(g8)
    c: Coincident(g9,g8)
    c: Coincident(g9,g1)
    c: Vertical(g9)
    c: Coincident(g10,g7)
    c: Horizontal(g10)
    c: Coincident(g11,g10)
    c: Coincident(g11,g1)
    c: Vertical(g11)
    c: Symmetric(g0,g0,g-2)
    c: Horizontal(g8,g10)
    c: DistanceY(g9,g9) = 5
    c: DistanceY(g2,g-1) = 25
FEATURE [PartDesign::Pad] Pad045
  Direction = (0,0,1)
  Length = 8
  Length2 = 10
  Profile = -> Sketch115
  ReferenceAxis = -> Sketch115 [N_Axis]
  Refine = true
  Suppressed = false
  Type = 0
FEATURE [Sketcher::SketchObject] Sketch116
  ArcFitTolerance = 1e-06
  AttachmentSupport = -> [XZ_Plane035]
  FullyConstrained = true
  MakeInternals = false
  MapMode = 5
  Placement = pos=(0,0,0) rot=(1,0,0;1.5708rad)
  sketch-geometry (6):
    g0: LineSegment StartX=0 StartY=0 StartZ=0 EndX=3.5 EndY=0 EndZ=0
    g1: LineSegment StartX=3.5 StartY=0 StartZ=0 EndX=3.5 EndY=-4 EndZ=0
    g2: LineSegment StartX=3.5 StartY=-4 StartZ=0 EndX=2 EndY=-4 EndZ=0
    g3: LineSegment StartX=2 StartY=-4 StartZ=0 EndX=2 EndY=-14 EndZ=0
    g4: LineSegment StartX=2 StartY=-14 StartZ=0 EndX=0 EndY=-14 EndZ=0
    g5: LineSegment StartX=0 StartY=0 StartZ=0 EndX=0 EndY=-14 EndZ=0
  constraints (17):
    c: Horizontal(g0)
    c: Coincident(g1,g0)
    c: Vertical(g1)
    c: Coincident(g2,g1)
    c: Horizontal(g2)
    c: Coincident(g3,g2)
    c: Vertical(g3)
    c: Coincident(g0,g-1)
    c: DistanceX(g0,g0) = 3.5
    c: DistanceY(g1,g1) = 4
    c: DistanceX(g0,g2) = 2
    c: Coincident(g4,g3)
    c: PointOnObject(g4,g-2)
    c: Horizontal(g4)
    c: DistanceY(g3,g3) = 10
    c: Coincident(g5,g0)
    c: Coincident(g5,g4)
FEATURE [PartDesign::Revolution] Revolution003
  Angle = 360
  Angle2 = 60
  Axis = (0,2e-16,1)
  Base = (0,0,0)
  Placement = pos=(0,0,0) rot=(1,0,0;1.5708rad)
  Profile = -> Sketch116
  ReferenceAxis = -> Sketch116 [V_Axis]
  Refine = true
  Reversed = true
  Suppressed = false
  Type = 0
FEATURE [Sketcher::SketchObject] Sketch117  label="nut-profile"
  ArcFitTolerance = 1e-06
  AttachmentOffset = pos=(0,0,-8.8) rot=(0,0,1;0rad)
  AttachmentSupport = -> [XY_Plane035]
  FullyConstrained = true
  MakeInternals = false
  MapMode = 5
  Placement = pos=(0,0,-8.8) rot=(0,0,1;0rad)
  sketch-geometry (7):
    g0: LineSegment StartX=2.02073 StartY=3.5 StartZ=0 EndX=-2.02073 EndY=3.5 EndZ=0
    g1: LineSegment StartX=-2.02073 StartY=3.5 StartZ=0 EndX=-4.04145 EndY=3.85e-13 EndZ=0
    g2: LineSegment StartX=-4.04145 StartY=3.85e-13 StartZ=0 EndX=-2.02073 EndY=-3.5 EndZ=0
    g3: LineSegment StartX=-2.02073 StartY=-3.5 StartZ=0 EndX=2.02073 EndY=-3.5 EndZ=0
    g4: LineSegment StartX=2.02073 StartY=-3.5 StartZ=0 EndX=4.04145 EndY=3.384e-13 EndZ=0
    g5: LineSegment StartX=4.04145 StartY=3.384e-13 StartZ=0 EndX=2.02073 EndY=3.5 EndZ=0
    g6: Circle [constr] CenterX=0 CenterY=0 CenterZ=0 NormalX=0 NormalY=0 NormalZ=1 AngleXU=0 Radius=4.04145
  constraints (16):
    c: Coincident(g0,g1)
    c: Coincident(g1,g2)
    c: Coincident(g2,g3)
    c: Coincident(g3,g4)
    c: Coincident(g4,g5)
    c: Coincident(g5,g0)
    c: Equal(g0, g1-g5) x5
    c: PointOnObject(g0,g6)
    c: PointOnObject(g1,g6)
    c: PointOnObject(g2,g6)
    c: PointOnObject(g3,g6)
    c: PointOnObject(g4,g6)
    c: PointOnObject(g5,g6)
    c: Coincident(g6,g-1)
    c: Horizontal(g0)
    c: DistanceY(g3,g0) = 7
FEATURE [PartDesign::Pad] Pad046  label="nut-profile-pad"
  BaseFeature = -> Revolution003
  Direction = (0,0,1)
  Length = 3.2
  Length2 = 10
  Placement = pos=(0,0,0) rot=(1,0,0;1.5708rad)
  Profile = -> Sketch117
  ReferenceAxis = -> Sketch117 [N_Axis]
  Refine = true
  Reversed = true
  Suppressed = false
  Type = 0
FEATURE [PartDesign::Body] Body031  label="m4-bolt-cavity"
  AllowCompound = false
  Group = -> [Sketch116,Revolution003,Sketch117,Pad046]
  Origin = -> Origin035
  Tip = -> Pad046
FEATURE [PartDesign::FeatureBase] Clone002
  BaseFeature = -> Body031
  Suppressed = false
FEATURE [PartDesign::Body] Body032  label="m4-bolt-cavity-clone-top-2"
  AllowCompound = false
  Group = -> [Clone002]
  Origin = -> Origin036
  Placement = pos=(21,40,28.5) rot=(0,0,1;0rad)
  Tip = -> Clone002
FEATURE [PartDesign::FeatureBase] Clone003
  BaseFeature = -> Body032
  Placement = pos=(23,45,24) rot=(0,0,1;0rad)
  Suppressed = false
FEATURE [PartDesign::Body] Body033  label="m4-bolt-cavity-clone-top-1"
  AllowCompound = false
  Group = -> [Clone003]
  Origin = -> Origin037
  Placement = pos=(-44,-5,4.5) rot=(0,0,1;0rad)
  Tip = -> Clone003
FEATURE [PartDesign::FeatureBase] Clone004
  BaseFeature = -> Body031
  Placement = pos=(-25,45,24) rot=(0,0,1;0rad)
  Suppressed = false
FEATURE [PartDesign::Body] Body034  label="m4-bolt-cavity-clone-bottom-1"
  AllowCompound = false
  Group = -> [Clone004]
  Origin = -> Origin038
  Placement = pos=(46,-5,4.5) rot=(0,0,1;0rad)
  Tip = -> Clone004
FEATURE [PartDesign::FeatureBase] Clone005
  BaseFeature = -> Body031
  Placement = pos=(-25,45,24) rot=(0,0,1;0rad)
  Suppressed = false
FEATURE [PartDesign::Body] Body035  label="m4-bolt-cavity-clone-bottom-2"
  AllowCompound = false
  Group = -> [Clone005]
  Origin = -> Origin039
  Placement = pos=(4,-5,4.5) rot=(0,0,1;0rad)
  Tip = -> Clone005
FEATURE [Sketcher::SketchObject] Sketch119  label="roller-profile"
  ArcFitTolerance = 1e-06
  AttachmentSupport = -> [XY_Plane040]
  FullyConstrained = true
  MakeInternals = false
  MapMode = 5
  sketch-geometry (4):
    g0: LineSegment StartX=-15 StartY=6 StartZ=0 EndX=15 EndY=6 EndZ=0
    g1: ArcOfCircle CenterX=-15 CenterY=0 CenterZ=0 NormalX=0 NormalY=0 NormalZ=1 AngleXU=0 Radius=6 StartAngle=1.5708 EndAngle=3.14159
    g2: ArcOfCircle CenterX=15 CenterY=0 CenterZ=0 NormalX=0 NormalY=0 NormalZ=1 AngleXU=0 Radius=6 StartAngle=0 EndAngle=1.5708
    g3: LineSegment StartX=-21 StartY=7e-16 StartZ=0 EndX=21 EndY=0 EndZ=0
  constraints (13):
    c: PointOnObject(g1,g-1)
    c: Coincident(g1,g0)
    c: PointOnObject(g1,g-1)
    c: PointOnObject(g2,g-1)
    c: Coincident(g2,g0)
    c: PointOnObject(g2,g-1)
    c: Vertical(g0,g1)
    c: Vertical(g0,g2)
    c: Symmetric(g0,g0,g-2)
    c: Radius(g1) = 6
    c: DistanceX(g1,g2) = 42
    c: Coincident(g3,g1)
    c: Coincident(g3,g2)
FEATURE [PartDesign::Revolution] Revolution004  label="roller-revolution"
  Angle = 360
  Angle2 = 60
  Axis = (1,0,0)
  Base = (0,0,0)
  Profile = -> Sketch119
  ReferenceAxis = -> X_Axis040
  Refine = true
  Suppressed = false
  Type = 0
FEATURE [PartDesign::Body] Body036  label="roller"
  AllowCompound = false
  Group = -> [Sketch119,Revolution004]
  Origin = -> Origin040
  Placement = pos=(0,76,15) rot=(0,0,1;0rad)
  Tip = -> Revolution004
FEATURE [Sketcher::SketchObject] Sketch122  label="roller-outline"
  ArcFitTolerance = 1e-06
  AttachmentSupport = -> [XY_Plane041]
  FullyConstrained = true
  MakeInternals = false
  MapMode = 5
  sketch-geometry (6):
    g0: ArcOfCircle CenterX=-15 CenterY=0 CenterZ=0 NormalX=0 NormalY=0 NormalZ=1 AngleXU=0 Radius=6.5 StartAngle=1.5708 EndAngle=4.71239
    g1: ArcOfCircle CenterX=15 CenterY=0 CenterZ=0 NormalX=0 NormalY=0 NormalZ=1 AngleXU=0 Radius=6.5 StartAngle=4.71239 EndAngle=7.85398
    g2: LineSegment StartX=-15 StartY=6.5 StartZ=0 EndX=15 EndY=6.5 EndZ=0
    g3: LineSegment StartX=-15 StartY=-6.5 StartZ=0 EndX=15 EndY=-6.5 EndZ=0
    g4: GeomPoint X=-21.5 Y=0 Z=0
    g5: GeomPoint X=21.5 Y=0 Z=0
  constraints (13):
    c: Tangent(g0,g2) = 1.5708
    c: Tangent(g0,g3) = -1.5708
    c: Tangent(g1,g2) = 1.5708
    c: Tangent(g1,g3) = -1.5708
    c: Equal(g0,g1)
    c: PointOnObject(g0,g-1)
    c: Symmetric(g0,g1,g-2)
    c: Radius(g0) = 6.5
    c: PointOnObject(g4,g0)
    c: PointOnObject(g4,g-1)
    c: PointOnObject(g5,g1)
    c: PointOnObject(g5,g-1)
    c: DistanceX(g4,g5) = 43
FEATURE [Sketcher::SketchObject] Sketch123  label="axle-cavity-outline"
  ArcFitTolerance = 1e-06
  AttachmentSupport = -> [XY_Plane041]
  FullyConstrained = true
  MakeInternals = false
  MapMode = 5
  sketch-geometry (4):
    g0: ArcOfCircle CenterX=-35 CenterY=0 CenterZ=0 NormalX=0 NormalY=0 NormalZ=1 AngleXU=0 Radius=2 StartAngle=1.5708 EndAngle=4.71239
    g1: ArcOfCircle CenterX=35 CenterY=0 CenterZ=0 NormalX=0 NormalY=0 NormalZ=1 AngleXU=0 Radius=2 StartAngle=4.71239 EndAngle=7.85398
    g2: LineSegment StartX=-35 StartY=2 StartZ=0 EndX=35 EndY=2 EndZ=0
    g3: LineSegment StartX=-35 StartY=-2 StartZ=0 EndX=35 EndY=-2 EndZ=0
  constraints (9):
    c: Tangent(g0,g2) = 1.5708
    c: Tangent(g0,g3) = -1.5708
    c: Tangent(g1,g2) = 1.5708
    c: Tangent(g1,g3) = -1.5708
    c: Equal(g0,g1)
    c: PointOnObject(g0,g-1)
    c: Symmetric(g0,g1,g-2)
    c: Radius(g0) = 2
    c: DistanceX(g0,g1) = 70
FEATURE [PartDesign::Pad] Pad047  label="axle-cavity-pad"
  Direction = (0,0,1)
  Length = 7
  Length2 = 2
  Profile = -> Sketch123
  ReferenceAxis = -> Sketch123 [N_Axis]
  Refine = true
  Suppressed = false
  Type = 4
FEATURE [Sketcher::SketchObject] Sketch124  label="spring-holes"
  ArcFitTolerance = 1e-06
  AttachmentSupport = -> [XY_Plane041]
  FullyConstrained = false
  MakeInternals = false
  MapMode = 5
  sketch-geometry (2):
    g0: Circle CenterX=-29.0994 CenterY=0 CenterZ=0 NormalX=0 NormalY=0 NormalZ=1 AngleXU=0 Radius=3.84837
    g1: Circle CenterX=29.0994 CenterY=0 CenterZ=0 NormalX=0 NormalY=0 NormalZ=1 AngleXU=0 Radius=3.84837
  constraints (3):
    c: PointOnObject(g0,g-1)
    c: Equal(g0,g1)
    c: Symmetric(g0,g1,g-2)
FEATURE [PartDesign::Pad] Pad048  label="spring-holes-pad"
  BaseFeature = -> Pad047
  Direction = (0,0,1)
  Length = 8
  Length2 = 2
  Profile = -> Sketch124
  ReferenceAxis = -> Sketch124 [N_Axis]
  Refine = true
  Suppressed = false
  Type = 4
FEATURE [PartDesign::Pad] Pad049  label="roller-pad"
  BaseFeature = -> Pad048
  Direction = (0,0,1)
  Length = 14
  Length2 = 10
  Midplane = true
  Profile = -> Sketch122
  ReferenceAxis = -> Sketch122 [N_Axis]
  Refine = true
  Suppressed = false
  Type = 0
FEATURE [PartDesign::Body] Body037  label="roller-cavity"
  AllowCompound = false
  Group = -> [Sketch122,Sketch123,Pad047,Sketch124,Pad048,Pad049]
  Origin = -> Origin041
  Placement = pos=(0,76,19) rot=(0,0,1;0rad)
  Tip = -> Pad049
FEATURE [PartDesign::FeatureBase] Clone006
  BaseFeature = -> Body037
  Placement = pos=(0,76,15) rot=(0,0,1;0rad)
  Suppressed = false
FEATURE [PartDesign::Body] Body038  label="roller-cavity-clone-bottom"
  AllowCompound = false
  Group = -> [Clone006]
  Origin = -> Origin042
  Tip = -> Clone006
FEATURE [PartDesign::FeatureBase] Clone007
  BaseFeature = -> Body037
  Placement = pos=(0,76,15) rot=(0,0,1;0rad)
  Suppressed = false
FEATURE [PartDesign::Body] Body039  label="roller-cavity-clone-top"
  AllowCompound = false
  Group = -> [Clone007]
  Origin = -> Origin043
  Tip = -> Clone007
FEATURE [PartDesign::FeatureBase] Clone008
  BaseFeature = -> Body026
  Suppressed = false
FEATURE [PartDesign::Body] Body040  label="rail-channel-clone-top"
  AllowCompound = false
  Group = -> [Clone008]
  Origin = -> Origin044
  Tip = -> Clone008
FEATURE [Sketcher::SketchObject] Sketch118  label="bolt-placement-guide"
  ArcFitTolerance = 1e-06
  FullyConstrained = true
  MakeInternals = false
  sketch-geometry (4):
    g0: GeomPoint X=-21 Y=40 Z=0
    g1: GeomPoint X=21 Y=40 Z=0
    g2: GeomPoint X=-21 Y=-80 Z=0
    g3: GeomPoint X=21 Y=-80 Z=0
  constraints (6):
    c: Symmetric(g0,g1,g-2)
    c: Symmetric(g2,g3,g-2)
    c: Vertical(g0,g2)
    c: DistanceX(g0,g1) = 42
    c: Distance(g0,g-1) = 40
    c: DistanceY(g2,g-1) = 80
FEATURE [Sketcher::SketchObject] Sketch125  label="catch-rail"
  ArcFitTolerance = 1e-06
  AttachmentOffset = pos=(0,0,-19) rot=(0,0,1;0rad)
  AttachmentSupport = -> [XY_Plane012]
  FullyConstrained = true
  MakeInternals = false
  MapMode = 5
  Placement = pos=(0,0,-19) rot=(0,0,1;0rad)
  sketch-geometry (6):
    g0: LineSegment StartX=32.3227 StartY=24.7785 StartZ=0 EndX=18 EndY=-7.77854 EndZ=0
    g1: ArcOfCircle CenterX=25 CenterY=28 CenterZ=0 NormalX=0 NormalY=0 NormalZ=1 AngleXU=0 Radius=8 StartAngle=5.86874 EndAngle=6.28319
    g2: LineSegment StartX=25.3227 StartY=-19 StartZ=0 EndX=37.3227 EndY=-19 EndZ=0
    g3: ArcOfCircle CenterX=25.3227 CenterY=-11 CenterZ=0 NormalX=0 NormalY=0 NormalZ=1 AngleXU=0 Radius=8 StartAngle=2.72715 EndAngle=4.71239
    g4: LineSegment StartX=43.4511 StartY=-16.1423 StartZ=0 EndX=59.5208 EndY=3.00881 EndZ=0
    g5: ArcOfCircle CenterX=37.3227 CenterY=-11 CenterZ=0 NormalX=0 NormalY=0 NormalZ=1 AngleXU=0 Radius=8 StartAngle=4.71239 EndAngle=5.58505
  constraints (17):
    c: Tangent(g1,g0) = 1.5708
    c: DistanceY(g-1,g1) = 28
    c: Radius(g1) = 8
    c: Horizontal(g2)
    c: Tangent(g3,g0) = -1.5708
    c: Tangent(g3,g2) = -1.5708
    c: Radius(g3) = 8
    c: Radius(g5) = 8
    c: Tangent(g5,g2) = -1.5708
    c: Tangent(g5,g4) = -1.5708
    c: Horizontal(g1,g1)
    c: DistanceX(g-1,g1) = 33
    c: DistanceY(g2,g-1) = 19
    c: DistanceX(g-1,g0) = 18
    c: DistanceX(g2,g2) = 12
    c: Angle(g4,g2) = 2.26893
    c: Distance(g4,g4) = 25
FEATURE [PartDesign::SubShapeBinder] Binder  label="rails-shape-binder-2"
  BindCopyOnChange = 0
  BindMode = 0
  ClaimChildren = false
  Context = -> Part001 [Body011.Binder.]
  Fuse = false
  MakeFace = true
  OffsetFill = false
  OffsetIntersection = false
  OffsetJoinType = 0
  OffsetOpenResult = false
  PartialLoad = false
  Refine = true
  Relative = true
  Support = -> [Sketch125,Sketch042,Sketch043,Sketch083]
  _Version = 2
FEATURE [Sketcher::SketchObject] Sketch126  label="wheel-cap-rail"
  ArcFitTolerance = 1e-06
  AttachmentOffset = pos=(0,0,-19) rot=(0,0,1;0rad)
  AttachmentSupport = -> [XY_Plane012]
  FullyConstrained = true
  MakeInternals = false
  MapMode = 5
  Placement = pos=(0,0,-19) rot=(0,0,1;0rad)
  sketch-geometry (1):
    g0: ArcOfCircle CenterX=0 CenterY=-52 CenterZ=0 NormalX=0 NormalY=0 NormalZ=1 AngleXU=0 Radius=33 StartAngle=3.14159 EndAngle=6.28319
  constraints (5):
    c: PointOnObject(g0,g-2)
    c: Horizontal(g0,g0)
    c: Radius(g0) = 33
    c: Horizontal(g0,g0)
    c: DistanceY(g0,g-1) = 52
FEATURE [PartDesign::SubShapeBinder] Binder002  label="rails-shape-binder-3"
  BindCopyOnChange = 0
  BindMode = 0
  ClaimChildren = false
  Context = -> Part001 [Body011.Binder002.]
  Fuse = false
  MakeFace = true
  OffsetFill = false
  OffsetIntersection = false
  OffsetJoinType = 0
  OffsetOpenResult = false
  PartialLoad = false
  Refine = true
  Relative = true
  Support = -> [Sketch125,Sketch042,Sketch043,Sketch083,Sketch126]
  _Version = 2
FEATURE [PartDesign::AdditivePipe] AdditivePipe
  AuxilleryCurvelinear = true
  AuxillerySpineTangent = false
  Binormal = (0,0,0)
  Mode = 0
  Placement = pos=(0,0,22.5) rot=(0,0,1;0rad)
  Profile = -> Sketch045
  Spine = -> Binder002
  SpineTangent = false
  Suppressed = false
  Transformation = 0
  Transition = 0
FEATURE [PartDesign::Body] Body011  label="rails"
  AllowCompound = false
  Group = -> [Sketch042,Sketch043,Sketch045,AdditivePipe,Sketch070,Sketch083,Binder001,Sketch125,Binder,Sketch126,Binder002]
  Origin = -> Origin012
  Tip = -> AdditivePipe
FEATURE [PartDesign::FeatureBase] Clone009
  BaseFeature = -> Body031
  Suppressed = false
FEATURE [PartDesign::Body] Body041  label="m4-bolt-cavity-clone-top-3"
  AllowCompound = false
  Group = -> [Clone009]
  Origin = -> Origin045
  Placement = pos=(-21,-84,28.5) rot=(0,0,1;0rad)
  Tip = -> Clone009
FEATURE [PartDesign::FeatureBase] Clone010
  BaseFeature = -> Body031
  Suppressed = false
FEATURE [PartDesign::Body] Body042  label="m4-bolt-cavity-clone-top-4"
  AllowCompound = false
  Group = -> [Clone010]
  Origin = -> Origin046
  Placement = pos=(21,-84,28.5) rot=(0,0,1;0rad)
  Tip = -> Clone010
FEATURE [Part::MultiFuse] Fusion  label="top-cavities"
  Shapes = -> [Body040,Body032,Body033,Body039,Body041,Body042]
FEATURE [Part::Cut] Cut006  label="top"
  Base = -> Body025
  Tool = -> Fusion
FEATURE [PartDesign::FeatureBase] Clone011
  BaseFeature = -> Body031
  Suppressed = false
FEATURE [PartDesign::Body] Body043  label="m4-bolt-cavity-clone-bottom-3"
  AllowCompound = false
  Group = -> [Clone011]
  Origin = -> Origin047
  Placement = pos=(-21,-84,28.5) rot=(0,0,1;0rad)
  Tip = -> Clone011
FEATURE [PartDesign::FeatureBase] Clone012
  BaseFeature = -> Body031
  Suppressed = false
FEATURE [PartDesign::Body] Body044  label="m4-bolt-cavity-clone-bottom-4"
  AllowCompound = false
  Group = -> [Clone012]
  Origin = -> Origin048
  Placement = pos=(21,-84,28.5) rot=(0,0,1;0rad)
  Tip = -> Clone012
FEATURE [Part::MultiFuse] Fusion001  label="bottom-cavities"
  Shapes = -> [Body027,Body034,Body035,Body038,Body043,Body044]
FEATURE [Sketcher::SketchObject] Sketch127
  ArcFitTolerance = 1e-06
  AttachmentSupport = -> [XZ_Plane050]
  FullyConstrained = true
  MakeInternals = false
  MapMode = 5
  Placement = pos=(0,0,0) rot=(1,0,0;1.5708rad)
  sketch-geometry (6):
    g0: LineSegment StartX=4 StartY=0 StartZ=0 EndX=9 EndY=0 EndZ=0
    g1: LineSegment StartX=9 StartY=0 StartZ=0 EndX=9 EndY=53 EndZ=0
    g2: LineSegment StartX=9 StartY=53 StartZ=0 EndX=0 EndY=53 EndZ=0
    g3: LineSegment StartX=0 StartY=53 StartZ=0 EndX=0 EndY=-22 EndZ=0
    g4: LineSegment StartX=0 StartY=-22 StartZ=0 EndX=4 EndY=-22 EndZ=0
    g5: LineSegment StartX=4 StartY=-22 StartZ=0 EndX=4 EndY=0 EndZ=0
  constraints (18):
    c: PointOnObject(g0,g-1)
    c: PointOnObject(g0,g-1)
    c: Coincident(g1,g0)
    c: Vertical(g1)
    c: Coincident(g2,g1)
    c: PointOnObject(g2,g-2)
    c: Horizontal(g2)
    c: Coincident(g2,g3)
    c: PointOnObject(g3,g-2)
    c: Coincident(g3,g4)
    c: Coincident(g4,g5)
    c: Coincident(g5,g0)
    c: Vertical(g5)
    c: Horizontal(g4)
    c: DistanceY(g5,g5) = 22
    c: DistanceY(g1,g1) = 53
    c: DistanceX(g2,g2) = 9
    c: DistanceX(g4,g4) = 4
FEATURE [PartDesign::Revolution] Revolution005
  Angle = 360
  Angle2 = 60
  Axis = (0,2e-16,1)
  Base = (0,0,0)
  Placement = pos=(0,0,0) rot=(1,0,0;1.5708rad)
  Profile = -> Sketch127
  ReferenceAxis = -> Sketch127 [V_Axis]
  Refine = true
  Reversed = true
  Suppressed = false
  Type = 0
FEATURE [PartDesign::Body] Body045  label="pin"
  AllowCompound = false
  Group = -> [Sketch127,Revolution005]
  Origin = -> Origin050
  Tip = -> Revolution005
FEATURE [Sketcher::SketchObject] Sketch128
  ArcFitTolerance = 1e-06
  AttachmentSupport = -> [XY_Plane051]
  FullyConstrained = true
  MakeInternals = false
  MapMode = 5
  sketch-geometry (2):
    g0: Circle CenterX=0 CenterY=0 CenterZ=0 NormalX=0 NormalY=0 NormalZ=1 AngleXU=0 Radius=71
    g1: Circle CenterX=0 CenterY=0 CenterZ=0 NormalX=0 NormalY=0 NormalZ=1 AngleXU=0 Radius=9
  constraints (4):
    c: Coincident(g0,g-1)
    c: Diameter(g0) = 142
    c: Coincident(g1,g0)
    c: Diameter(g1) = 18
FEATURE [PartDesign::Pad] Pad050
  Direction = (0,0,1)
  Length = 13.5
  Length2 = 10
  Profile = -> Sketch128
  ReferenceAxis = -> Sketch128 [N_Axis]
  Refine = true
  Reversed = true
  Suppressed = false
  Type = 0
FEATURE [Sketcher::SketchObject] Sketch129
  ArcFitTolerance = 1e-06
  AttachmentSupport = -> [XY_Plane052]
  FullyConstrained = true
  MakeInternals = false
  MapMode = 5
  sketch-geometry (2):
    g0: Circle CenterX=0 CenterY=0 CenterZ=0 NormalX=0 NormalY=0 NormalZ=1 AngleXU=0 Radius=35.5
    g1: Circle CenterX=0 CenterY=0 CenterZ=0 NormalX=0 NormalY=0 NormalZ=1 AngleXU=0 Radius=9
  constraints (4):
    c: Coincident(g0,g-1)
    c: Diameter(g0) = 71
    c: Coincident(g1,g0)
    c: Diameter(g1) = 18
FEATURE [PartDesign::Pad] Pad051
  Direction = (0,0,1)
  Length = 40
  Length2 = 10
  Profile = -> Sketch129
  ReferenceAxis = -> Sketch129 [N_Axis]
  Refine = true
  Suppressed = false
  Type = 0
FEATURE [PartDesign::Body] Body047  label="71mm-guide"
  AllowCompound = false
  Group = -> [Sketch129,Pad051]
  Origin = -> Origin052
  Tip = -> Pad051
FEATURE [Sketcher::SketchObject] Sketch130
  ArcFitTolerance = 1e-06
  AttachmentSupport = -> [XZ_Plane051]
  FullyConstrained = true
  MakeInternals = false
  MapMode = 5
  Placement = pos=(0,0,0) rot=(1,0,0;1.5708rad)
  sketch-geometry (6):
    g0: LineSegment StartX=0 StartY=0 StartZ=0 EndX=9 EndY=0 EndZ=0
    g1: LineSegment StartX=9 StartY=0 StartZ=0 EndX=9 EndY=-13.5 EndZ=0
    g2: LineSegment StartX=9 StartY=-13.5 StartZ=0 EndX=4 EndY=-13.5 EndZ=0
    g3: LineSegment StartX=4 StartY=-13.5 StartZ=0 EndX=4 EndY=-35.5 EndZ=0
    g4: LineSegment StartX=4 StartY=-35.5 StartZ=0 EndX=0 EndY=-35.5 EndZ=0
    g5: LineSegment StartX=0 StartY=-35.5 StartZ=0 EndX=0 EndY=0 EndZ=0
  constraints (17):
    c: Coincident(g0,g-1)
    c: PointOnObject(g0,g-1)
    c: Coincident(g1,g0)
    c: Vertical(g1)
    c: Coincident(g2,g1)
    c: Horizontal(g2)
    c: Coincident(g3,g2)
    c: Vertical(g3)
    c: Coincident(g4,g3)
    c: PointOnObject(g4,g-2)
    c: Coincident(g5,g4)
    c: Coincident(g5,g0)
    c: Horizontal(g4)
    c: DistanceX(g0,g0) = 9
    c: DistanceY(g1,g1) = 13.5
    c: DistanceX(g4,g4) = 4
    c: DistanceY(g3,g3) = 22
FEATURE [Sketcher::SketchObject] Sketch131
  ArcFitTolerance = 1e-06
  AttachmentSupport = -> [XY_Plane051]
  FullyConstrained = true
  MakeInternals = false
  MapMode = 5
  sketch-geometry (1):
    g0: Circle CenterX=0 CenterY=0 CenterZ=0 NormalX=0 NormalY=0 NormalZ=1 AngleXU=0 Radius=55
  constraints (2):
    c: Coincident(g0,g-1)
    c: Diameter(g0) = 110
FEATURE [PartDesign::Pad] Pad052
  BaseFeature = -> Pad050
  Direction = (0,0,1)
  Length = 55
  Length2 = 10
  Profile = -> Sketch131
  ReferenceAxis = -> Sketch131 [N_Axis]
  Refine = true
  Reversed = true
  Suppressed = false
  Type = 0
FEATURE [PartDesign::Groove] Groove
  Angle = 360
  Angle2 = 60
  Axis = (0,2e-16,1)
  Base = (0,0,0)
  BaseFeature = -> Pad052
  Profile = -> Sketch130
  ReferenceAxis = -> Sketch130 [V_Axis]
  Refine = true
  Suppressed = false
  Type = 0
FEATURE [PartDesign::Body] Body046  label="plate"
  AllowCompound = false
  Group = -> [Sketch128,Pad050,Sketch131,Sketch130,Pad052,Groove]
  Origin = -> Origin051
  Tip = -> Groove
FEATURE [Sketcher::SketchObject] Sketch132  label="turntable-base-outline"
  ArcFitTolerance = 1e-06
  AttachmentSupport = -> [XY_Plane054]
  FullyConstrained = true
  MakeInternals = false
  MapMode = 5
  sketch-geometry (4):
    g0: Circle CenterX=0 CenterY=0 CenterZ=0 NormalX=0 NormalY=0 NormalZ=1 AngleXU=0 Radius=30
    g1: Circle CenterX=-22.5 CenterY=0 CenterZ=0 NormalX=0 NormalY=0 NormalZ=1 AngleXU=0 Radius=4.5
    g2: Circle CenterX=22.5 CenterY=0 CenterZ=0 NormalX=0 NormalY=0 NormalZ=1 AngleXU=0 Radius=4.5
    g3: Circle CenterX=0 CenterY=0 CenterZ=0 NormalX=0 NormalY=0 NormalZ=1 AngleXU=0 Radius=4.5
  constraints (9):
    c: Coincident(g0,g-1)
    c: Diameter(g0) = 60
    c: PointOnObject(g1,g-1)
    c: Symmetric(g1,g2,g-2)
    c: DistanceX(g1,g2) = 45
    c: Diameter(g1) = 9
    c: Equal(g1,g2)
    c: Coincident(g3,g0)
    c: Equal(g3,g1)
FEATURE [PartDesign::Pad] Pad053  label="turntable-base-pad"
  Direction = (0,0,1)
  Length = 10
  Length2 = 10
  Profile = -> Sketch132
  ReferenceAxis = -> Sketch132 [N_Axis]
  Refine = true
  Reversed = true
  Suppressed = false
  Type = 0
FEATURE [PartDesign::Body] Body049  label="turntable-base"
  AllowCompound = false
  Group = -> [Sketch132,Pad053]
  Origin = -> Origin054
  Tip = -> Pad053
FEATURE [Sketcher::SketchObject] Sketch133
  ArcFitTolerance = 1e-06
  AttachmentSupport = -> [XY_Plane053]
  FullyConstrained = true
  MakeInternals = false
  MapMode = 5
  sketch-geometry (1):
    g0: Circle CenterX=0 CenterY=0 CenterZ=0 NormalX=0 NormalY=0 NormalZ=1 AngleXU=0 Radius=7.5
  constraints (2):
    c: Coincident(g0,g-1)
    c: Diameter(g0) = 15
FEATURE [PartDesign::Pad] Pad054
  Direction = (0,0,1)
  Length = 10
  Length2 = 10
  Profile = -> Sketch133
  ReferenceAxis = -> Sketch133 [N_Axis]
  Refine = true
  Suppressed = false
  Type = 0
FEATURE [PartDesign::Body] Body048  label="15mm bolt head"
  AllowCompound = false
  Group = -> [Sketch133,Pad054]
  Origin = -> Origin053
  Tip = -> Pad054
FEATURE [App::Part] Part003  label="metal-bender"
  Group = -> [Body045,Body046,Body047,Body048,Body049]
  Origin = -> Origin049
FEATURE [Sketcher::SketchObject] Sketch134
  ArcFitTolerance = 1e-06
  AttachmentSupport = -> [YZ_Plane033]
  FullyConstrained = false
  MakeInternals = false
  MapMode = 5
  Placement = pos=(0,0,0) rot=(0.57735,0.57735,0.57735;2.0944rad)
  sketch-geometry (12):
    g0: LineSegment StartX=-112 StartY=0 StartZ=0 EndX=-117 EndY=2 EndZ=0
    g1: LineSegment StartX=-117 StartY=2 StartZ=0 EndX=-117 EndY=6 EndZ=0
    g2: LineSegment StartX=-117 StartY=6 StartZ=0 EndX=-112 EndY=8 EndZ=0
    g3: LineSegment StartX=-112 StartY=8 StartZ=0 EndX=-93 EndY=8 EndZ=0
    g4: LineSegment StartX=-93 StartY=8 StartZ=0 EndX=-89 EndY=4 EndZ=0
    g5: LineSegment StartX=-89 StartY=4 StartZ=0 EndX=0 EndY=4 EndZ=0
    g6: LineSegment StartX=0 StartY=4 StartZ=0 EndX=0 EndY=0 EndZ=0
    g7: LineSegment StartX=0 StartY=0 StartZ=0 EndX=-112 EndY=0 EndZ=0
    g8: LineSegment StartX=-143.62 StartY=27.2064 StartZ=0 EndX=-143.62 EndY=-17.1049 EndZ=0
    g9: LineSegment StartX=-143.62 StartY=-17.1049 StartZ=0 EndX=13.7462 EndY=-17.1049 EndZ=0
    g10: LineSegment StartX=13.7462 StartY=-17.1049 StartZ=0 EndX=13.7462 EndY=27.2064 EndZ=0
    g11: LineSegment StartX=13.7462 StartY=27.2064 StartZ=0 EndX=-143.62 EndY=27.2064 EndZ=0
  constraints (31):
    c: PointOnObject(g0,g-1)
    c: Coincident(g1,g0)
    c: Vertical(g1)
    c: Coincident(g2,g1)
    c: Coincident(g3,g2)
    c: Horizontal(g3)
    c: Coincident(g4,g3)
    c: Coincident(g5,g4)
    c: PointOnObject(g5,g-2)
    c: Horizontal(g5)
    c: Coincident(g6,g5)
    c: Coincident(g6,g-1)
    c: Coincident(g7,g6)
    c: Coincident(g7,g0)
    c: DistanceX(g1,g4) = 28
    c: DistanceX(g0,g6) = 117
    c: Angle(g3,g4) = 2.35619
    c: DistanceY(g6,g6) = 4
    c: Distance(g7,g3) = 8
    c: DistanceX(g0,g0) = 5
    c: Vertical(g0,g2)
    c: Equal(g0,g2)
    c: DistanceY(g1,g1) = 4
    c: Coincident(g8,g9)
    c: Coincident(g9,g10)
    c: Coincident(g10,g11)
    c: Coincident(g11,g8)
    c: Vertical(g8)
    c: Vertical(g10)
    c: Horizontal(g9)
    c: Horizontal(g11)
FEATURE [PartDesign::Pocket] Pocket043
  BaseFeature = -> Pad045
  Direction = (-1,0,0)
  Length = 25
  Length2 = 5
  Midplane = true
  Profile = -> Sketch134
  ReferenceAxis = -> Sketch134 [N_Axis]
  Refine = true
  Suppressed = false
  Type = 0
FEATURE [PartDesign::Body] Body029  label="molle-clip"
  AllowCompound = false
  Group = -> [Sketch115,Pad045,Sketch134,Pocket043]
  Origin = -> Origin033
  Placement = pos=(-19,-87,24) rot=(0,0,1;3.14159rad)
  Tip = -> Pocket043
FEATURE [PartDesign::FeatureBase] Clone001
  BaseFeature = -> Body029
  Placement = pos=(-22,-87,24) rot=(0,0,1;3.14159rad)
  Suppressed = false
FEATURE [PartDesign::Body] Body030  label="molle-clip-clone-1"
  AllowCompound = false
  Group = -> [Clone001]
  Origin = -> Origin034
  Placement = pos=(41,0,0) rot=(0,0,1;0rad)
  Tip = -> Clone001
FEATURE [Sketcher::SketchObject] Sketch135
  ArcFitTolerance = 1e-06
  AttachmentSupport = -> [XZ_Plane055]
  FullyConstrained = false
  MakeInternals = false
  MapMode = 5
  Placement = pos=(0,0,0) rot=(1,0,0;1.5708rad)
  sketch-geometry (6):
    g0: LineSegment StartX=0 StartY=5 StartZ=0 EndX=3.6 EndY=5 EndZ=0
    g1: LineSegment StartX=3.6 StartY=5 StartZ=0 EndX=3.6 EndY=0 EndZ=0
    g2: LineSegment StartX=3.6 StartY=0 StartZ=0 EndX=2 EndY=0 EndZ=0
    g3: LineSegment StartX=2 StartY=0 StartZ=0 EndX=2 EndY=-8.67625 EndZ=0
    g4: LineSegment StartX=2 StartY=-8.67625 StartZ=0 EndX=0 EndY=-8.67625 EndZ=0
    g5: LineSegment StartX=0 StartY=-8.67625 StartZ=0 EndX=0 EndY=5 EndZ=0
  constraints (17):
    c: PointOnObject(g0,g-2)
    c: Horizontal(g0)
    c: Coincident(g1,g0)
    c: PointOnObject(g1,g-1)
    c: Vertical(g1)
    c: Coincident(g2,g1)
    c: PointOnObject(g2,g-1)
    c: Coincident(g3,g2)
    c: Vertical(g3)
    c: Coincident(g4,g3)
    c: PointOnObject(g4,g-2)
    c: Horizontal(g4)
    c: Coincident(g5,g4)
    c: Coincident(g5,g0)
    c: DistanceX(g0,g0) = 3.6
    c: DistanceX(g4,g4) = 2
    c: DistanceY(g1,g1) = 5
FEATURE [PartDesign::Revolution] Revolution006
  Angle = 360
  Angle2 = 60
  Axis = (0,2e-16,1)
  Base = (0,0,0)
  Placement = pos=(0,0,0) rot=(1,0,0;1.5708rad)
  Profile = -> Sketch135
  ReferenceAxis = -> Sketch135 [V_Axis]
  Refine = true
  Reversed = true
  Suppressed = false
  Type = 0
FEATURE [Sketcher::SketchObject] Sketch136
  ArcFitTolerance = 1e-06
  AttachmentOffset = pos=(0,0,5) rot=(0,0,1;0rad)
  AttachmentSupport = -> [XY_Plane055]
  FullyConstrained = true
  MakeInternals = false
  MapMode = 5
  Placement = pos=(0,0,5) rot=(0,0,1;0rad)
  sketch-geometry (7):
    g0: LineSegment StartX=1.5 StartY=0.866025 StartZ=0 EndX=2e-16 EndY=1.73205 EndZ=0
    g1: LineSegment StartX=2e-16 StartY=1.73205 StartZ=0 EndX=-1.5 EndY=0.866025 EndZ=0
    g2: LineSegment StartX=-1.5 StartY=0.866025 StartZ=0 EndX=-1.5 EndY=-0.866025 EndZ=0
    g3: LineSegment StartX=-1.5 StartY=-0.866025 StartZ=0 EndX=-2e-16 EndY=-1.73205 EndZ=0
    g4: LineSegment StartX=-2e-16 StartY=-1.73205 StartZ=0 EndX=1.5 EndY=-0.866025 EndZ=0
    g5: LineSegment StartX=1.5 StartY=-0.866025 StartZ=0 EndX=1.5 EndY=0.866025 EndZ=0
    g6: Circle [constr] CenterX=0 CenterY=0 CenterZ=0 NormalX=0 NormalY=0 NormalZ=1 AngleXU=0 Radius=1.73205
  constraints (16):
    c: Coincident(g0,g1)
    c: Coincident(g1,g2)
    c: Coincident(g2,g3)
    c: Coincident(g3,g4)
    c: Coincident(g4,g5)
    c: Coincident(g5,g0)
    c: Equal(g0, g1-g5) x5
    c: PointOnObject(g0,g6)
    c: PointOnObject(g1,g6)
    c: PointOnObject(g2,g6)
    c: PointOnObject(g3,g6)
    c: PointOnObject(g4,g6)
    c: PointOnObject(g5,g6)
    c: Coincident(g6,g-1)
    c: Vertical(g5)
    c: DistanceX(g1,g0) = 3
FEATURE [PartDesign::Pocket] Pocket044
  BaseFeature = -> Revolution006
  Direction = (0,0,-1)
  Length = 2
  Length2 = 5
  Placement = pos=(0,0,0) rot=(1,0,0;1.5708rad)
  Profile = -> Sketch136
  ReferenceAxis = -> Sketch136 [N_Axis]
  Refine = true
  Suppressed = false
  Type = 0
FEATURE [PartDesign::Body] Body050  label="bolt-m4-l10"
  AllowCompound = false
  Group = -> [Sketch135,Revolution006,Sketch136,Pocket044]
  Origin = -> Origin055
  Tip = -> Pocket044
FEATURE [Sketcher::SketchObject] Sketch137  label="cnc-channel-path"
  ArcFitTolerance = 1e-06
  AttachmentSupport = -> [XY_Plane027]
  FullyConstrained = true
  MakeInternals = false
  MapMode = 5
  sketch-geometry (4):
    g0: LineSegment StartX=-31 StartY=-135 StartZ=0 EndX=-31 EndY=25 EndZ=0
    g1: LineSegment StartX=-31 StartY=25 StartZ=0 EndX=3.6e-15 EndY=60 EndZ=0
    g2: LineSegment StartX=3.6e-15 StartY=60 StartZ=0 EndX=31 EndY=25 EndZ=0
    g3: LineSegment StartX=31 StartY=25 StartZ=0 EndX=31 EndY=-135 EndZ=0
  constraints (11):
    c: Vertical(g0)
    c: Coincident(g1,g0)
    c: PointOnObject(g1,g-2)
    c: Coincident(g2,g1)
    c: Coincident(g3,g2)
    c: Symmetric(g0,g2,g-2)
    c: Symmetric(g0,g3,g-2)
    c: DistanceX(g0,g3) = 62
    c: DistanceY(g2,g1) = 35
    c: DistanceY(g3,g2) = 160
    c: DistanceY(g-1,g1) = 60
FEATURE [Sketcher::SketchObject] Sketch138  label="cnc-channel-curve-pocket"
  ArcFitTolerance = 1e-06
  AttachmentSupport = -> [XY_Plane027]
  FullyConstrained = false
  MakeInternals = false
  MapMode = 5
  sketch-geometry (2):
    g0: LineSegment StartX=0 StartY=60 StartZ=0 EndX=31 EndY=25 EndZ=0
    g1: ArcOfCircle CenterX=0 CenterY=28.7714 CenterZ=0 NormalX=0 NormalY=0 NormalZ=1 AngleXU=0 Radius=31.2286 StartAngle=6.16212 EndAngle=7.85398
  constraints (5):
    c: PointOnObject(g0,g-2)
    c: DistanceY(g-1,g0) = 60
    c: DistanceY(g0,g0) = 35
    c: Coincident(g1,g0)
    c: PointOnObject(g1,g-2)
FEATURE [PartDesign::Body] Body024  label="bottom-block"
  AllowCompound = false
  Group = -> [Sketch104,Pad041,Fillet001,Sketch137,Sketch138]
  Origin = -> Origin027
  Placement = pos=(0,0,22.5) rot=(0,0,1;0rad)
  Tip = -> Fillet001
FEATURE [Part::Cut] Cut005  label="bottom"
  Base = -> Body024
  Tool = -> Fusion001
FEATURE [App::Part] Part002  label="base"
  Group = -> [Body031,Body026,Body036,Body037,Body024,Body027,Body034,Body035,Body038,Fusion001,Cut005,Body025,Body032,Body033,Body039,Body040,Fusion,Cut006,Sketch118]
  Origin = -> Origin029
FEATURE [App::Part] Part001  label="holster"
  Group = -> [Body011,Body015,Body016,Body020,Body021,Body022,Part002,Body028,Body029,Body030,Body050]
  Origin = -> Origin013
